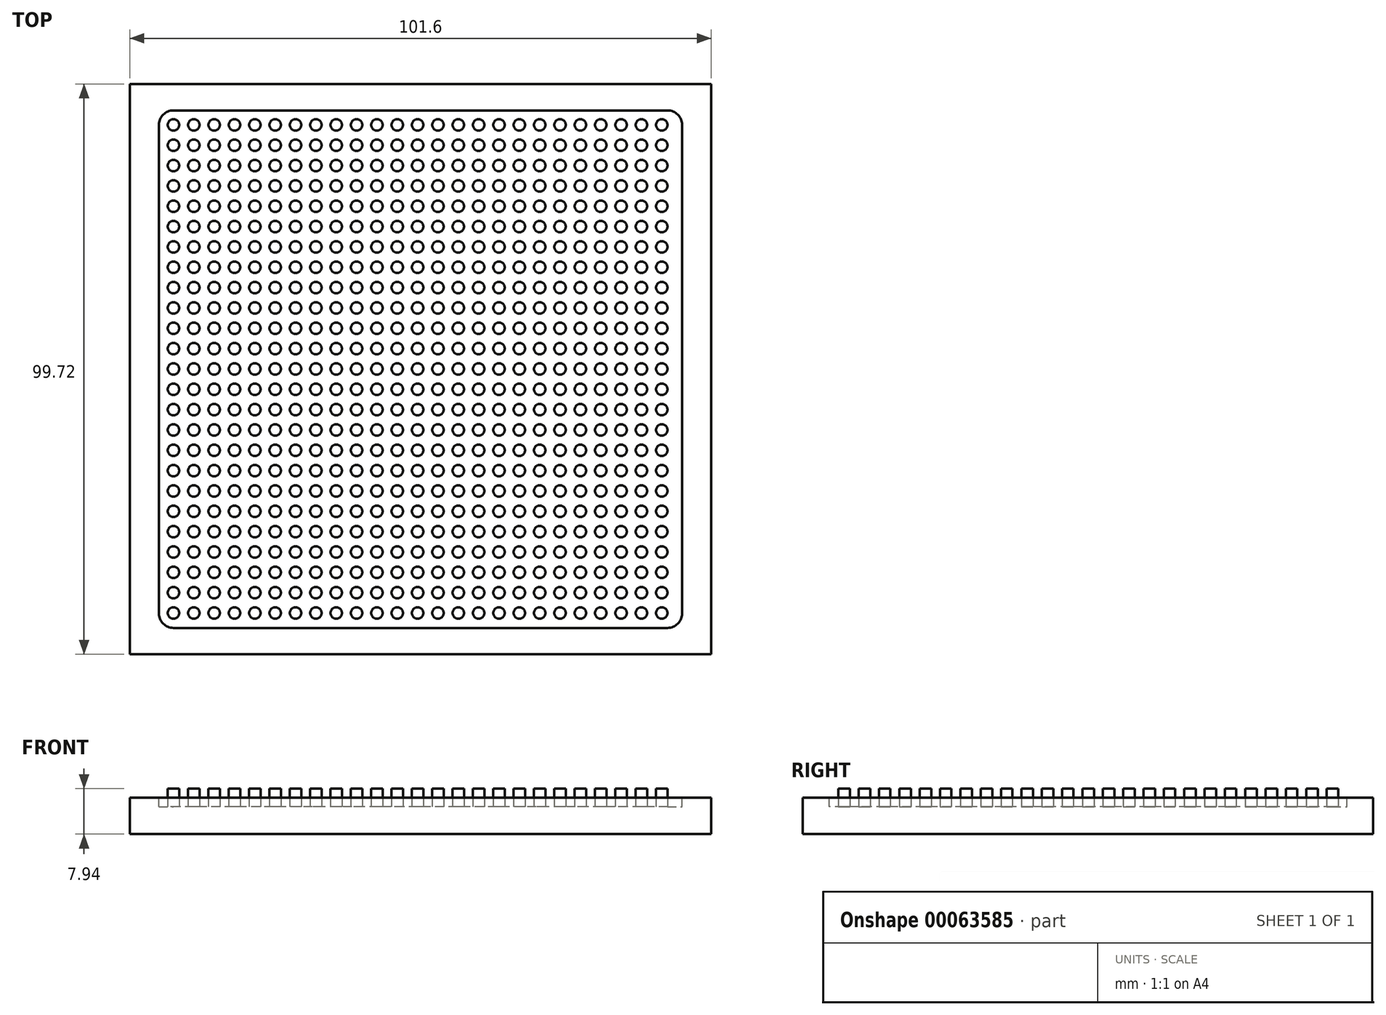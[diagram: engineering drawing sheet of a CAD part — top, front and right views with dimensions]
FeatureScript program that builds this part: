
annotation { "Feature Type Name" : "Feature", "Feature Type Description" : "" }
export const myFeature = defineFeature(function(context is Context, id is Id, definition is map)
    precondition{}
    {
        {
            var Q0;
            Q0=qCreatedBy(makeId("Top.planeOp"),FACE);
            var sketch = newSketch(context, id + "F0", { "sketchPlane" : qUnion([Q0])});
            skLineSegment(sketch, "E0.rect.bottom", {"start": v(50.8, 49.86) * mm, "end": v(-50.8, 49.86) * mm});
            skLineSegment(sketch, "E0.rect.top", {"start": v(50.8, -49.86) * mm, "end": v(-50.8, -49.86) * mm});
            skLineSegment(sketch, "E0.rect.left", {"start": v(50.8, 49.86) * mm, "end": v(50.8, -49.86) * mm});
            skLineSegment(sketch, "E0.rect.right", {"start": v(-50.8, 49.86) * mm, "end": v(-50.8, -49.86) * mm});
            skPoint(sketch, "E0.rect.middle", {"position": v(0, 0) * mm});
            skSolve(sketch);
        }
        {
            var Q0;
            Q0=makeQuery(id+"F0.imprint","IMPRINT",FACE,{"disambiguationData":[TD([[makeQuery(id+"F0.imprint","IMPRINT",EDGE,{"derivedFrom":sQuery(id+"F0.wireOp",EDGE,"E0.rect.bottom")}),1.0]])]});
            extrude(context, id + "F1", {"entities" : qUnion([Q0]), "depth" : 6.35 * mm});
        }
        {
            var Q0;
            Q0=makeQuery(id+"F1.opExtrude","CAP_FACE",FACE,{"disambiguationData":[OSD([sQuery(id+"F0.wireOp",EDGE,"E0.rect.bottom"),sQuery(id+"F0.wireOp",EDGE,"E0.rect.top"),sQuery(id+"F0.wireOp",EDGE,"E0.rect.left"),sQuery(id+"F0.wireOp",EDGE,"E0.rect.right")])],"isStart":false});
            var sketch = newSketch(context, id + "F2", { "sketchPlane" : qUnion([Q0])});
            skLineSegment(sketch, "E1.rect.bottom", {"start": v(43.18, 45.25) * mm, "end": v(-43.18, 45.25) * mm});
            skLineSegment(sketch, "E1.rect.top", {"start": v(43.18, -45.25) * mm, "end": v(-43.18, -45.25) * mm});
            skLineSegment(sketch, "E1.rect.left", {"start": v(45.72, 42.7) * mm, "end": v(45.72, -42.7) * mm});
            skLineSegment(sketch, "E1.rect.right", {"start": v(-45.72, 42.7) * mm, "end": v(-45.72, -42.7) * mm});
            skPoint(sketch, "E1.rect.middle", {"position": v(0, 0) * mm});
            skPoint(sketch, "E2.visualSharp", {"position": v(-45.72, 45.25) * mm});
            skArc(sketch, "E2.filletArc", {"start": v(-43.18, 45.25) * mm, "mid": v(-44.98, 44.5) * mm, "end": v(-45.72, 42.7) * mm});
            skPoint(sketch, "E3.visualSharp", {"position": v(-45.72, -45.25) * mm});
            skArc(sketch, "E3.filletArc", {"start": v(-45.72, -42.7) * mm, "mid": v(-44.98, -44.5) * mm, "end": v(-43.18, -45.25) * mm});
            skPoint(sketch, "E4.visualSharp", {"position": v(45.72, -45.25) * mm});
            skArc(sketch, "E4.filletArc", {"start": v(43.18, -45.25) * mm, "mid": v(44.98, -44.5) * mm, "end": v(45.72, -42.7) * mm});
            skPoint(sketch, "E5.visualSharp", {"position": v(45.72, 45.25) * mm});
            skArc(sketch, "E5.filletArc", {"start": v(45.72, 42.7) * mm, "mid": v(44.98, 44.5) * mm, "end": v(43.18, 45.25) * mm});
            skSolve(sketch);
        }
        {
            var Q0;
            Q0=makeQuery(id+"F2.imprint","IMPRINT",FACE,{"disambiguationData":[TD([[makeQuery(id+"F2.imprint","IMPRINT",EDGE,{"derivedFrom":sQuery(id+"F2.wireOp",EDGE,"E1.rect.bottom")}),1.0]])]});
            extrude(context, id + "F3", {"entities" : qUnion([Q0]), "operationType" : NewBodyOperationType.REMOVE, "oppositeDirection" : true, "depth" : 1.59 * mm});
        }
        {
            var Q0;
            Q0=makeQuery(id+"F3.boolean.opBoolean","COPY",FACE,{"derivedFrom":makeQuery(id+"F3.opExtrude","CAP_FACE",FACE,{"disambiguationData":[OSD([sQuery(id+"F2.wireOp",EDGE,"E1.rect.bottom"),sQuery(id+"F2.wireOp",EDGE,"E1.rect.top"),sQuery(id+"F2.wireOp",EDGE,"E1.rect.left"),sQuery(id+"F2.wireOp",EDGE,"E1.rect.right"),sQuery(id+"F2.wireOp",EDGE,"E2.filletArc"),sQuery(id+"F2.wireOp",EDGE,"E3.filletArc"),sQuery(id+"F2.wireOp",EDGE,"E4.filletArc"),sQuery(id+"F2.wireOp",EDGE,"E5.filletArc")])],"isStart":false})});
            var sketch = newSketch(context, id + "F4", { "sketchPlane" : qUnion([Q0])});
            skCircle(sketch, "E6", {"center": v(-43.18, 42.7) * mm, "radius": 1 * mm});
            skCircle(sketch, "E7.0.1.0", {"center": v(-43.18, 39.15) * mm, "radius": 1 * mm});
            skCircle(sketch, "E7.0.2.0", {"center": v(-43.18, 35.6) * mm, "radius": 1 * mm});
            skCircle(sketch, "E7.0.3.0", {"center": v(-43.18, 32.04) * mm, "radius": 1 * mm});
            skCircle(sketch, "E7.0.4.0", {"center": v(-43.18, 28.48) * mm, "radius": 1 * mm});
            skCircle(sketch, "E7.0.5.0", {"center": v(-43.18, 24.93) * mm, "radius": 1 * mm});
            skCircle(sketch, "E7.0.6.0", {"center": v(-43.18, 21.37) * mm, "radius": 1 * mm});
            skCircle(sketch, "E7.0.7.0", {"center": v(-43.18, 17.81) * mm, "radius": 1 * mm});
            skCircle(sketch, "E7.0.8.0", {"center": v(-43.18, 14.26) * mm, "radius": 1 * mm});
            skCircle(sketch, "E7.0.9.0", {"center": v(-43.18, 10.7) * mm, "radius": 1 * mm});
            skCircle(sketch, "E7.0.10.0", {"center": v(-43.18, 7.15) * mm, "radius": 1 * mm});
            skCircle(sketch, "E7.0.11.0", {"center": v(-43.18, 3.6) * mm, "radius": 1 * mm});
            skCircle(sketch, "E7.0.12.0", {"center": v(-43.18, 0.03) * mm, "radius": 1 * mm});
            skCircle(sketch, "E7.0.13.0", {"center": v(-43.18, -3.52) * mm, "radius": 1 * mm});
            skCircle(sketch, "E7.0.14.0", {"center": v(-43.18, -7.08) * mm, "radius": 1 * mm});
            skCircle(sketch, "E7.0.15.0", {"center": v(-43.18, -10.63) * mm, "radius": 1 * mm});
            skCircle(sketch, "E7.0.16.0", {"center": v(-43.18, -14.19) * mm, "radius": 1 * mm});
            skCircle(sketch, "E7.0.17.0", {"center": v(-43.18, -17.75) * mm, "radius": 1 * mm});
            skCircle(sketch, "E7.0.18.0", {"center": v(-43.18, -21.3) * mm, "radius": 1 * mm});
            skCircle(sketch, "E7.0.19.0", {"center": v(-43.18, -24.86) * mm, "radius": 1 * mm});
            skCircle(sketch, "E7.0.20.0", {"center": v(-43.18, -28.41) * mm, "radius": 1 * mm});
            skCircle(sketch, "E7.0.21.0", {"center": v(-43.18, -31.97) * mm, "radius": 1 * mm});
            skCircle(sketch, "E7.0.22.0", {"center": v(-43.18, -35.53) * mm, "radius": 1 * mm});
            skCircle(sketch, "E7.0.23.0", {"center": v(-43.18, -39.08) * mm, "radius": 1 * mm});
            skCircle(sketch, "E7.0.24.0", {"center": v(-43.18, -42.64) * mm, "radius": 1 * mm});
            skCircle(sketch, "E7.1.0.0", {"center": v(-39.62, 42.7) * mm, "radius": 1 * mm});
            skCircle(sketch, "E7.1.1.0", {"center": v(-39.62, 39.15) * mm, "radius": 1 * mm});
            skCircle(sketch, "E7.1.2.0", {"center": v(-39.62, 35.6) * mm, "radius": 1 * mm});
            skCircle(sketch, "E7.1.3.0", {"center": v(-39.62, 32.04) * mm, "radius": 1 * mm});
            skCircle(sketch, "E7.1.4.0", {"center": v(-39.62, 28.48) * mm, "radius": 1 * mm});
            skCircle(sketch, "E7.1.5.0", {"center": v(-39.62, 24.93) * mm, "radius": 1 * mm});
            skCircle(sketch, "E7.1.6.0", {"center": v(-39.62, 21.37) * mm, "radius": 1 * mm});
            skCircle(sketch, "E7.1.7.0", {"center": v(-39.62, 17.81) * mm, "radius": 1 * mm});
            skCircle(sketch, "E7.1.8.0", {"center": v(-39.62, 14.26) * mm, "radius": 1 * mm});
            skCircle(sketch, "E7.1.9.0", {"center": v(-39.62, 10.7) * mm, "radius": 1 * mm});
            skCircle(sketch, "E7.1.10.0", {"center": v(-39.62, 7.15) * mm, "radius": 1 * mm});
            skCircle(sketch, "E7.1.11.0", {"center": v(-39.62, 3.6) * mm, "radius": 1 * mm});
            skCircle(sketch, "E7.1.12.0", {"center": v(-39.62, 0.03) * mm, "radius": 1 * mm});
            skCircle(sketch, "E7.1.13.0", {"center": v(-39.62, -3.52) * mm, "radius": 1 * mm});
            skCircle(sketch, "E7.1.14.0", {"center": v(-39.62, -7.08) * mm, "radius": 1 * mm});
            skCircle(sketch, "E7.1.15.0", {"center": v(-39.62, -10.63) * mm, "radius": 1 * mm});
            skCircle(sketch, "E7.1.16.0", {"center": v(-39.62, -14.19) * mm, "radius": 1 * mm});
            skCircle(sketch, "E7.1.17.0", {"center": v(-39.62, -17.75) * mm, "radius": 1 * mm});
            skCircle(sketch, "E7.1.18.0", {"center": v(-39.62, -21.3) * mm, "radius": 1 * mm});
            skCircle(sketch, "E7.1.19.0", {"center": v(-39.62, -24.86) * mm, "radius": 1 * mm});
            skCircle(sketch, "E7.1.20.0", {"center": v(-39.62, -28.41) * mm, "radius": 1 * mm});
            skCircle(sketch, "E7.1.21.0", {"center": v(-39.62, -31.97) * mm, "radius": 1 * mm});
            skCircle(sketch, "E7.1.22.0", {"center": v(-39.62, -35.53) * mm, "radius": 1 * mm});
            skCircle(sketch, "E7.1.23.0", {"center": v(-39.62, -39.08) * mm, "radius": 1 * mm});
            skCircle(sketch, "E7.1.24.0", {"center": v(-39.62, -42.64) * mm, "radius": 1 * mm});
            skCircle(sketch, "E7.2.0.0", {"center": v(-36.07, 42.7) * mm, "radius": 1 * mm});
            skCircle(sketch, "E7.2.1.0", {"center": v(-36.07, 39.15) * mm, "radius": 1 * mm});
            skCircle(sketch, "E7.2.2.0", {"center": v(-36.07, 35.6) * mm, "radius": 1 * mm});
            skCircle(sketch, "E7.2.3.0", {"center": v(-36.07, 32.04) * mm, "radius": 1 * mm});
            skCircle(sketch, "E7.2.4.0", {"center": v(-36.07, 28.48) * mm, "radius": 1 * mm});
            skCircle(sketch, "E7.2.5.0", {"center": v(-36.07, 24.93) * mm, "radius": 1 * mm});
            skCircle(sketch, "E7.2.6.0", {"center": v(-36.07, 21.37) * mm, "radius": 1 * mm});
            skCircle(sketch, "E7.2.7.0", {"center": v(-36.07, 17.81) * mm, "radius": 1 * mm});
            skCircle(sketch, "E7.2.8.0", {"center": v(-36.07, 14.26) * mm, "radius": 1 * mm});
            skCircle(sketch, "E7.2.9.0", {"center": v(-36.07, 10.7) * mm, "radius": 1 * mm});
            skCircle(sketch, "E7.2.10.0", {"center": v(-36.07, 7.15) * mm, "radius": 1 * mm});
            skCircle(sketch, "E7.2.11.0", {"center": v(-36.07, 3.6) * mm, "radius": 1 * mm});
            skCircle(sketch, "E7.2.12.0", {"center": v(-36.07, 0.03) * mm, "radius": 1 * mm});
            skCircle(sketch, "E7.2.13.0", {"center": v(-36.07, -3.52) * mm, "radius": 1 * mm});
            skCircle(sketch, "E7.2.14.0", {"center": v(-36.07, -7.08) * mm, "radius": 1 * mm});
            skCircle(sketch, "E7.2.15.0", {"center": v(-36.07, -10.63) * mm, "radius": 1 * mm});
            skCircle(sketch, "E7.2.16.0", {"center": v(-36.07, -14.19) * mm, "radius": 1 * mm});
            skCircle(sketch, "E7.2.17.0", {"center": v(-36.07, -17.75) * mm, "radius": 1 * mm});
            skCircle(sketch, "E7.2.18.0", {"center": v(-36.07, -21.3) * mm, "radius": 1 * mm});
            skCircle(sketch, "E7.2.19.0", {"center": v(-36.07, -24.86) * mm, "radius": 1 * mm});
            skCircle(sketch, "E7.2.20.0", {"center": v(-36.07, -28.41) * mm, "radius": 1 * mm});
            skCircle(sketch, "E7.2.21.0", {"center": v(-36.07, -31.97) * mm, "radius": 1 * mm});
            skCircle(sketch, "E7.2.22.0", {"center": v(-36.07, -35.53) * mm, "radius": 1 * mm});
            skCircle(sketch, "E7.2.23.0", {"center": v(-36.07, -39.08) * mm, "radius": 1 * mm});
            skCircle(sketch, "E7.2.24.0", {"center": v(-36.07, -42.64) * mm, "radius": 1 * mm});
            skCircle(sketch, "E7.3.0.0", {"center": v(-32.51, 42.7) * mm, "radius": 1 * mm});
            skCircle(sketch, "E7.3.1.0", {"center": v(-32.51, 39.15) * mm, "radius": 1 * mm});
            skCircle(sketch, "E7.3.2.0", {"center": v(-32.51, 35.6) * mm, "radius": 1 * mm});
            skCircle(sketch, "E7.3.3.0", {"center": v(-32.51, 32.04) * mm, "radius": 1 * mm});
            skCircle(sketch, "E7.3.4.0", {"center": v(-32.51, 28.48) * mm, "radius": 1 * mm});
            skCircle(sketch, "E7.3.5.0", {"center": v(-32.51, 24.93) * mm, "radius": 1 * mm});
            skCircle(sketch, "E7.3.6.0", {"center": v(-32.51, 21.37) * mm, "radius": 1 * mm});
            skCircle(sketch, "E7.3.7.0", {"center": v(-32.51, 17.81) * mm, "radius": 1 * mm});
            skCircle(sketch, "E7.3.8.0", {"center": v(-32.51, 14.26) * mm, "radius": 1 * mm});
            skCircle(sketch, "E7.3.9.0", {"center": v(-32.51, 10.7) * mm, "radius": 1 * mm});
            skCircle(sketch, "E7.3.10.0", {"center": v(-32.51, 7.15) * mm, "radius": 1 * mm});
            skCircle(sketch, "E7.3.11.0", {"center": v(-32.51, 3.6) * mm, "radius": 1 * mm});
            skCircle(sketch, "E7.3.12.0", {"center": v(-32.51, 0.03) * mm, "radius": 1 * mm});
            skCircle(sketch, "E7.3.13.0", {"center": v(-32.51, -3.52) * mm, "radius": 1 * mm});
            skCircle(sketch, "E7.3.14.0", {"center": v(-32.51, -7.08) * mm, "radius": 1 * mm});
            skCircle(sketch, "E7.3.15.0", {"center": v(-32.51, -10.63) * mm, "radius": 1 * mm});
            skCircle(sketch, "E7.3.16.0", {"center": v(-32.51, -14.19) * mm, "radius": 1 * mm});
            skCircle(sketch, "E7.3.17.0", {"center": v(-32.51, -17.75) * mm, "radius": 1 * mm});
            skCircle(sketch, "E7.3.18.0", {"center": v(-32.51, -21.3) * mm, "radius": 1 * mm});
            skCircle(sketch, "E7.3.19.0", {"center": v(-32.51, -24.86) * mm, "radius": 1 * mm});
            skCircle(sketch, "E7.3.20.0", {"center": v(-32.51, -28.41) * mm, "radius": 1 * mm});
            skCircle(sketch, "E7.3.21.0", {"center": v(-32.51, -31.97) * mm, "radius": 1 * mm});
            skCircle(sketch, "E7.3.22.0", {"center": v(-32.51, -35.53) * mm, "radius": 1 * mm});
            skCircle(sketch, "E7.3.23.0", {"center": v(-32.51, -39.08) * mm, "radius": 1 * mm});
            skCircle(sketch, "E7.3.24.0", {"center": v(-32.51, -42.64) * mm, "radius": 1 * mm});
            skCircle(sketch, "E7.4.0.0", {"center": v(-28.96, 42.7) * mm, "radius": 1 * mm});
            skCircle(sketch, "E7.4.1.0", {"center": v(-28.96, 39.15) * mm, "radius": 1 * mm});
            skCircle(sketch, "E7.4.2.0", {"center": v(-28.96, 35.6) * mm, "radius": 1 * mm});
            skCircle(sketch, "E7.4.3.0", {"center": v(-28.96, 32.04) * mm, "radius": 1 * mm});
            skCircle(sketch, "E7.4.4.0", {"center": v(-28.96, 28.48) * mm, "radius": 1 * mm});
            skCircle(sketch, "E7.4.5.0", {"center": v(-28.96, 24.93) * mm, "radius": 1 * mm});
            skCircle(sketch, "E7.4.6.0", {"center": v(-28.96, 21.37) * mm, "radius": 1 * mm});
            skCircle(sketch, "E7.4.7.0", {"center": v(-28.96, 17.81) * mm, "radius": 1 * mm});
            skCircle(sketch, "E7.4.8.0", {"center": v(-28.96, 14.26) * mm, "radius": 1 * mm});
            skCircle(sketch, "E7.4.9.0", {"center": v(-28.96, 10.7) * mm, "radius": 1 * mm});
            skCircle(sketch, "E7.4.10.0", {"center": v(-28.96, 7.15) * mm, "radius": 1 * mm});
            skCircle(sketch, "E7.4.11.0", {"center": v(-28.96, 3.6) * mm, "radius": 1 * mm});
            skCircle(sketch, "E7.4.12.0", {"center": v(-28.96, 0.03) * mm, "radius": 1 * mm});
            skCircle(sketch, "E7.4.13.0", {"center": v(-28.96, -3.52) * mm, "radius": 1 * mm});
            skCircle(sketch, "E7.4.14.0", {"center": v(-28.96, -7.08) * mm, "radius": 1 * mm});
            skCircle(sketch, "E7.4.15.0", {"center": v(-28.96, -10.63) * mm, "radius": 1 * mm});
            skCircle(sketch, "E7.4.16.0", {"center": v(-28.96, -14.19) * mm, "radius": 1 * mm});
            skCircle(sketch, "E7.4.17.0", {"center": v(-28.96, -17.75) * mm, "radius": 1 * mm});
            skCircle(sketch, "E7.4.18.0", {"center": v(-28.96, -21.3) * mm, "radius": 1 * mm});
            skCircle(sketch, "E7.4.19.0", {"center": v(-28.96, -24.86) * mm, "radius": 1 * mm});
            skCircle(sketch, "E7.4.20.0", {"center": v(-28.96, -28.41) * mm, "radius": 1 * mm});
            skCircle(sketch, "E7.4.21.0", {"center": v(-28.96, -31.97) * mm, "radius": 1 * mm});
            skCircle(sketch, "E7.4.22.0", {"center": v(-28.96, -35.53) * mm, "radius": 1 * mm});
            skCircle(sketch, "E7.4.23.0", {"center": v(-28.96, -39.08) * mm, "radius": 1 * mm});
            skCircle(sketch, "E7.4.24.0", {"center": v(-28.96, -42.64) * mm, "radius": 1 * mm});
            skCircle(sketch, "E7.5.0.0", {"center": v(-25.4, 42.7) * mm, "radius": 1 * mm});
            skCircle(sketch, "E7.5.1.0", {"center": v(-25.4, 39.15) * mm, "radius": 1 * mm});
            skCircle(sketch, "E7.5.2.0", {"center": v(-25.4, 35.6) * mm, "radius": 1 * mm});
            skCircle(sketch, "E7.5.3.0", {"center": v(-25.4, 32.04) * mm, "radius": 1 * mm});
            skCircle(sketch, "E7.5.4.0", {"center": v(-25.4, 28.48) * mm, "radius": 1 * mm});
            skCircle(sketch, "E7.5.5.0", {"center": v(-25.4, 24.93) * mm, "radius": 1 * mm});
            skCircle(sketch, "E7.5.6.0", {"center": v(-25.4, 21.37) * mm, "radius": 1 * mm});
            skCircle(sketch, "E7.5.7.0", {"center": v(-25.4, 17.81) * mm, "radius": 1 * mm});
            skCircle(sketch, "E7.5.8.0", {"center": v(-25.4, 14.26) * mm, "radius": 1 * mm});
            skCircle(sketch, "E7.5.9.0", {"center": v(-25.4, 10.7) * mm, "radius": 1 * mm});
            skCircle(sketch, "E7.5.10.0", {"center": v(-25.4, 7.15) * mm, "radius": 1 * mm});
            skCircle(sketch, "E7.5.11.0", {"center": v(-25.4, 3.6) * mm, "radius": 1 * mm});
            skCircle(sketch, "E7.5.12.0", {"center": v(-25.4, 0.03) * mm, "radius": 1 * mm});
            skCircle(sketch, "E7.5.13.0", {"center": v(-25.4, -3.52) * mm, "radius": 1 * mm});
            skCircle(sketch, "E7.5.14.0", {"center": v(-25.4, -7.08) * mm, "radius": 1 * mm});
            skCircle(sketch, "E7.5.15.0", {"center": v(-25.4, -10.63) * mm, "radius": 1 * mm});
            skCircle(sketch, "E7.5.16.0", {"center": v(-25.4, -14.19) * mm, "radius": 1 * mm});
            skCircle(sketch, "E7.5.17.0", {"center": v(-25.4, -17.75) * mm, "radius": 1 * mm});
            skCircle(sketch, "E7.5.18.0", {"center": v(-25.4, -21.3) * mm, "radius": 1 * mm});
            skCircle(sketch, "E7.5.19.0", {"center": v(-25.4, -24.86) * mm, "radius": 1 * mm});
            skCircle(sketch, "E7.5.20.0", {"center": v(-25.4, -28.41) * mm, "radius": 1 * mm});
            skCircle(sketch, "E7.5.21.0", {"center": v(-25.4, -31.97) * mm, "radius": 1 * mm});
            skCircle(sketch, "E7.5.22.0", {"center": v(-25.4, -35.53) * mm, "radius": 1 * mm});
            skCircle(sketch, "E7.5.23.0", {"center": v(-25.4, -39.08) * mm, "radius": 1 * mm});
            skCircle(sketch, "E7.5.24.0", {"center": v(-25.4, -42.64) * mm, "radius": 1 * mm});
            skCircle(sketch, "E7.6.0.0", {"center": v(-21.84, 42.7) * mm, "radius": 1 * mm});
            skCircle(sketch, "E7.6.1.0", {"center": v(-21.84, 39.15) * mm, "radius": 1 * mm});
            skCircle(sketch, "E7.6.2.0", {"center": v(-21.84, 35.6) * mm, "radius": 1 * mm});
            skCircle(sketch, "E7.6.3.0", {"center": v(-21.84, 32.04) * mm, "radius": 1 * mm});
            skCircle(sketch, "E7.6.4.0", {"center": v(-21.84, 28.48) * mm, "radius": 1 * mm});
            skCircle(sketch, "E7.6.5.0", {"center": v(-21.84, 24.93) * mm, "radius": 1 * mm});
            skCircle(sketch, "E7.6.6.0", {"center": v(-21.84, 21.37) * mm, "radius": 1 * mm});
            skCircle(sketch, "E7.6.7.0", {"center": v(-21.84, 17.81) * mm, "radius": 1 * mm});
            skCircle(sketch, "E7.6.8.0", {"center": v(-21.84, 14.26) * mm, "radius": 1 * mm});
            skCircle(sketch, "E7.6.9.0", {"center": v(-21.84, 10.7) * mm, "radius": 1 * mm});
            skCircle(sketch, "E7.6.10.0", {"center": v(-21.84, 7.15) * mm, "radius": 1 * mm});
            skCircle(sketch, "E7.6.11.0", {"center": v(-21.84, 3.6) * mm, "radius": 1 * mm});
            skCircle(sketch, "E7.6.12.0", {"center": v(-21.84, 0.03) * mm, "radius": 1 * mm});
            skCircle(sketch, "E7.6.13.0", {"center": v(-21.84, -3.52) * mm, "radius": 1 * mm});
            skCircle(sketch, "E7.6.14.0", {"center": v(-21.84, -7.08) * mm, "radius": 1 * mm});
            skCircle(sketch, "E7.6.15.0", {"center": v(-21.84, -10.63) * mm, "radius": 1 * mm});
            skCircle(sketch, "E7.6.16.0", {"center": v(-21.84, -14.19) * mm, "radius": 1 * mm});
            skCircle(sketch, "E7.6.17.0", {"center": v(-21.84, -17.75) * mm, "radius": 1 * mm});
            skCircle(sketch, "E7.6.18.0", {"center": v(-21.84, -21.3) * mm, "radius": 1 * mm});
            skCircle(sketch, "E7.6.19.0", {"center": v(-21.84, -24.86) * mm, "radius": 1 * mm});
            skCircle(sketch, "E7.6.20.0", {"center": v(-21.84, -28.41) * mm, "radius": 1 * mm});
            skCircle(sketch, "E7.6.21.0", {"center": v(-21.84, -31.97) * mm, "radius": 1 * mm});
            skCircle(sketch, "E7.6.22.0", {"center": v(-21.84, -35.53) * mm, "radius": 1 * mm});
            skCircle(sketch, "E7.6.23.0", {"center": v(-21.84, -39.08) * mm, "radius": 1 * mm});
            skCircle(sketch, "E7.6.24.0", {"center": v(-21.84, -42.64) * mm, "radius": 1 * mm});
            skCircle(sketch, "E7.7.0.0", {"center": v(-18.29, 42.7) * mm, "radius": 1 * mm});
            skCircle(sketch, "E7.7.1.0", {"center": v(-18.29, 39.15) * mm, "radius": 1 * mm});
            skCircle(sketch, "E7.7.2.0", {"center": v(-18.29, 35.6) * mm, "radius": 1 * mm});
            skCircle(sketch, "E7.7.3.0", {"center": v(-18.29, 32.04) * mm, "radius": 1 * mm});
            skCircle(sketch, "E7.7.4.0", {"center": v(-18.29, 28.48) * mm, "radius": 1 * mm});
            skCircle(sketch, "E7.7.5.0", {"center": v(-18.29, 24.93) * mm, "radius": 1 * mm});
            skCircle(sketch, "E7.7.6.0", {"center": v(-18.29, 21.37) * mm, "radius": 1 * mm});
            skCircle(sketch, "E7.7.7.0", {"center": v(-18.29, 17.81) * mm, "radius": 1 * mm});
            skCircle(sketch, "E7.7.8.0", {"center": v(-18.29, 14.26) * mm, "radius": 1 * mm});
            skCircle(sketch, "E7.7.9.0", {"center": v(-18.29, 10.7) * mm, "radius": 1 * mm});
            skCircle(sketch, "E7.7.10.0", {"center": v(-18.29, 7.15) * mm, "radius": 1 * mm});
            skCircle(sketch, "E7.7.11.0", {"center": v(-18.29, 3.6) * mm, "radius": 1 * mm});
            skCircle(sketch, "E7.7.12.0", {"center": v(-18.29, 0.03) * mm, "radius": 1 * mm});
            skCircle(sketch, "E7.7.13.0", {"center": v(-18.29, -3.52) * mm, "radius": 1 * mm});
            skCircle(sketch, "E7.7.14.0", {"center": v(-18.29, -7.08) * mm, "radius": 1 * mm});
            skCircle(sketch, "E7.7.15.0", {"center": v(-18.29, -10.63) * mm, "radius": 1 * mm});
            skCircle(sketch, "E7.7.16.0", {"center": v(-18.29, -14.19) * mm, "radius": 1 * mm});
            skCircle(sketch, "E7.7.17.0", {"center": v(-18.29, -17.75) * mm, "radius": 1 * mm});
            skCircle(sketch, "E7.7.18.0", {"center": v(-18.29, -21.3) * mm, "radius": 1 * mm});
            skCircle(sketch, "E7.7.19.0", {"center": v(-18.29, -24.86) * mm, "radius": 1 * mm});
            skCircle(sketch, "E7.7.20.0", {"center": v(-18.29, -28.41) * mm, "radius": 1 * mm});
            skCircle(sketch, "E7.7.21.0", {"center": v(-18.29, -31.97) * mm, "radius": 1 * mm});
            skCircle(sketch, "E7.7.22.0", {"center": v(-18.29, -35.53) * mm, "radius": 1 * mm});
            skCircle(sketch, "E7.7.23.0", {"center": v(-18.29, -39.08) * mm, "radius": 1 * mm});
            skCircle(sketch, "E7.7.24.0", {"center": v(-18.29, -42.64) * mm, "radius": 1 * mm});
            skCircle(sketch, "E7.8.0.0", {"center": v(-14.73, 42.7) * mm, "radius": 1 * mm});
            skCircle(sketch, "E7.8.1.0", {"center": v(-14.73, 39.15) * mm, "radius": 1 * mm});
            skCircle(sketch, "E7.8.2.0", {"center": v(-14.73, 35.6) * mm, "radius": 1 * mm});
            skCircle(sketch, "E7.8.3.0", {"center": v(-14.73, 32.04) * mm, "radius": 1 * mm});
            skCircle(sketch, "E7.8.4.0", {"center": v(-14.73, 28.48) * mm, "radius": 1 * mm});
            skCircle(sketch, "E7.8.5.0", {"center": v(-14.73, 24.93) * mm, "radius": 1 * mm});
            skCircle(sketch, "E7.8.6.0", {"center": v(-14.73, 21.37) * mm, "radius": 1 * mm});
            skCircle(sketch, "E7.8.7.0", {"center": v(-14.73, 17.81) * mm, "radius": 1 * mm});
            skCircle(sketch, "E7.8.8.0", {"center": v(-14.73, 14.26) * mm, "radius": 1 * mm});
            skCircle(sketch, "E7.8.9.0", {"center": v(-14.73, 10.7) * mm, "radius": 1 * mm});
            skCircle(sketch, "E7.8.10.0", {"center": v(-14.73, 7.15) * mm, "radius": 1 * mm});
            skCircle(sketch, "E7.8.11.0", {"center": v(-14.73, 3.6) * mm, "radius": 1 * mm});
            skCircle(sketch, "E7.8.12.0", {"center": v(-14.73, 0.03) * mm, "radius": 1 * mm});
            skCircle(sketch, "E7.8.13.0", {"center": v(-14.73, -3.52) * mm, "radius": 1 * mm});
            skCircle(sketch, "E7.8.14.0", {"center": v(-14.73, -7.08) * mm, "radius": 1 * mm});
            skCircle(sketch, "E7.8.15.0", {"center": v(-14.73, -10.63) * mm, "radius": 1 * mm});
            skCircle(sketch, "E7.8.16.0", {"center": v(-14.73, -14.19) * mm, "radius": 1 * mm});
            skCircle(sketch, "E7.8.17.0", {"center": v(-14.73, -17.75) * mm, "radius": 1 * mm});
            skCircle(sketch, "E7.8.18.0", {"center": v(-14.73, -21.3) * mm, "radius": 1 * mm});
            skCircle(sketch, "E7.8.19.0", {"center": v(-14.73, -24.86) * mm, "radius": 1 * mm});
            skCircle(sketch, "E7.8.20.0", {"center": v(-14.73, -28.41) * mm, "radius": 1 * mm});
            skCircle(sketch, "E7.8.21.0", {"center": v(-14.73, -31.97) * mm, "radius": 1 * mm});
            skCircle(sketch, "E7.8.22.0", {"center": v(-14.73, -35.53) * mm, "radius": 1 * mm});
            skCircle(sketch, "E7.8.23.0", {"center": v(-14.73, -39.08) * mm, "radius": 1 * mm});
            skCircle(sketch, "E7.8.24.0", {"center": v(-14.73, -42.64) * mm, "radius": 1 * mm});
            skCircle(sketch, "E7.9.0.0", {"center": v(-11.18, 42.7) * mm, "radius": 1 * mm});
            skCircle(sketch, "E7.9.1.0", {"center": v(-11.18, 39.15) * mm, "radius": 1 * mm});
            skCircle(sketch, "E7.9.2.0", {"center": v(-11.18, 35.6) * mm, "radius": 1 * mm});
            skCircle(sketch, "E7.9.3.0", {"center": v(-11.18, 32.04) * mm, "radius": 1 * mm});
            skCircle(sketch, "E7.9.4.0", {"center": v(-11.18, 28.48) * mm, "radius": 1 * mm});
            skCircle(sketch, "E7.9.5.0", {"center": v(-11.18, 24.93) * mm, "radius": 1 * mm});
            skCircle(sketch, "E7.9.6.0", {"center": v(-11.18, 21.37) * mm, "radius": 1 * mm});
            skCircle(sketch, "E7.9.7.0", {"center": v(-11.18, 17.81) * mm, "radius": 1 * mm});
            skCircle(sketch, "E7.9.8.0", {"center": v(-11.18, 14.26) * mm, "radius": 1 * mm});
            skCircle(sketch, "E7.9.9.0", {"center": v(-11.18, 10.7) * mm, "radius": 1 * mm});
            skCircle(sketch, "E7.9.10.0", {"center": v(-11.18, 7.15) * mm, "radius": 1 * mm});
            skCircle(sketch, "E7.9.11.0", {"center": v(-11.18, 3.6) * mm, "radius": 1 * mm});
            skCircle(sketch, "E7.9.12.0", {"center": v(-11.18, 0.03) * mm, "radius": 1 * mm});
            skCircle(sketch, "E7.9.13.0", {"center": v(-11.18, -3.52) * mm, "radius": 1 * mm});
            skCircle(sketch, "E7.9.14.0", {"center": v(-11.18, -7.08) * mm, "radius": 1 * mm});
            skCircle(sketch, "E7.9.15.0", {"center": v(-11.18, -10.63) * mm, "radius": 1 * mm});
            skCircle(sketch, "E7.9.16.0", {"center": v(-11.18, -14.19) * mm, "radius": 1 * mm});
            skCircle(sketch, "E7.9.17.0", {"center": v(-11.18, -17.75) * mm, "radius": 1 * mm});
            skCircle(sketch, "E7.9.18.0", {"center": v(-11.18, -21.3) * mm, "radius": 1 * mm});
            skCircle(sketch, "E7.9.19.0", {"center": v(-11.18, -24.86) * mm, "radius": 1 * mm});
            skCircle(sketch, "E7.9.20.0", {"center": v(-11.18, -28.41) * mm, "radius": 1 * mm});
            skCircle(sketch, "E7.9.21.0", {"center": v(-11.18, -31.97) * mm, "radius": 1 * mm});
            skCircle(sketch, "E7.9.22.0", {"center": v(-11.18, -35.53) * mm, "radius": 1 * mm});
            skCircle(sketch, "E7.9.23.0", {"center": v(-11.18, -39.08) * mm, "radius": 1 * mm});
            skCircle(sketch, "E7.9.24.0", {"center": v(-11.18, -42.64) * mm, "radius": 1 * mm});
            skCircle(sketch, "E7.10.0.0", {"center": v(-7.62, 42.7) * mm, "radius": 1 * mm});
            skCircle(sketch, "E7.10.1.0", {"center": v(-7.62, 39.15) * mm, "radius": 1 * mm});
            skCircle(sketch, "E7.10.2.0", {"center": v(-7.62, 35.6) * mm, "radius": 1 * mm});
            skCircle(sketch, "E7.10.3.0", {"center": v(-7.62, 32.04) * mm, "radius": 1 * mm});
            skCircle(sketch, "E7.10.4.0", {"center": v(-7.62, 28.48) * mm, "radius": 1 * mm});
            skCircle(sketch, "E7.10.5.0", {"center": v(-7.62, 24.93) * mm, "radius": 1 * mm});
            skCircle(sketch, "E7.10.6.0", {"center": v(-7.62, 21.37) * mm, "radius": 1 * mm});
            skCircle(sketch, "E7.10.7.0", {"center": v(-7.62, 17.81) * mm, "radius": 1 * mm});
            skCircle(sketch, "E7.10.8.0", {"center": v(-7.62, 14.26) * mm, "radius": 1 * mm});
            skCircle(sketch, "E7.10.9.0", {"center": v(-7.62, 10.7) * mm, "radius": 1 * mm});
            skCircle(sketch, "E7.10.10.0", {"center": v(-7.62, 7.15) * mm, "radius": 1 * mm});
            skCircle(sketch, "E7.10.11.0", {"center": v(-7.62, 3.6) * mm, "radius": 1 * mm});
            skCircle(sketch, "E7.10.12.0", {"center": v(-7.62, 0.03) * mm, "radius": 1 * mm});
            skCircle(sketch, "E7.10.13.0", {"center": v(-7.62, -3.52) * mm, "radius": 1 * mm});
            skCircle(sketch, "E7.10.14.0", {"center": v(-7.62, -7.08) * mm, "radius": 1 * mm});
            skCircle(sketch, "E7.10.15.0", {"center": v(-7.62, -10.63) * mm, "radius": 1 * mm});
            skCircle(sketch, "E7.10.16.0", {"center": v(-7.62, -14.19) * mm, "radius": 1 * mm});
            skCircle(sketch, "E7.10.17.0", {"center": v(-7.62, -17.75) * mm, "radius": 1 * mm});
            skCircle(sketch, "E7.10.18.0", {"center": v(-7.62, -21.3) * mm, "radius": 1 * mm});
            skCircle(sketch, "E7.10.19.0", {"center": v(-7.62, -24.86) * mm, "radius": 1 * mm});
            skCircle(sketch, "E7.10.20.0", {"center": v(-7.62, -28.41) * mm, "radius": 1 * mm});
            skCircle(sketch, "E7.10.21.0", {"center": v(-7.62, -31.97) * mm, "radius": 1 * mm});
            skCircle(sketch, "E7.10.22.0", {"center": v(-7.62, -35.53) * mm, "radius": 1 * mm});
            skCircle(sketch, "E7.10.23.0", {"center": v(-7.62, -39.08) * mm, "radius": 1 * mm});
            skCircle(sketch, "E7.10.24.0", {"center": v(-7.62, -42.64) * mm, "radius": 1 * mm});
            skCircle(sketch, "E7.11.0.0", {"center": v(-4.06, 42.7) * mm, "radius": 1 * mm});
            skCircle(sketch, "E7.11.1.0", {"center": v(-4.06, 39.15) * mm, "radius": 1 * mm});
            skCircle(sketch, "E7.11.2.0", {"center": v(-4.06, 35.6) * mm, "radius": 1 * mm});
            skCircle(sketch, "E7.11.3.0", {"center": v(-4.06, 32.04) * mm, "radius": 1 * mm});
            skCircle(sketch, "E7.11.4.0", {"center": v(-4.06, 28.48) * mm, "radius": 1 * mm});
            skCircle(sketch, "E7.11.5.0", {"center": v(-4.06, 24.93) * mm, "radius": 1 * mm});
            skCircle(sketch, "E7.11.6.0", {"center": v(-4.06, 21.37) * mm, "radius": 1 * mm});
            skCircle(sketch, "E7.11.7.0", {"center": v(-4.06, 17.81) * mm, "radius": 1 * mm});
            skCircle(sketch, "E7.11.8.0", {"center": v(-4.06, 14.26) * mm, "radius": 1 * mm});
            skCircle(sketch, "E7.11.9.0", {"center": v(-4.06, 10.7) * mm, "radius": 1 * mm});
            skCircle(sketch, "E7.11.10.0", {"center": v(-4.06, 7.15) * mm, "radius": 1 * mm});
            skCircle(sketch, "E7.11.11.0", {"center": v(-4.06, 3.6) * mm, "radius": 1 * mm});
            skCircle(sketch, "E7.11.12.0", {"center": v(-4.06, 0.03) * mm, "radius": 1 * mm});
            skCircle(sketch, "E7.11.13.0", {"center": v(-4.06, -3.52) * mm, "radius": 1 * mm});
            skCircle(sketch, "E7.11.14.0", {"center": v(-4.06, -7.08) * mm, "radius": 1 * mm});
            skCircle(sketch, "E7.11.15.0", {"center": v(-4.06, -10.63) * mm, "radius": 1 * mm});
            skCircle(sketch, "E7.11.16.0", {"center": v(-4.06, -14.19) * mm, "radius": 1 * mm});
            skCircle(sketch, "E7.11.17.0", {"center": v(-4.06, -17.75) * mm, "radius": 1 * mm});
            skCircle(sketch, "E7.11.18.0", {"center": v(-4.06, -21.3) * mm, "radius": 1 * mm});
            skCircle(sketch, "E7.11.19.0", {"center": v(-4.06, -24.86) * mm, "radius": 1 * mm});
            skCircle(sketch, "E7.11.20.0", {"center": v(-4.06, -28.41) * mm, "radius": 1 * mm});
            skCircle(sketch, "E7.11.21.0", {"center": v(-4.06, -31.97) * mm, "radius": 1 * mm});
            skCircle(sketch, "E7.11.22.0", {"center": v(-4.06, -35.53) * mm, "radius": 1 * mm});
            skCircle(sketch, "E7.11.23.0", {"center": v(-4.06, -39.08) * mm, "radius": 1 * mm});
            skCircle(sketch, "E7.11.24.0", {"center": v(-4.06, -42.64) * mm, "radius": 1 * mm});
            skCircle(sketch, "E7.12.0.0", {"center": v(-0.5, 42.7) * mm, "radius": 1 * mm});
            skCircle(sketch, "E7.12.1.0", {"center": v(-0.5, 39.15) * mm, "radius": 1 * mm});
            skCircle(sketch, "E7.12.2.0", {"center": v(-0.5, 35.6) * mm, "radius": 1 * mm});
            skCircle(sketch, "E7.12.3.0", {"center": v(-0.5, 32.04) * mm, "radius": 1 * mm});
            skCircle(sketch, "E7.12.4.0", {"center": v(-0.5, 28.48) * mm, "radius": 1 * mm});
            skCircle(sketch, "E7.12.5.0", {"center": v(-0.5, 24.93) * mm, "radius": 1 * mm});
            skCircle(sketch, "E7.12.6.0", {"center": v(-0.5, 21.37) * mm, "radius": 1 * mm});
            skCircle(sketch, "E7.12.7.0", {"center": v(-0.5, 17.81) * mm, "radius": 1 * mm});
            skCircle(sketch, "E7.12.8.0", {"center": v(-0.5, 14.26) * mm, "radius": 1 * mm});
            skCircle(sketch, "E7.12.9.0", {"center": v(-0.5, 10.7) * mm, "radius": 1 * mm});
            skCircle(sketch, "E7.12.10.0", {"center": v(-0.5, 7.15) * mm, "radius": 1 * mm});
            skCircle(sketch, "E7.12.11.0", {"center": v(-0.5, 3.6) * mm, "radius": 1 * mm});
            skCircle(sketch, "E7.12.12.0", {"center": v(-0.5, 0.03) * mm, "radius": 1 * mm});
            skCircle(sketch, "E7.12.13.0", {"center": v(-0.5, -3.52) * mm, "radius": 1 * mm});
            skCircle(sketch, "E7.12.14.0", {"center": v(-0.5, -7.08) * mm, "radius": 1 * mm});
            skCircle(sketch, "E7.12.15.0", {"center": v(-0.5, -10.63) * mm, "radius": 1 * mm});
            skCircle(sketch, "E7.12.16.0", {"center": v(-0.5, -14.19) * mm, "radius": 1 * mm});
            skCircle(sketch, "E7.12.17.0", {"center": v(-0.5, -17.75) * mm, "radius": 1 * mm});
            skCircle(sketch, "E7.12.18.0", {"center": v(-0.5, -21.3) * mm, "radius": 1 * mm});
            skCircle(sketch, "E7.12.19.0", {"center": v(-0.5, -24.86) * mm, "radius": 1 * mm});
            skCircle(sketch, "E7.12.20.0", {"center": v(-0.5, -28.41) * mm, "radius": 1 * mm});
            skCircle(sketch, "E7.12.21.0", {"center": v(-0.5, -31.97) * mm, "radius": 1 * mm});
            skCircle(sketch, "E7.12.22.0", {"center": v(-0.5, -35.53) * mm, "radius": 1 * mm});
            skCircle(sketch, "E7.12.23.0", {"center": v(-0.5, -39.08) * mm, "radius": 1 * mm});
            skCircle(sketch, "E7.12.24.0", {"center": v(-0.5, -42.64) * mm, "radius": 1 * mm});
            skCircle(sketch, "E7.13.0.0", {"center": v(3.05, 42.7) * mm, "radius": 1 * mm});
            skCircle(sketch, "E7.13.1.0", {"center": v(3.05, 39.15) * mm, "radius": 1 * mm});
            skCircle(sketch, "E7.13.2.0", {"center": v(3.05, 35.6) * mm, "radius": 1 * mm});
            skCircle(sketch, "E7.13.3.0", {"center": v(3.05, 32.04) * mm, "radius": 1 * mm});
            skCircle(sketch, "E7.13.4.0", {"center": v(3.05, 28.48) * mm, "radius": 1 * mm});
            skCircle(sketch, "E7.13.5.0", {"center": v(3.05, 24.93) * mm, "radius": 1 * mm});
            skCircle(sketch, "E7.13.6.0", {"center": v(3.05, 21.37) * mm, "radius": 1 * mm});
            skCircle(sketch, "E7.13.7.0", {"center": v(3.05, 17.81) * mm, "radius": 1 * mm});
            skCircle(sketch, "E7.13.8.0", {"center": v(3.05, 14.26) * mm, "radius": 1 * mm});
            skCircle(sketch, "E7.13.9.0", {"center": v(3.05, 10.7) * mm, "radius": 1 * mm});
            skCircle(sketch, "E7.13.10.0", {"center": v(3.05, 7.15) * mm, "radius": 1 * mm});
            skCircle(sketch, "E7.13.11.0", {"center": v(3.05, 3.6) * mm, "radius": 1 * mm});
            skCircle(sketch, "E7.13.12.0", {"center": v(3.05, 0.03) * mm, "radius": 1 * mm});
            skCircle(sketch, "E7.13.13.0", {"center": v(3.05, -3.52) * mm, "radius": 1 * mm});
            skCircle(sketch, "E7.13.14.0", {"center": v(3.05, -7.08) * mm, "radius": 1 * mm});
            skCircle(sketch, "E7.13.15.0", {"center": v(3.05, -10.63) * mm, "radius": 1 * mm});
            skCircle(sketch, "E7.13.16.0", {"center": v(3.05, -14.19) * mm, "radius": 1 * mm});
            skCircle(sketch, "E7.13.17.0", {"center": v(3.05, -17.75) * mm, "radius": 1 * mm});
            skCircle(sketch, "E7.13.18.0", {"center": v(3.05, -21.3) * mm, "radius": 1 * mm});
            skCircle(sketch, "E7.13.19.0", {"center": v(3.05, -24.86) * mm, "radius": 1 * mm});
            skCircle(sketch, "E7.13.20.0", {"center": v(3.05, -28.41) * mm, "radius": 1 * mm});
            skCircle(sketch, "E7.13.21.0", {"center": v(3.05, -31.97) * mm, "radius": 1 * mm});
            skCircle(sketch, "E7.13.22.0", {"center": v(3.05, -35.53) * mm, "radius": 1 * mm});
            skCircle(sketch, "E7.13.23.0", {"center": v(3.05, -39.08) * mm, "radius": 1 * mm});
            skCircle(sketch, "E7.13.24.0", {"center": v(3.05, -42.64) * mm, "radius": 1 * mm});
            skCircle(sketch, "E7.14.0.0", {"center": v(6.6, 42.7) * mm, "radius": 1 * mm});
            skCircle(sketch, "E7.14.1.0", {"center": v(6.6, 39.15) * mm, "radius": 1 * mm});
            skCircle(sketch, "E7.14.2.0", {"center": v(6.6, 35.6) * mm, "radius": 1 * mm});
            skCircle(sketch, "E7.14.3.0", {"center": v(6.6, 32.04) * mm, "radius": 1 * mm});
            skCircle(sketch, "E7.14.4.0", {"center": v(6.6, 28.48) * mm, "radius": 1 * mm});
            skCircle(sketch, "E7.14.5.0", {"center": v(6.6, 24.93) * mm, "radius": 1 * mm});
            skCircle(sketch, "E7.14.6.0", {"center": v(6.6, 21.37) * mm, "radius": 1 * mm});
            skCircle(sketch, "E7.14.7.0", {"center": v(6.6, 17.81) * mm, "radius": 1 * mm});
            skCircle(sketch, "E7.14.8.0", {"center": v(6.6, 14.26) * mm, "radius": 1 * mm});
            skCircle(sketch, "E7.14.9.0", {"center": v(6.6, 10.7) * mm, "radius": 1 * mm});
            skCircle(sketch, "E7.14.10.0", {"center": v(6.6, 7.15) * mm, "radius": 1 * mm});
            skCircle(sketch, "E7.14.11.0", {"center": v(6.6, 3.6) * mm, "radius": 1 * mm});
            skCircle(sketch, "E7.14.12.0", {"center": v(6.6, 0.03) * mm, "radius": 1 * mm});
            skCircle(sketch, "E7.14.13.0", {"center": v(6.6, -3.52) * mm, "radius": 1 * mm});
            skCircle(sketch, "E7.14.14.0", {"center": v(6.6, -7.08) * mm, "radius": 1 * mm});
            skCircle(sketch, "E7.14.15.0", {"center": v(6.6, -10.63) * mm, "radius": 1 * mm});
            skCircle(sketch, "E7.14.16.0", {"center": v(6.6, -14.19) * mm, "radius": 1 * mm});
            skCircle(sketch, "E7.14.17.0", {"center": v(6.6, -17.75) * mm, "radius": 1 * mm});
            skCircle(sketch, "E7.14.18.0", {"center": v(6.6, -21.3) * mm, "radius": 1 * mm});
            skCircle(sketch, "E7.14.19.0", {"center": v(6.6, -24.86) * mm, "radius": 1 * mm});
            skCircle(sketch, "E7.14.20.0", {"center": v(6.6, -28.41) * mm, "radius": 1 * mm});
            skCircle(sketch, "E7.14.21.0", {"center": v(6.6, -31.97) * mm, "radius": 1 * mm});
            skCircle(sketch, "E7.14.22.0", {"center": v(6.6, -35.53) * mm, "radius": 1 * mm});
            skCircle(sketch, "E7.14.23.0", {"center": v(6.6, -39.08) * mm, "radius": 1 * mm});
            skCircle(sketch, "E7.14.24.0", {"center": v(6.6, -42.64) * mm, "radius": 1 * mm});
            skCircle(sketch, "E7.15.0.0", {"center": v(10.16, 42.7) * mm, "radius": 1 * mm});
            skCircle(sketch, "E7.15.1.0", {"center": v(10.16, 39.15) * mm, "radius": 1 * mm});
            skCircle(sketch, "E7.15.2.0", {"center": v(10.16, 35.6) * mm, "radius": 1 * mm});
            skCircle(sketch, "E7.15.3.0", {"center": v(10.16, 32.04) * mm, "radius": 1 * mm});
            skCircle(sketch, "E7.15.4.0", {"center": v(10.16, 28.48) * mm, "radius": 1 * mm});
            skCircle(sketch, "E7.15.5.0", {"center": v(10.16, 24.93) * mm, "radius": 1 * mm});
            skCircle(sketch, "E7.15.6.0", {"center": v(10.16, 21.37) * mm, "radius": 1 * mm});
            skCircle(sketch, "E7.15.7.0", {"center": v(10.16, 17.81) * mm, "radius": 1 * mm});
            skCircle(sketch, "E7.15.8.0", {"center": v(10.16, 14.26) * mm, "radius": 1 * mm});
            skCircle(sketch, "E7.15.9.0", {"center": v(10.16, 10.7) * mm, "radius": 1 * mm});
            skCircle(sketch, "E7.15.10.0", {"center": v(10.16, 7.15) * mm, "radius": 1 * mm});
            skCircle(sketch, "E7.15.11.0", {"center": v(10.16, 3.6) * mm, "radius": 1 * mm});
            skCircle(sketch, "E7.15.12.0", {"center": v(10.16, 0.03) * mm, "radius": 1 * mm});
            skCircle(sketch, "E7.15.13.0", {"center": v(10.16, -3.52) * mm, "radius": 1 * mm});
            skCircle(sketch, "E7.15.14.0", {"center": v(10.16, -7.08) * mm, "radius": 1 * mm});
            skCircle(sketch, "E7.15.15.0", {"center": v(10.16, -10.63) * mm, "radius": 1 * mm});
            skCircle(sketch, "E7.15.16.0", {"center": v(10.16, -14.19) * mm, "radius": 1 * mm});
            skCircle(sketch, "E7.15.17.0", {"center": v(10.16, -17.75) * mm, "radius": 1 * mm});
            skCircle(sketch, "E7.15.18.0", {"center": v(10.16, -21.3) * mm, "radius": 1 * mm});
            skCircle(sketch, "E7.15.19.0", {"center": v(10.16, -24.86) * mm, "radius": 1 * mm});
            skCircle(sketch, "E7.15.20.0", {"center": v(10.16, -28.41) * mm, "radius": 1 * mm});
            skCircle(sketch, "E7.15.21.0", {"center": v(10.16, -31.97) * mm, "radius": 1 * mm});
            skCircle(sketch, "E7.15.22.0", {"center": v(10.16, -35.53) * mm, "radius": 1 * mm});
            skCircle(sketch, "E7.15.23.0", {"center": v(10.16, -39.08) * mm, "radius": 1 * mm});
            skCircle(sketch, "E7.15.24.0", {"center": v(10.16, -42.64) * mm, "radius": 1 * mm});
            skCircle(sketch, "E7.16.0.0", {"center": v(13.72, 42.7) * mm, "radius": 1 * mm});
            skCircle(sketch, "E7.16.1.0", {"center": v(13.72, 39.15) * mm, "radius": 1 * mm});
            skCircle(sketch, "E7.16.2.0", {"center": v(13.72, 35.6) * mm, "radius": 1 * mm});
            skCircle(sketch, "E7.16.3.0", {"center": v(13.72, 32.04) * mm, "radius": 1 * mm});
            skCircle(sketch, "E7.16.4.0", {"center": v(13.72, 28.48) * mm, "radius": 1 * mm});
            skCircle(sketch, "E7.16.5.0", {"center": v(13.72, 24.93) * mm, "radius": 1 * mm});
            skCircle(sketch, "E7.16.6.0", {"center": v(13.72, 21.37) * mm, "radius": 1 * mm});
            skCircle(sketch, "E7.16.7.0", {"center": v(13.72, 17.81) * mm, "radius": 1 * mm});
            skCircle(sketch, "E7.16.8.0", {"center": v(13.72, 14.26) * mm, "radius": 1 * mm});
            skCircle(sketch, "E7.16.9.0", {"center": v(13.72, 10.7) * mm, "radius": 1 * mm});
            skCircle(sketch, "E7.16.10.0", {"center": v(13.72, 7.15) * mm, "radius": 1 * mm});
            skCircle(sketch, "E7.16.11.0", {"center": v(13.72, 3.6) * mm, "radius": 1 * mm});
            skCircle(sketch, "E7.16.12.0", {"center": v(13.72, 0.03) * mm, "radius": 1 * mm});
            skCircle(sketch, "E7.16.13.0", {"center": v(13.72, -3.52) * mm, "radius": 1 * mm});
            skCircle(sketch, "E7.16.14.0", {"center": v(13.72, -7.08) * mm, "radius": 1 * mm});
            skCircle(sketch, "E7.16.15.0", {"center": v(13.72, -10.63) * mm, "radius": 1 * mm});
            skCircle(sketch, "E7.16.16.0", {"center": v(13.72, -14.19) * mm, "radius": 1 * mm});
            skCircle(sketch, "E7.16.17.0", {"center": v(13.72, -17.75) * mm, "radius": 1 * mm});
            skCircle(sketch, "E7.16.18.0", {"center": v(13.72, -21.3) * mm, "radius": 1 * mm});
            skCircle(sketch, "E7.16.19.0", {"center": v(13.72, -24.86) * mm, "radius": 1 * mm});
            skCircle(sketch, "E7.16.20.0", {"center": v(13.72, -28.41) * mm, "radius": 1 * mm});
            skCircle(sketch, "E7.16.21.0", {"center": v(13.72, -31.97) * mm, "radius": 1 * mm});
            skCircle(sketch, "E7.16.22.0", {"center": v(13.72, -35.53) * mm, "radius": 1 * mm});
            skCircle(sketch, "E7.16.23.0", {"center": v(13.72, -39.08) * mm, "radius": 1 * mm});
            skCircle(sketch, "E7.16.24.0", {"center": v(13.72, -42.64) * mm, "radius": 1 * mm});
            skCircle(sketch, "E7.17.0.0", {"center": v(17.27, 42.7) * mm, "radius": 1 * mm});
            skCircle(sketch, "E7.17.1.0", {"center": v(17.27, 39.15) * mm, "radius": 1 * mm});
            skCircle(sketch, "E7.17.2.0", {"center": v(17.27, 35.6) * mm, "radius": 1 * mm});
            skCircle(sketch, "E7.17.3.0", {"center": v(17.27, 32.04) * mm, "radius": 1 * mm});
            skCircle(sketch, "E7.17.4.0", {"center": v(17.27, 28.48) * mm, "radius": 1 * mm});
            skCircle(sketch, "E7.17.5.0", {"center": v(17.27, 24.93) * mm, "radius": 1 * mm});
            skCircle(sketch, "E7.17.6.0", {"center": v(17.27, 21.37) * mm, "radius": 1 * mm});
            skCircle(sketch, "E7.17.7.0", {"center": v(17.27, 17.81) * mm, "radius": 1 * mm});
            skCircle(sketch, "E7.17.8.0", {"center": v(17.27, 14.26) * mm, "radius": 1 * mm});
            skCircle(sketch, "E7.17.9.0", {"center": v(17.27, 10.7) * mm, "radius": 1 * mm});
            skCircle(sketch, "E7.17.10.0", {"center": v(17.27, 7.15) * mm, "radius": 1 * mm});
            skCircle(sketch, "E7.17.11.0", {"center": v(17.27, 3.6) * mm, "radius": 1 * mm});
            skCircle(sketch, "E7.17.12.0", {"center": v(17.27, 0.03) * mm, "radius": 1 * mm});
            skCircle(sketch, "E7.17.13.0", {"center": v(17.27, -3.52) * mm, "radius": 1 * mm});
            skCircle(sketch, "E7.17.14.0", {"center": v(17.27, -7.08) * mm, "radius": 1 * mm});
            skCircle(sketch, "E7.17.15.0", {"center": v(17.27, -10.63) * mm, "radius": 1 * mm});
            skCircle(sketch, "E7.17.16.0", {"center": v(17.27, -14.19) * mm, "radius": 1 * mm});
            skCircle(sketch, "E7.17.17.0", {"center": v(17.27, -17.75) * mm, "radius": 1 * mm});
            skCircle(sketch, "E7.17.18.0", {"center": v(17.27, -21.3) * mm, "radius": 1 * mm});
            skCircle(sketch, "E7.17.19.0", {"center": v(17.27, -24.86) * mm, "radius": 1 * mm});
            skCircle(sketch, "E7.17.20.0", {"center": v(17.27, -28.41) * mm, "radius": 1 * mm});
            skCircle(sketch, "E7.17.21.0", {"center": v(17.27, -31.97) * mm, "radius": 1 * mm});
            skCircle(sketch, "E7.17.22.0", {"center": v(17.27, -35.53) * mm, "radius": 1 * mm});
            skCircle(sketch, "E7.17.23.0", {"center": v(17.27, -39.08) * mm, "radius": 1 * mm});
            skCircle(sketch, "E7.17.24.0", {"center": v(17.27, -42.64) * mm, "radius": 1 * mm});
            skCircle(sketch, "E7.18.0.0", {"center": v(20.83, 42.7) * mm, "radius": 1 * mm});
            skCircle(sketch, "E7.18.1.0", {"center": v(20.83, 39.15) * mm, "radius": 1 * mm});
            skCircle(sketch, "E7.18.2.0", {"center": v(20.83, 35.6) * mm, "radius": 1 * mm});
            skCircle(sketch, "E7.18.3.0", {"center": v(20.83, 32.04) * mm, "radius": 1 * mm});
            skCircle(sketch, "E7.18.4.0", {"center": v(20.83, 28.48) * mm, "radius": 1 * mm});
            skCircle(sketch, "E7.18.5.0", {"center": v(20.83, 24.93) * mm, "radius": 1 * mm});
            skCircle(sketch, "E7.18.6.0", {"center": v(20.83, 21.37) * mm, "radius": 1 * mm});
            skCircle(sketch, "E7.18.7.0", {"center": v(20.83, 17.81) * mm, "radius": 1 * mm});
            skCircle(sketch, "E7.18.8.0", {"center": v(20.83, 14.26) * mm, "radius": 1 * mm});
            skCircle(sketch, "E7.18.9.0", {"center": v(20.83, 10.7) * mm, "radius": 1 * mm});
            skCircle(sketch, "E7.18.10.0", {"center": v(20.83, 7.15) * mm, "radius": 1 * mm});
            skCircle(sketch, "E7.18.11.0", {"center": v(20.83, 3.6) * mm, "radius": 1 * mm});
            skCircle(sketch, "E7.18.12.0", {"center": v(20.83, 0.03) * mm, "radius": 1 * mm});
            skCircle(sketch, "E7.18.13.0", {"center": v(20.83, -3.52) * mm, "radius": 1 * mm});
            skCircle(sketch, "E7.18.14.0", {"center": v(20.83, -7.08) * mm, "radius": 1 * mm});
            skCircle(sketch, "E7.18.15.0", {"center": v(20.83, -10.63) * mm, "radius": 1 * mm});
            skCircle(sketch, "E7.18.16.0", {"center": v(20.83, -14.19) * mm, "radius": 1 * mm});
            skCircle(sketch, "E7.18.17.0", {"center": v(20.83, -17.75) * mm, "radius": 1 * mm});
            skCircle(sketch, "E7.18.18.0", {"center": v(20.83, -21.3) * mm, "radius": 1 * mm});
            skCircle(sketch, "E7.18.19.0", {"center": v(20.83, -24.86) * mm, "radius": 1 * mm});
            skCircle(sketch, "E7.18.20.0", {"center": v(20.83, -28.41) * mm, "radius": 1 * mm});
            skCircle(sketch, "E7.18.21.0", {"center": v(20.83, -31.97) * mm, "radius": 1 * mm});
            skCircle(sketch, "E7.18.22.0", {"center": v(20.83, -35.53) * mm, "radius": 1 * mm});
            skCircle(sketch, "E7.18.23.0", {"center": v(20.83, -39.08) * mm, "radius": 1 * mm});
            skCircle(sketch, "E7.18.24.0", {"center": v(20.83, -42.64) * mm, "radius": 1 * mm});
            skCircle(sketch, "E7.19.0.0", {"center": v(24.38, 42.7) * mm, "radius": 1 * mm});
            skCircle(sketch, "E7.19.1.0", {"center": v(24.38, 39.15) * mm, "radius": 1 * mm});
            skCircle(sketch, "E7.19.2.0", {"center": v(24.38, 35.6) * mm, "radius": 1 * mm});
            skCircle(sketch, "E7.19.3.0", {"center": v(24.38, 32.04) * mm, "radius": 1 * mm});
            skCircle(sketch, "E7.19.4.0", {"center": v(24.38, 28.48) * mm, "radius": 1 * mm});
            skCircle(sketch, "E7.19.5.0", {"center": v(24.38, 24.93) * mm, "radius": 1 * mm});
            skCircle(sketch, "E7.19.6.0", {"center": v(24.38, 21.37) * mm, "radius": 1 * mm});
            skCircle(sketch, "E7.19.7.0", {"center": v(24.38, 17.81) * mm, "radius": 1 * mm});
            skCircle(sketch, "E7.19.8.0", {"center": v(24.38, 14.26) * mm, "radius": 1 * mm});
            skCircle(sketch, "E7.19.9.0", {"center": v(24.38, 10.7) * mm, "radius": 1 * mm});
            skCircle(sketch, "E7.19.10.0", {"center": v(24.38, 7.15) * mm, "radius": 1 * mm});
            skCircle(sketch, "E7.19.11.0", {"center": v(24.38, 3.6) * mm, "radius": 1 * mm});
            skCircle(sketch, "E7.19.12.0", {"center": v(24.38, 0.03) * mm, "radius": 1 * mm});
            skCircle(sketch, "E7.19.13.0", {"center": v(24.38, -3.52) * mm, "radius": 1 * mm});
            skCircle(sketch, "E7.19.14.0", {"center": v(24.38, -7.08) * mm, "radius": 1 * mm});
            skCircle(sketch, "E7.19.15.0", {"center": v(24.38, -10.63) * mm, "radius": 1 * mm});
            skCircle(sketch, "E7.19.16.0", {"center": v(24.38, -14.19) * mm, "radius": 1 * mm});
            skCircle(sketch, "E7.19.17.0", {"center": v(24.38, -17.75) * mm, "radius": 1 * mm});
            skCircle(sketch, "E7.19.18.0", {"center": v(24.38, -21.3) * mm, "radius": 1 * mm});
            skCircle(sketch, "E7.19.19.0", {"center": v(24.38, -24.86) * mm, "radius": 1 * mm});
            skCircle(sketch, "E7.19.20.0", {"center": v(24.38, -28.41) * mm, "radius": 1 * mm});
            skCircle(sketch, "E7.19.21.0", {"center": v(24.38, -31.97) * mm, "radius": 1 * mm});
            skCircle(sketch, "E7.19.22.0", {"center": v(24.38, -35.53) * mm, "radius": 1 * mm});
            skCircle(sketch, "E7.19.23.0", {"center": v(24.38, -39.08) * mm, "radius": 1 * mm});
            skCircle(sketch, "E7.19.24.0", {"center": v(24.38, -42.64) * mm, "radius": 1 * mm});
            skCircle(sketch, "E7.20.0.0", {"center": v(27.94, 42.7) * mm, "radius": 1 * mm});
            skCircle(sketch, "E7.20.1.0", {"center": v(27.94, 39.15) * mm, "radius": 1 * mm});
            skCircle(sketch, "E7.20.2.0", {"center": v(27.94, 35.6) * mm, "radius": 1 * mm});
            skCircle(sketch, "E7.20.3.0", {"center": v(27.94, 32.04) * mm, "radius": 1 * mm});
            skCircle(sketch, "E7.20.4.0", {"center": v(27.94, 28.48) * mm, "radius": 1 * mm});
            skCircle(sketch, "E7.20.5.0", {"center": v(27.94, 24.93) * mm, "radius": 1 * mm});
            skCircle(sketch, "E7.20.6.0", {"center": v(27.94, 21.37) * mm, "radius": 1 * mm});
            skCircle(sketch, "E7.20.7.0", {"center": v(27.94, 17.81) * mm, "radius": 1 * mm});
            skCircle(sketch, "E7.20.8.0", {"center": v(27.94, 14.26) * mm, "radius": 1 * mm});
            skCircle(sketch, "E7.20.9.0", {"center": v(27.94, 10.7) * mm, "radius": 1 * mm});
            skCircle(sketch, "E7.20.10.0", {"center": v(27.94, 7.15) * mm, "radius": 1 * mm});
            skCircle(sketch, "E7.20.11.0", {"center": v(27.94, 3.6) * mm, "radius": 1 * mm});
            skCircle(sketch, "E7.20.12.0", {"center": v(27.94, 0.03) * mm, "radius": 1 * mm});
            skCircle(sketch, "E7.20.13.0", {"center": v(27.94, -3.52) * mm, "radius": 1 * mm});
            skCircle(sketch, "E7.20.14.0", {"center": v(27.94, -7.08) * mm, "radius": 1 * mm});
            skCircle(sketch, "E7.20.15.0", {"center": v(27.94, -10.63) * mm, "radius": 1 * mm});
            skCircle(sketch, "E7.20.16.0", {"center": v(27.94, -14.19) * mm, "radius": 1 * mm});
            skCircle(sketch, "E7.20.17.0", {"center": v(27.94, -17.75) * mm, "radius": 1 * mm});
            skCircle(sketch, "E7.20.18.0", {"center": v(27.94, -21.3) * mm, "radius": 1 * mm});
            skCircle(sketch, "E7.20.19.0", {"center": v(27.94, -24.86) * mm, "radius": 1 * mm});
            skCircle(sketch, "E7.20.20.0", {"center": v(27.94, -28.41) * mm, "radius": 1 * mm});
            skCircle(sketch, "E7.20.21.0", {"center": v(27.94, -31.97) * mm, "radius": 1 * mm});
            skCircle(sketch, "E7.20.22.0", {"center": v(27.94, -35.53) * mm, "radius": 1 * mm});
            skCircle(sketch, "E7.20.23.0", {"center": v(27.94, -39.08) * mm, "radius": 1 * mm});
            skCircle(sketch, "E7.20.24.0", {"center": v(27.94, -42.64) * mm, "radius": 1 * mm});
            skCircle(sketch, "E7.21.0.0", {"center": v(31.5, 42.7) * mm, "radius": 1 * mm});
            skCircle(sketch, "E7.21.1.0", {"center": v(31.5, 39.15) * mm, "radius": 1 * mm});
            skCircle(sketch, "E7.21.2.0", {"center": v(31.5, 35.6) * mm, "radius": 1 * mm});
            skCircle(sketch, "E7.21.3.0", {"center": v(31.5, 32.04) * mm, "radius": 1 * mm});
            skCircle(sketch, "E7.21.4.0", {"center": v(31.5, 28.48) * mm, "radius": 1 * mm});
            skCircle(sketch, "E7.21.5.0", {"center": v(31.5, 24.93) * mm, "radius": 1 * mm});
            skCircle(sketch, "E7.21.6.0", {"center": v(31.5, 21.37) * mm, "radius": 1 * mm});
            skCircle(sketch, "E7.21.7.0", {"center": v(31.5, 17.81) * mm, "radius": 1 * mm});
            skCircle(sketch, "E7.21.8.0", {"center": v(31.5, 14.26) * mm, "radius": 1 * mm});
            skCircle(sketch, "E7.21.9.0", {"center": v(31.5, 10.7) * mm, "radius": 1 * mm});
            skCircle(sketch, "E7.21.10.0", {"center": v(31.5, 7.15) * mm, "radius": 1 * mm});
            skCircle(sketch, "E7.21.11.0", {"center": v(31.5, 3.6) * mm, "radius": 1 * mm});
            skCircle(sketch, "E7.21.12.0", {"center": v(31.5, 0.03) * mm, "radius": 1 * mm});
            skCircle(sketch, "E7.21.13.0", {"center": v(31.5, -3.52) * mm, "radius": 1 * mm});
            skCircle(sketch, "E7.21.14.0", {"center": v(31.5, -7.08) * mm, "radius": 1 * mm});
            skCircle(sketch, "E7.21.15.0", {"center": v(31.5, -10.63) * mm, "radius": 1 * mm});
            skCircle(sketch, "E7.21.16.0", {"center": v(31.5, -14.19) * mm, "radius": 1 * mm});
            skCircle(sketch, "E7.21.17.0", {"center": v(31.5, -17.75) * mm, "radius": 1 * mm});
            skCircle(sketch, "E7.21.18.0", {"center": v(31.5, -21.3) * mm, "radius": 1 * mm});
            skCircle(sketch, "E7.21.19.0", {"center": v(31.5, -24.86) * mm, "radius": 1 * mm});
            skCircle(sketch, "E7.21.20.0", {"center": v(31.5, -28.41) * mm, "radius": 1 * mm});
            skCircle(sketch, "E7.21.21.0", {"center": v(31.5, -31.97) * mm, "radius": 1 * mm});
            skCircle(sketch, "E7.21.22.0", {"center": v(31.5, -35.53) * mm, "radius": 1 * mm});
            skCircle(sketch, "E7.21.23.0", {"center": v(31.5, -39.08) * mm, "radius": 1 * mm});
            skCircle(sketch, "E7.21.24.0", {"center": v(31.5, -42.64) * mm, "radius": 1 * mm});
            skCircle(sketch, "E7.22.0.0", {"center": v(35.05, 42.7) * mm, "radius": 1 * mm});
            skCircle(sketch, "E7.22.1.0", {"center": v(35.05, 39.15) * mm, "radius": 1 * mm});
            skCircle(sketch, "E7.22.2.0", {"center": v(35.05, 35.6) * mm, "radius": 1 * mm});
            skCircle(sketch, "E7.22.3.0", {"center": v(35.05, 32.04) * mm, "radius": 1 * mm});
            skCircle(sketch, "E7.22.4.0", {"center": v(35.05, 28.48) * mm, "radius": 1 * mm});
            skCircle(sketch, "E7.22.5.0", {"center": v(35.05, 24.93) * mm, "radius": 1 * mm});
            skCircle(sketch, "E7.22.6.0", {"center": v(35.05, 21.37) * mm, "radius": 1 * mm});
            skCircle(sketch, "E7.22.7.0", {"center": v(35.05, 17.81) * mm, "radius": 1 * mm});
            skCircle(sketch, "E7.22.8.0", {"center": v(35.05, 14.26) * mm, "radius": 1 * mm});
            skCircle(sketch, "E7.22.9.0", {"center": v(35.05, 10.7) * mm, "radius": 1 * mm});
            skCircle(sketch, "E7.22.10.0", {"center": v(35.05, 7.15) * mm, "radius": 1 * mm});
            skCircle(sketch, "E7.22.11.0", {"center": v(35.05, 3.6) * mm, "radius": 1 * mm});
            skCircle(sketch, "E7.22.12.0", {"center": v(35.05, 0.03) * mm, "radius": 1 * mm});
            skCircle(sketch, "E7.22.13.0", {"center": v(35.05, -3.52) * mm, "radius": 1 * mm});
            skCircle(sketch, "E7.22.14.0", {"center": v(35.05, -7.08) * mm, "radius": 1 * mm});
            skCircle(sketch, "E7.22.15.0", {"center": v(35.05, -10.63) * mm, "radius": 1 * mm});
            skCircle(sketch, "E7.22.16.0", {"center": v(35.05, -14.19) * mm, "radius": 1 * mm});
            skCircle(sketch, "E7.22.17.0", {"center": v(35.05, -17.75) * mm, "radius": 1 * mm});
            skCircle(sketch, "E7.22.18.0", {"center": v(35.05, -21.3) * mm, "radius": 1 * mm});
            skCircle(sketch, "E7.22.19.0", {"center": v(35.05, -24.86) * mm, "radius": 1 * mm});
            skCircle(sketch, "E7.22.20.0", {"center": v(35.05, -28.41) * mm, "radius": 1 * mm});
            skCircle(sketch, "E7.22.21.0", {"center": v(35.05, -31.97) * mm, "radius": 1 * mm});
            skCircle(sketch, "E7.22.22.0", {"center": v(35.05, -35.53) * mm, "radius": 1 * mm});
            skCircle(sketch, "E7.22.23.0", {"center": v(35.05, -39.08) * mm, "radius": 1 * mm});
            skCircle(sketch, "E7.22.24.0", {"center": v(35.05, -42.64) * mm, "radius": 1 * mm});
            skCircle(sketch, "E7.23.0.0", {"center": v(38.6, 42.7) * mm, "radius": 1 * mm});
            skCircle(sketch, "E7.23.1.0", {"center": v(38.6, 39.15) * mm, "radius": 1 * mm});
            skCircle(sketch, "E7.23.2.0", {"center": v(38.6, 35.6) * mm, "radius": 1 * mm});
            skCircle(sketch, "E7.23.3.0", {"center": v(38.6, 32.04) * mm, "radius": 1 * mm});
            skCircle(sketch, "E7.23.4.0", {"center": v(38.6, 28.48) * mm, "radius": 1 * mm});
            skCircle(sketch, "E7.23.5.0", {"center": v(38.6, 24.93) * mm, "radius": 1 * mm});
            skCircle(sketch, "E7.23.6.0", {"center": v(38.6, 21.37) * mm, "radius": 1 * mm});
            skCircle(sketch, "E7.23.7.0", {"center": v(38.6, 17.81) * mm, "radius": 1 * mm});
            skCircle(sketch, "E7.23.8.0", {"center": v(38.6, 14.26) * mm, "radius": 1 * mm});
            skCircle(sketch, "E7.23.9.0", {"center": v(38.6, 10.7) * mm, "radius": 1 * mm});
            skCircle(sketch, "E7.23.10.0", {"center": v(38.6, 7.15) * mm, "radius": 1 * mm});
            skCircle(sketch, "E7.23.11.0", {"center": v(38.6, 3.6) * mm, "radius": 1 * mm});
            skCircle(sketch, "E7.23.12.0", {"center": v(38.6, 0.03) * mm, "radius": 1 * mm});
            skCircle(sketch, "E7.23.13.0", {"center": v(38.6, -3.52) * mm, "radius": 1 * mm});
            skCircle(sketch, "E7.23.14.0", {"center": v(38.6, -7.08) * mm, "radius": 1 * mm});
            skCircle(sketch, "E7.23.15.0", {"center": v(38.6, -10.63) * mm, "radius": 1 * mm});
            skCircle(sketch, "E7.23.16.0", {"center": v(38.6, -14.19) * mm, "radius": 1 * mm});
            skCircle(sketch, "E7.23.17.0", {"center": v(38.6, -17.75) * mm, "radius": 1 * mm});
            skCircle(sketch, "E7.23.18.0", {"center": v(38.6, -21.3) * mm, "radius": 1 * mm});
            skCircle(sketch, "E7.23.19.0", {"center": v(38.6, -24.86) * mm, "radius": 1 * mm});
            skCircle(sketch, "E7.23.20.0", {"center": v(38.6, -28.41) * mm, "radius": 1 * mm});
            skCircle(sketch, "E7.23.21.0", {"center": v(38.6, -31.97) * mm, "radius": 1 * mm});
            skCircle(sketch, "E7.23.22.0", {"center": v(38.6, -35.53) * mm, "radius": 1 * mm});
            skCircle(sketch, "E7.23.23.0", {"center": v(38.6, -39.08) * mm, "radius": 1 * mm});
            skCircle(sketch, "E7.23.24.0", {"center": v(38.6, -42.64) * mm, "radius": 1 * mm});
            skCircle(sketch, "E7.24.0.0", {"center": v(42.16, 42.7) * mm, "radius": 1 * mm});
            skCircle(sketch, "E7.24.1.0", {"center": v(42.16, 39.15) * mm, "radius": 1 * mm});
            skCircle(sketch, "E7.24.2.0", {"center": v(42.16, 35.6) * mm, "radius": 1 * mm});
            skCircle(sketch, "E7.24.3.0", {"center": v(42.16, 32.04) * mm, "radius": 1 * mm});
            skCircle(sketch, "E7.24.4.0", {"center": v(42.16, 28.48) * mm, "radius": 1 * mm});
            skCircle(sketch, "E7.24.5.0", {"center": v(42.16, 24.93) * mm, "radius": 1 * mm});
            skCircle(sketch, "E7.24.6.0", {"center": v(42.16, 21.37) * mm, "radius": 1 * mm});
            skCircle(sketch, "E7.24.7.0", {"center": v(42.16, 17.81) * mm, "radius": 1 * mm});
            skCircle(sketch, "E7.24.8.0", {"center": v(42.16, 14.26) * mm, "radius": 1 * mm});
            skCircle(sketch, "E7.24.9.0", {"center": v(42.16, 10.7) * mm, "radius": 1 * mm});
            skCircle(sketch, "E7.24.10.0", {"center": v(42.16, 7.15) * mm, "radius": 1 * mm});
            skCircle(sketch, "E7.24.11.0", {"center": v(42.16, 3.6) * mm, "radius": 1 * mm});
            skCircle(sketch, "E7.24.12.0", {"center": v(42.16, 0.03) * mm, "radius": 1 * mm});
            skCircle(sketch, "E7.24.13.0", {"center": v(42.16, -3.52) * mm, "radius": 1 * mm});
            skCircle(sketch, "E7.24.14.0", {"center": v(42.16, -7.08) * mm, "radius": 1 * mm});
            skCircle(sketch, "E7.24.15.0", {"center": v(42.16, -10.63) * mm, "radius": 1 * mm});
            skCircle(sketch, "E7.24.16.0", {"center": v(42.16, -14.19) * mm, "radius": 1 * mm});
            skCircle(sketch, "E7.24.17.0", {"center": v(42.16, -17.75) * mm, "radius": 1 * mm});
            skCircle(sketch, "E7.24.18.0", {"center": v(42.16, -21.3) * mm, "radius": 1 * mm});
            skCircle(sketch, "E7.24.19.0", {"center": v(42.16, -24.86) * mm, "radius": 1 * mm});
            skCircle(sketch, "E7.24.20.0", {"center": v(42.16, -28.41) * mm, "radius": 1 * mm});
            skCircle(sketch, "E7.24.21.0", {"center": v(42.16, -31.97) * mm, "radius": 1 * mm});
            skCircle(sketch, "E7.24.22.0", {"center": v(42.16, -35.53) * mm, "radius": 1 * mm});
            skCircle(sketch, "E7.24.23.0", {"center": v(42.16, -39.08) * mm, "radius": 1 * mm});
            skCircle(sketch, "E7.24.24.0", {"center": v(42.16, -42.64) * mm, "radius": 1 * mm});
            skLineSegment(sketch, "E7.direction1", {"start": v(-43.18, 42.7) * mm, "end": v(-39.62, 42.7) * mm, "construction": true});
            skLineSegment(sketch, "E7.direction2", {"start": v(-43.18, 42.7) * mm, "end": v(-43.18, 39.15) * mm, "construction": true});
            skSolve(sketch);
        }
        {
            var Q0;
            Q0=makeQuery(id+"F4.imprint","IMPRINT",FACE,{"disambiguationData":[TD([[makeQuery(id+"F4.imprint","IMPRINT",EDGE,{"derivedFrom":sQuery(id+"F4.wireOp",EDGE,"E6")}),1.0]])]});
            var Q1;
            Q1=makeQuery(id+"F4.imprint","IMPRINT",FACE,{"disambiguationData":[TD([[makeQuery(id+"F4.imprint","IMPRINT",EDGE,{"derivedFrom":sQuery(id+"F4.wireOp",EDGE,"E7.13.10.0")}),1.0]])]});
            var Q2;
            Q2=makeQuery(id+"F4.imprint","IMPRINT",FACE,{"disambiguationData":[TD([[makeQuery(id+"F4.imprint","IMPRINT",EDGE,{"derivedFrom":sQuery(id+"F4.wireOp",EDGE,"E7.15.24.0")}),1.0]])]});
            var Q3;
            Q3=makeQuery(id+"F4.imprint","IMPRINT",FACE,{"disambiguationData":[TD([[makeQuery(id+"F4.imprint","IMPRINT",EDGE,{"derivedFrom":sQuery(id+"F4.wireOp",EDGE,"E7.17.22.0")}),1.0]])]});
            var Q4;
            Q4=makeQuery(id+"F4.imprint","IMPRINT",FACE,{"disambiguationData":[TD([[makeQuery(id+"F4.imprint","IMPRINT",EDGE,{"derivedFrom":sQuery(id+"F4.wireOp",EDGE,"E7.19.20.0")}),1.0]])]});
            var Q5;
            Q5=makeQuery(id+"F4.imprint","IMPRINT",FACE,{"disambiguationData":[TD([[makeQuery(id+"F4.imprint","IMPRINT",EDGE,{"derivedFrom":sQuery(id+"F4.wireOp",EDGE,"E7.13.24.0")}),1.0]])]});
            var Q6;
            Q6=makeQuery(id+"F4.imprint","IMPRINT",FACE,{"disambiguationData":[TD([[makeQuery(id+"F4.imprint","IMPRINT",EDGE,{"derivedFrom":sQuery(id+"F4.wireOp",EDGE,"E7.15.22.0")}),1.0]])]});
            var Q7;
            Q7=makeQuery(id+"F4.imprint","IMPRINT",FACE,{"disambiguationData":[TD([[makeQuery(id+"F4.imprint","IMPRINT",EDGE,{"derivedFrom":sQuery(id+"F4.wireOp",EDGE,"E7.17.20.0")}),1.0]])]});
            var Q8;
            Q8=makeQuery(id+"F4.imprint","IMPRINT",FACE,{"disambiguationData":[TD([[makeQuery(id+"F4.imprint","IMPRINT",EDGE,{"derivedFrom":sQuery(id+"F4.wireOp",EDGE,"E7.19.18.0")}),1.0]])]});
            var Q9;
            Q9=makeQuery(id+"F4.imprint","IMPRINT",FACE,{"disambiguationData":[TD([[makeQuery(id+"F4.imprint","IMPRINT",EDGE,{"derivedFrom":sQuery(id+"F4.wireOp",EDGE,"E7.24.5.0")}),1.0]])]});
            var Q10;
            Q10=makeQuery(id+"F4.imprint","IMPRINT",FACE,{"disambiguationData":[TD([[makeQuery(id+"F4.imprint","IMPRINT",EDGE,{"derivedFrom":sQuery(id+"F4.wireOp",EDGE,"E7.2.12.0")}),1.0]])]});
            var Q11;
            Q11=makeQuery(id+"F4.imprint","IMPRINT",FACE,{"disambiguationData":[TD([[makeQuery(id+"F4.imprint","IMPRINT",EDGE,{"derivedFrom":sQuery(id+"F4.wireOp",EDGE,"E7.4.10.0")}),1.0]])]});
            var Q12;
            Q12=makeQuery(id+"F4.imprint","IMPRINT",FACE,{"disambiguationData":[TD([[makeQuery(id+"F4.imprint","IMPRINT",EDGE,{"derivedFrom":sQuery(id+"F4.wireOp",EDGE,"E7.8.22.0")}),1.0]])]});
            var Q13;
            Q13=makeQuery(id+"F4.imprint","IMPRINT",FACE,{"disambiguationData":[TD([[makeQuery(id+"F4.imprint","IMPRINT",EDGE,{"derivedFrom":sQuery(id+"F4.wireOp",EDGE,"E7.6.24.0")}),1.0]])]});
            var Q14;
            Q14=makeQuery(id+"F4.imprint","IMPRINT",FACE,{"disambiguationData":[TD([[makeQuery(id+"F4.imprint","IMPRINT",EDGE,{"derivedFrom":sQuery(id+"F4.wireOp",EDGE,"E7.17.5.0")}),1.0]])]});
            var Q15;
            Q15=makeQuery(id+"F4.imprint","IMPRINT",FACE,{"disambiguationData":[TD([[makeQuery(id+"F4.imprint","IMPRINT",EDGE,{"derivedFrom":sQuery(id+"F4.wireOp",EDGE,"E7.19.3.0")}),1.0]])]});
            var Q16;
            Q16=makeQuery(id+"F4.imprint","IMPRINT",FACE,{"disambiguationData":[TD([[makeQuery(id+"F4.imprint","IMPRINT",EDGE,{"derivedFrom":sQuery(id+"F4.wireOp",EDGE,"E7.22.24.0")}),1.0]])]});
            var Q17;
            Q17=makeQuery(id+"F4.imprint","IMPRINT",FACE,{"disambiguationData":[TD([[makeQuery(id+"F4.imprint","IMPRINT",EDGE,{"derivedFrom":sQuery(id+"F4.wireOp",EDGE,"E7.24.22.0")}),1.0]])]});
            var Q18;
            Q18=makeQuery(id+"F4.imprint","IMPRINT",FACE,{"disambiguationData":[TD([[makeQuery(id+"F4.imprint","IMPRINT",EDGE,{"derivedFrom":sQuery(id+"F4.wireOp",EDGE,"E7.24.24.0")}),1.0]])]});
            var Q19;
            Q19=makeQuery(id+"F4.imprint","IMPRINT",FACE,{"disambiguationData":[TD([[makeQuery(id+"F4.imprint","IMPRINT",EDGE,{"derivedFrom":sQuery(id+"F4.wireOp",EDGE,"E7.0.16.0")}),1.0]])]});
            var Q20;
            Q20=makeQuery(id+"F4.imprint","IMPRINT",FACE,{"disambiguationData":[TD([[makeQuery(id+"F4.imprint","IMPRINT",EDGE,{"derivedFrom":sQuery(id+"F4.wireOp",EDGE,"E7.2.14.0")}),1.0]])]});
            var Q21;
            Q21=makeQuery(id+"F4.imprint","IMPRINT",FACE,{"disambiguationData":[TD([[makeQuery(id+"F4.imprint","IMPRINT",EDGE,{"derivedFrom":sQuery(id+"F4.wireOp",EDGE,"E7.4.12.0")}),1.0]])]});
            var Q22;
            Q22=makeQuery(id+"F4.imprint","IMPRINT",FACE,{"disambiguationData":[TD([[makeQuery(id+"F4.imprint","IMPRINT",EDGE,{"derivedFrom":sQuery(id+"F4.wireOp",EDGE,"E7.8.24.0")}),1.0]])]});
            var Q23;
            Q23=makeQuery(id+"F4.imprint","IMPRINT",FACE,{"disambiguationData":[TD([[makeQuery(id+"F4.imprint","IMPRINT",EDGE,{"derivedFrom":sQuery(id+"F4.wireOp",EDGE,"E7.19.22.0")}),1.0]])]});
            var Q24;
            Q24=makeQuery(id+"F4.imprint","IMPRINT",FACE,{"disambiguationData":[TD([[makeQuery(id+"F4.imprint","IMPRINT",EDGE,{"derivedFrom":sQuery(id+"F4.wireOp",EDGE,"E7.11.14.0")}),1.0]])]});
            var Q25;
            Q25=makeQuery(id+"F4.imprint","IMPRINT",FACE,{"disambiguationData":[TD([[makeQuery(id+"F4.imprint","IMPRINT",EDGE,{"derivedFrom":sQuery(id+"F4.wireOp",EDGE,"E7.15.10.0")}),1.0]])]});
            var Q26;
            Q26=makeQuery(id+"F4.imprint","IMPRINT",FACE,{"disambiguationData":[TD([[makeQuery(id+"F4.imprint","IMPRINT",EDGE,{"derivedFrom":sQuery(id+"F4.wireOp",EDGE,"E7.17.24.0")}),1.0]])]});
            var Q27;
            Q27=makeQuery(id+"F4.imprint","IMPRINT",FACE,{"disambiguationData":[TD([[makeQuery(id+"F4.imprint","IMPRINT",EDGE,{"derivedFrom":sQuery(id+"F4.wireOp",EDGE,"E7.0.18.0")}),1.0]])]});
            var Q28;
            Q28=makeQuery(id+"F4.imprint","IMPRINT",FACE,{"disambiguationData":[TD([[makeQuery(id+"F4.imprint","IMPRINT",EDGE,{"derivedFrom":sQuery(id+"F4.wireOp",EDGE,"E7.2.16.0")}),1.0]])]});
            var Q29;
            Q29=makeQuery(id+"F4.imprint","IMPRINT",FACE,{"disambiguationData":[TD([[makeQuery(id+"F4.imprint","IMPRINT",EDGE,{"derivedFrom":sQuery(id+"F4.wireOp",EDGE,"E7.6.12.0")}),1.0]])]});
            var Q30;
            Q30=makeQuery(id+"F4.imprint","IMPRINT",FACE,{"disambiguationData":[TD([[makeQuery(id+"F4.imprint","IMPRINT",EDGE,{"derivedFrom":sQuery(id+"F4.wireOp",EDGE,"E7.4.14.0")}),1.0]])]});
            var Q31;
            Q31=makeQuery(id+"F4.imprint","IMPRINT",FACE,{"disambiguationData":[TD([[makeQuery(id+"F4.imprint","IMPRINT",EDGE,{"derivedFrom":sQuery(id+"F4.wireOp",EDGE,"E7.2.1.0")}),1.0]])]});
            var Q32;
            Q32=makeQuery(id+"F4.imprint","IMPRINT",FACE,{"disambiguationData":[TD([[makeQuery(id+"F4.imprint","IMPRINT",EDGE,{"derivedFrom":sQuery(id+"F4.wireOp",EDGE,"E7.11.16.0")}),1.0]])]});
            var Q33;
            Q33=makeQuery(id+"F4.imprint","IMPRINT",FACE,{"disambiguationData":[TD([[makeQuery(id+"F4.imprint","IMPRINT",EDGE,{"derivedFrom":sQuery(id+"F4.wireOp",EDGE,"E7.13.14.0")}),1.0]])]});
            var Q34;
            Q34=makeQuery(id+"F4.imprint","IMPRINT",FACE,{"disambiguationData":[TD([[makeQuery(id+"F4.imprint","IMPRINT",EDGE,{"derivedFrom":sQuery(id+"F4.wireOp",EDGE,"E7.15.12.0")}),1.0]])]});
            var Q35;
            Q35=makeQuery(id+"F4.imprint","IMPRINT",FACE,{"disambiguationData":[TD([[makeQuery(id+"F4.imprint","IMPRINT",EDGE,{"derivedFrom":sQuery(id+"F4.wireOp",EDGE,"E7.17.10.0")}),1.0]])]});
            var Q36;
            Q36=makeQuery(id+"F4.imprint","IMPRINT",FACE,{"disambiguationData":[TD([[makeQuery(id+"F4.imprint","IMPRINT",EDGE,{"derivedFrom":sQuery(id+"F4.wireOp",EDGE,"E7.19.24.0")}),1.0]])]});
            var Q37;
            Q37=makeQuery(id+"F4.imprint","IMPRINT",FACE,{"disambiguationData":[TD([[makeQuery(id+"F4.imprint","IMPRINT",EDGE,{"derivedFrom":sQuery(id+"F4.wireOp",EDGE,"E7.0.20.0")}),1.0]])]});
            var Q38;
            Q38=makeQuery(id+"F4.imprint","IMPRINT",FACE,{"disambiguationData":[TD([[makeQuery(id+"F4.imprint","IMPRINT",EDGE,{"derivedFrom":sQuery(id+"F4.wireOp",EDGE,"E7.2.18.0")}),1.0]])]});
            var Q39;
            Q39=makeQuery(id+"F4.imprint","IMPRINT",FACE,{"disambiguationData":[TD([[makeQuery(id+"F4.imprint","IMPRINT",EDGE,{"derivedFrom":sQuery(id+"F4.wireOp",EDGE,"E7.6.14.0")}),1.0]])]});
            var Q40;
            Q40=makeQuery(id+"F4.imprint","IMPRINT",FACE,{"disambiguationData":[TD([[makeQuery(id+"F4.imprint","IMPRINT",EDGE,{"derivedFrom":sQuery(id+"F4.wireOp",EDGE,"E7.4.16.0")}),1.0]])]});
            var Q41;
            Q41=makeQuery(id+"F4.imprint","IMPRINT",FACE,{"disambiguationData":[TD([[makeQuery(id+"F4.imprint","IMPRINT",EDGE,{"derivedFrom":sQuery(id+"F4.wireOp",EDGE,"E7.11.1.0")}),1.0]])]});
            var Q42;
            Q42=makeQuery(id+"F4.imprint","IMPRINT",FACE,{"disambiguationData":[TD([[makeQuery(id+"F4.imprint","IMPRINT",EDGE,{"derivedFrom":sQuery(id+"F4.wireOp",EDGE,"E7.24.12.0")}),1.0]])]});
            var Q43;
            Q43=makeQuery(id+"F4.imprint","IMPRINT",FACE,{"disambiguationData":[TD([[makeQuery(id+"F4.imprint","IMPRINT",EDGE,{"derivedFrom":sQuery(id+"F4.wireOp",EDGE,"E7.4.1.0")}),1.0]])]});
            var Q44;
            Q44=makeQuery(id+"F4.imprint","IMPRINT",FACE,{"disambiguationData":[TD([[makeQuery(id+"F4.imprint","IMPRINT",EDGE,{"derivedFrom":sQuery(id+"F4.wireOp",EDGE,"E7.2.3.0")}),1.0]])]});
            var Q45;
            Q45=makeQuery(id+"F4.imprint","IMPRINT",FACE,{"disambiguationData":[TD([[makeQuery(id+"F4.imprint","IMPRINT",EDGE,{"derivedFrom":sQuery(id+"F4.wireOp",EDGE,"E7.11.18.0")}),1.0]])]});
            var Q46;
            Q46=makeQuery(id+"F4.imprint","IMPRINT",FACE,{"disambiguationData":[TD([[makeQuery(id+"F4.imprint","IMPRINT",EDGE,{"derivedFrom":sQuery(id+"F4.wireOp",EDGE,"E7.13.16.0")}),1.0]])]});
            var Q47;
            Q47=makeQuery(id+"F4.imprint","IMPRINT",FACE,{"disambiguationData":[TD([[makeQuery(id+"F4.imprint","IMPRINT",EDGE,{"derivedFrom":sQuery(id+"F4.wireOp",EDGE,"E7.15.14.0")}),1.0]])]});
            var Q48;
            Q48=makeQuery(id+"F4.imprint","IMPRINT",FACE,{"disambiguationData":[TD([[makeQuery(id+"F4.imprint","IMPRINT",EDGE,{"derivedFrom":sQuery(id+"F4.wireOp",EDGE,"E7.17.12.0")}),1.0]])]});
            var Q49;
            Q49=makeQuery(id+"F4.imprint","IMPRINT",FACE,{"disambiguationData":[TD([[makeQuery(id+"F4.imprint","IMPRINT",EDGE,{"derivedFrom":sQuery(id+"F4.wireOp",EDGE,"E7.2.20.0")}),1.0]])]});
            var Q50;
            Q50=makeQuery(id+"F4.imprint","IMPRINT",FACE,{"disambiguationData":[TD([[makeQuery(id+"F4.imprint","IMPRINT",EDGE,{"derivedFrom":sQuery(id+"F4.wireOp",EDGE,"E7.0.22.0")}),1.0]])]});
            var Q51;
            Q51=makeQuery(id+"F4.imprint","IMPRINT",FACE,{"disambiguationData":[TD([[makeQuery(id+"F4.imprint","IMPRINT",EDGE,{"derivedFrom":sQuery(id+"F4.wireOp",EDGE,"E7.4.18.0")}),1.0]])]});
            var Q52;
            Q52=makeQuery(id+"F4.imprint","IMPRINT",FACE,{"disambiguationData":[TD([[makeQuery(id+"F4.imprint","IMPRINT",EDGE,{"derivedFrom":sQuery(id+"F4.wireOp",EDGE,"E7.6.16.0")}),1.0]])]});
            var Q53;
            Q53=makeQuery(id+"F4.imprint","IMPRINT",FACE,{"disambiguationData":[TD([[makeQuery(id+"F4.imprint","IMPRINT",EDGE,{"derivedFrom":sQuery(id+"F4.wireOp",EDGE,"E7.8.14.0")}),1.0]])]});
            var Q54;
            Q54=makeQuery(id+"F4.imprint","IMPRINT",FACE,{"disambiguationData":[TD([[makeQuery(id+"F4.imprint","IMPRINT",EDGE,{"derivedFrom":sQuery(id+"F4.wireOp",EDGE,"E7.13.1.0")}),1.0]])]});
            var Q55;
            Q55=makeQuery(id+"F4.imprint","IMPRINT",FACE,{"disambiguationData":[TD([[makeQuery(id+"F4.imprint","IMPRINT",EDGE,{"derivedFrom":sQuery(id+"F4.wireOp",EDGE,"E7.11.3.0")}),1.0]])]});
            var Q56;
            Q56=makeQuery(id+"F4.imprint","IMPRINT",FACE,{"disambiguationData":[TD([[makeQuery(id+"F4.imprint","IMPRINT",EDGE,{"derivedFrom":sQuery(id+"F4.wireOp",EDGE,"E7.24.14.0")}),1.0]])]});
            var Q57;
            Q57=makeQuery(id+"F4.imprint","IMPRINT",FACE,{"disambiguationData":[TD([[makeQuery(id+"F4.imprint","IMPRINT",EDGE,{"derivedFrom":sQuery(id+"F4.wireOp",EDGE,"E7.22.16.0")}),1.0]])]});
            var Q58;
            Q58=makeQuery(id+"F4.imprint","IMPRINT",FACE,{"disambiguationData":[TD([[makeQuery(id+"F4.imprint","IMPRINT",EDGE,{"derivedFrom":sQuery(id+"F4.wireOp",EDGE,"E7.2.5.0")}),1.0]])]});
            var Q59;
            Q59=makeQuery(id+"F4.imprint","IMPRINT",FACE,{"disambiguationData":[TD([[makeQuery(id+"F4.imprint","IMPRINT",EDGE,{"derivedFrom":sQuery(id+"F4.wireOp",EDGE,"E7.4.3.0")}),1.0]])]});
            var Q60;
            Q60=makeQuery(id+"F4.imprint","IMPRINT",FACE,{"disambiguationData":[TD([[makeQuery(id+"F4.imprint","IMPRINT",EDGE,{"derivedFrom":sQuery(id+"F4.wireOp",EDGE,"E7.6.1.0")}),1.0]])]});
            var Q61;
            Q61=makeQuery(id+"F4.imprint","IMPRINT",FACE,{"disambiguationData":[TD([[makeQuery(id+"F4.imprint","IMPRINT",EDGE,{"derivedFrom":sQuery(id+"F4.wireOp",EDGE,"E7.11.20.0")}),1.0]])]});
            var Q62;
            Q62=makeQuery(id+"F4.imprint","IMPRINT",FACE,{"disambiguationData":[TD([[makeQuery(id+"F4.imprint","IMPRINT",EDGE,{"derivedFrom":sQuery(id+"F4.wireOp",EDGE,"E7.15.16.0")}),1.0]])]});
            var Q63;
            Q63=makeQuery(id+"F4.imprint","IMPRINT",FACE,{"disambiguationData":[TD([[makeQuery(id+"F4.imprint","IMPRINT",EDGE,{"derivedFrom":sQuery(id+"F4.wireOp",EDGE,"E7.13.18.0")}),1.0]])]});
            var Q64;
            Q64=makeQuery(id+"F4.imprint","IMPRINT",FACE,{"disambiguationData":[TD([[makeQuery(id+"F4.imprint","IMPRINT",EDGE,{"derivedFrom":sQuery(id+"F4.wireOp",EDGE,"E7.19.12.0")}),1.0]])]});
            var Q65;
            Q65=makeQuery(id+"F4.imprint","IMPRINT",FACE,{"disambiguationData":[TD([[makeQuery(id+"F4.imprint","IMPRINT",EDGE,{"derivedFrom":sQuery(id+"F4.wireOp",EDGE,"E7.17.14.0")}),1.0]])]});
            var Q66;
            Q66=makeQuery(id+"F4.imprint","IMPRINT",FACE,{"disambiguationData":[TD([[makeQuery(id+"F4.imprint","IMPRINT",EDGE,{"derivedFrom":sQuery(id+"F4.wireOp",EDGE,"E7.4.20.0")}),1.0]])]});
            var Q67;
            Q67=makeQuery(id+"F4.imprint","IMPRINT",FACE,{"disambiguationData":[TD([[makeQuery(id+"F4.imprint","IMPRINT",EDGE,{"derivedFrom":sQuery(id+"F4.wireOp",EDGE,"E7.6.18.0")}),1.0]])]});
            var Q68;
            Q68=makeQuery(id+"F4.imprint","IMPRINT",FACE,{"disambiguationData":[TD([[makeQuery(id+"F4.imprint","IMPRINT",EDGE,{"derivedFrom":sQuery(id+"F4.wireOp",EDGE,"E7.8.16.0")}),1.0]])]});
            var Q69;
            Q69=makeQuery(id+"F4.imprint","IMPRINT",FACE,{"disambiguationData":[TD([[makeQuery(id+"F4.imprint","IMPRINT",EDGE,{"derivedFrom":sQuery(id+"F4.wireOp",EDGE,"E7.13.3.0")}),1.0]])]});
            var Q70;
            Q70=makeQuery(id+"F4.imprint","IMPRINT",FACE,{"disambiguationData":[TD([[makeQuery(id+"F4.imprint","IMPRINT",EDGE,{"derivedFrom":sQuery(id+"F4.wireOp",EDGE,"E7.15.1.0")}),1.0]])]});
            var Q71;
            Q71=makeQuery(id+"F4.imprint","IMPRINT",FACE,{"disambiguationData":[TD([[makeQuery(id+"F4.imprint","IMPRINT",EDGE,{"derivedFrom":sQuery(id+"F4.wireOp",EDGE,"E7.2.22.0")}),1.0]])]});
            var Q72;
            Q72=makeQuery(id+"F4.imprint","IMPRINT",FACE,{"disambiguationData":[TD([[makeQuery(id+"F4.imprint","IMPRINT",EDGE,{"derivedFrom":sQuery(id+"F4.wireOp",EDGE,"E7.0.24.0")}),1.0]])]});
            var Q73;
            Q73=makeQuery(id+"F4.imprint","IMPRINT",FACE,{"disambiguationData":[TD([[makeQuery(id+"F4.imprint","IMPRINT",EDGE,{"derivedFrom":sQuery(id+"F4.wireOp",EDGE,"E7.24.16.0")}),1.0]])]});
            var Q74;
            Q74=makeQuery(id+"F4.imprint","IMPRINT",FACE,{"disambiguationData":[TD([[makeQuery(id+"F4.imprint","IMPRINT",EDGE,{"derivedFrom":sQuery(id+"F4.wireOp",EDGE,"E7.22.18.0")}),1.0]])]});
            var Q75;
            Q75=makeQuery(id+"F4.imprint","IMPRINT",FACE,{"disambiguationData":[TD([[makeQuery(id+"F4.imprint","IMPRINT",EDGE,{"derivedFrom":sQuery(id+"F4.wireOp",EDGE,"E7.8.1.0")}),1.0]])]});
            var Q76;
            Q76=makeQuery(id+"F4.imprint","IMPRINT",FACE,{"disambiguationData":[TD([[makeQuery(id+"F4.imprint","IMPRINT",EDGE,{"derivedFrom":sQuery(id+"F4.wireOp",EDGE,"E7.6.3.0")}),1.0]])]});
            var Q77;
            Q77=makeQuery(id+"F4.imprint","IMPRINT",FACE,{"disambiguationData":[TD([[makeQuery(id+"F4.imprint","IMPRINT",EDGE,{"derivedFrom":sQuery(id+"F4.wireOp",EDGE,"E7.11.22.0")}),1.0]])]});
            var Q78;
            Q78=makeQuery(id+"F4.imprint","IMPRINT",FACE,{"disambiguationData":[TD([[makeQuery(id+"F4.imprint","IMPRINT",EDGE,{"derivedFrom":sQuery(id+"F4.wireOp",EDGE,"E7.15.18.0")}),1.0]])]});
            var Q79;
            Q79=makeQuery(id+"F4.imprint","IMPRINT",FACE,{"disambiguationData":[TD([[makeQuery(id+"F4.imprint","IMPRINT",EDGE,{"derivedFrom":sQuery(id+"F4.wireOp",EDGE,"E7.13.20.0")}),1.0]])]});
            var Q80;
            Q80=makeQuery(id+"F4.imprint","IMPRINT",FACE,{"disambiguationData":[TD([[makeQuery(id+"F4.imprint","IMPRINT",EDGE,{"derivedFrom":sQuery(id+"F4.wireOp",EDGE,"E7.19.14.0")}),1.0]])]});
            var Q81;
            Q81=makeQuery(id+"F4.imprint","IMPRINT",FACE,{"disambiguationData":[TD([[makeQuery(id+"F4.imprint","IMPRINT",EDGE,{"derivedFrom":sQuery(id+"F4.wireOp",EDGE,"E7.17.16.0")}),1.0]])]});
            var Q82;
            Q82=makeQuery(id+"F4.imprint","IMPRINT",FACE,{"disambiguationData":[TD([[makeQuery(id+"F4.imprint","IMPRINT",EDGE,{"derivedFrom":sQuery(id+"F4.wireOp",EDGE,"E7.4.5.0")}),1.0]])]});
            var Q83;
            Q83=makeQuery(id+"F4.imprint","IMPRINT",FACE,{"disambiguationData":[TD([[makeQuery(id+"F4.imprint","IMPRINT",EDGE,{"derivedFrom":sQuery(id+"F4.wireOp",EDGE,"E7.24.1.0")}),1.0]])]});
            var Q84;
            Q84=makeQuery(id+"F4.imprint","IMPRINT",FACE,{"disambiguationData":[TD([[makeQuery(id+"F4.imprint","IMPRINT",EDGE,{"derivedFrom":sQuery(id+"F4.wireOp",EDGE,"E7.8.18.0")}),1.0]])]});
            var Q85;
            Q85=makeQuery(id+"F4.imprint","IMPRINT",FACE,{"disambiguationData":[TD([[makeQuery(id+"F4.imprint","IMPRINT",EDGE,{"derivedFrom":sQuery(id+"F4.wireOp",EDGE,"E7.13.5.0")}),1.0]])]});
            var Q86;
            Q86=makeQuery(id+"F4.imprint","IMPRINT",FACE,{"disambiguationData":[TD([[makeQuery(id+"F4.imprint","IMPRINT",EDGE,{"derivedFrom":sQuery(id+"F4.wireOp",EDGE,"E7.15.3.0")}),1.0]])]});
            var Q87;
            Q87=makeQuery(id+"F4.imprint","IMPRINT",FACE,{"disambiguationData":[TD([[makeQuery(id+"F4.imprint","IMPRINT",EDGE,{"derivedFrom":sQuery(id+"F4.wireOp",EDGE,"E7.17.1.0")}),1.0]])]});
            var Q88;
            Q88=makeQuery(id+"F4.imprint","IMPRINT",FACE,{"disambiguationData":[TD([[makeQuery(id+"F4.imprint","IMPRINT",EDGE,{"derivedFrom":sQuery(id+"F4.wireOp",EDGE,"E7.24.18.0")}),1.0]])]});
            var Q89;
            Q89=makeQuery(id+"F4.imprint","IMPRINT",FACE,{"disambiguationData":[TD([[makeQuery(id+"F4.imprint","IMPRINT",EDGE,{"derivedFrom":sQuery(id+"F4.wireOp",EDGE,"E7.22.20.0")}),1.0]])]});
            var Q90;
            Q90=makeQuery(id+"F4.imprint","IMPRINT",FACE,{"disambiguationData":[TD([[makeQuery(id+"F4.imprint","IMPRINT",EDGE,{"derivedFrom":sQuery(id+"F4.wireOp",EDGE,"E7.2.24.0")}),1.0]])]});
            var Q91;
            Q91=makeQuery(id+"F4.imprint","IMPRINT",FACE,{"disambiguationData":[TD([[makeQuery(id+"F4.imprint","IMPRINT",EDGE,{"derivedFrom":sQuery(id+"F4.wireOp",EDGE,"E7.4.22.0")}),1.0]])]});
            var Q92;
            Q92=makeQuery(id+"F4.imprint","IMPRINT",FACE,{"disambiguationData":[TD([[makeQuery(id+"F4.imprint","IMPRINT",EDGE,{"derivedFrom":sQuery(id+"F4.wireOp",EDGE,"E7.6.20.0")}),1.0]])]});
            var Q93;
            Q93=makeQuery(id+"F4.imprint","IMPRINT",FACE,{"disambiguationData":[TD([[makeQuery(id+"F4.imprint","IMPRINT",EDGE,{"derivedFrom":sQuery(id+"F4.wireOp",EDGE,"E7.11.24.0")}),1.0]])]});
            var Q94;
            Q94=makeQuery(id+"F4.imprint","IMPRINT",FACE,{"disambiguationData":[TD([[makeQuery(id+"F4.imprint","IMPRINT",EDGE,{"derivedFrom":sQuery(id+"F4.wireOp",EDGE,"E7.15.20.0")}),1.0]])]});
            var Q95;
            Q95=makeQuery(id+"F4.imprint","IMPRINT",FACE,{"disambiguationData":[TD([[makeQuery(id+"F4.imprint","IMPRINT",EDGE,{"derivedFrom":sQuery(id+"F4.wireOp",EDGE,"E7.13.22.0")}),1.0]])]});
            var Q96;
            Q96=makeQuery(id+"F4.imprint","IMPRINT",FACE,{"disambiguationData":[TD([[makeQuery(id+"F4.imprint","IMPRINT",EDGE,{"derivedFrom":sQuery(id+"F4.wireOp",EDGE,"E7.19.16.0")}),1.0]])]});
            var Q97;
            Q97=makeQuery(id+"F4.imprint","IMPRINT",FACE,{"disambiguationData":[TD([[makeQuery(id+"F4.imprint","IMPRINT",EDGE,{"derivedFrom":sQuery(id+"F4.wireOp",EDGE,"E7.17.18.0")}),1.0]])]});
            var Q98;
            Q98=makeQuery(id+"F4.imprint","IMPRINT",FACE,{"disambiguationData":[TD([[makeQuery(id+"F4.imprint","IMPRINT",EDGE,{"derivedFrom":sQuery(id+"F4.wireOp",EDGE,"E7.24.3.0")}),1.0]])]});
            var Q99;
            Q99=makeQuery(id+"F4.imprint","IMPRINT",FACE,{"disambiguationData":[TD([[makeQuery(id+"F4.imprint","IMPRINT",EDGE,{"derivedFrom":sQuery(id+"F4.wireOp",EDGE,"E7.6.5.0")}),1.0]])]});
            var Q100;
            Q100=makeQuery(id+"F4.imprint","IMPRINT",FACE,{"disambiguationData":[TD([[makeQuery(id+"F4.imprint","IMPRINT",EDGE,{"derivedFrom":sQuery(id+"F4.wireOp",EDGE,"E7.15.5.0")}),1.0]])]});
            var Q101;
            Q101=makeQuery(id+"F4.imprint","IMPRINT",FACE,{"disambiguationData":[TD([[makeQuery(id+"F4.imprint","IMPRINT",EDGE,{"derivedFrom":sQuery(id+"F4.wireOp",EDGE,"E7.17.3.0")}),1.0]])]});
            var Q102;
            Q102=makeQuery(id+"F4.imprint","IMPRINT",FACE,{"disambiguationData":[TD([[makeQuery(id+"F4.imprint","IMPRINT",EDGE,{"derivedFrom":sQuery(id+"F4.wireOp",EDGE,"E7.19.1.0")}),1.0]])]});
            var Q103;
            Q103=makeQuery(id+"F4.imprint","IMPRINT",FACE,{"disambiguationData":[TD([[makeQuery(id+"F4.imprint","IMPRINT",EDGE,{"derivedFrom":sQuery(id+"F4.wireOp",EDGE,"E7.24.20.0")}),1.0]])]});
            var Q104;
            Q104=makeQuery(id+"F4.imprint","IMPRINT",FACE,{"disambiguationData":[TD([[makeQuery(id+"F4.imprint","IMPRINT",EDGE,{"derivedFrom":sQuery(id+"F4.wireOp",EDGE,"E7.22.22.0")}),1.0]])]});
            var Q105;
            Q105=makeQuery(id+"F4.imprint","IMPRINT",FACE,{"disambiguationData":[TD([[makeQuery(id+"F4.imprint","IMPRINT",EDGE,{"derivedFrom":sQuery(id+"F4.wireOp",EDGE,"E7.2.10.0")}),1.0]])]});
            var Q106;
            Q106=makeQuery(id+"F4.imprint","IMPRINT",FACE,{"disambiguationData":[TD([[makeQuery(id+"F4.imprint","IMPRINT",EDGE,{"derivedFrom":sQuery(id+"F4.wireOp",EDGE,"E7.4.24.0")}),1.0]])]});
            var Q107;
            Q107=makeQuery(id+"F4.imprint","IMPRINT",FACE,{"disambiguationData":[TD([[makeQuery(id+"F4.imprint","IMPRINT",EDGE,{"derivedFrom":sQuery(id+"F4.wireOp",EDGE,"E7.6.22.0")}),1.0]])]});
            var Q108;
            Q108=makeQuery(id+"F4.imprint","IMPRINT",FACE,{"disambiguationData":[TD([[makeQuery(id+"F4.imprint","IMPRINT",EDGE,{"derivedFrom":sQuery(id+"F4.wireOp",EDGE,"E7.8.20.0")}),1.0]])]});
            var Q109;
            Q109=makeQuery(id+"F4.imprint","IMPRINT",FACE,{"disambiguationData":[TD([[makeQuery(id+"F4.imprint","IMPRINT",EDGE,{"derivedFrom":sQuery(id+"F4.wireOp",EDGE,"E7.0.14.0")}),1.0]])]});
            var Q110;
            Q110=makeQuery(id+"F4.imprint","IMPRINT",FACE,{"disambiguationData":[TD([[makeQuery(id+"F4.imprint","IMPRINT",EDGE,{"derivedFrom":sQuery(id+"F4.wireOp",EDGE,"E7.0.3.0")}),1.0]])]});
            var Q111;
            Q111=makeQuery(id+"F4.imprint","IMPRINT",FACE,{"disambiguationData":[TD([[makeQuery(id+"F4.imprint","IMPRINT",EDGE,{"derivedFrom":sQuery(id+"F4.wireOp",EDGE,"E7.0.5.0")}),1.0]])]});
            var Q112;
            Q112=makeQuery(id+"F4.imprint","IMPRINT",FACE,{"disambiguationData":[TD([[makeQuery(id+"F4.imprint","IMPRINT",EDGE,{"derivedFrom":sQuery(id+"F4.wireOp",EDGE,"E7.0.12.0")}),1.0]])]});
            var Q113;
            Q113=makeQuery(id+"F4.imprint","IMPRINT",FACE,{"disambiguationData":[TD([[makeQuery(id+"F4.imprint","IMPRINT",EDGE,{"derivedFrom":sQuery(id+"F4.wireOp",EDGE,"E7.7.0.0")}),1.0]])]});
            var Q114;
            Q114=makeQuery(id+"F4.imprint","IMPRINT",FACE,{"disambiguationData":[TD([[makeQuery(id+"F4.imprint","IMPRINT",EDGE,{"derivedFrom":sQuery(id+"F4.wireOp",EDGE,"E7.6.9.0")}),1.0]])]});
            var Q115;
            Q115=makeQuery(id+"F4.imprint","IMPRINT",FACE,{"disambiguationData":[TD([[makeQuery(id+"F4.imprint","IMPRINT",EDGE,{"derivedFrom":sQuery(id+"F4.wireOp",EDGE,"E7.5.18.0")}),1.0]])]});
            var Q116;
            Q116=makeQuery(id+"F4.imprint","IMPRINT",FACE,{"disambiguationData":[TD([[makeQuery(id+"F4.imprint","IMPRINT",EDGE,{"derivedFrom":sQuery(id+"F4.wireOp",EDGE,"E7.5.2.0")}),1.0]])]});
            var Q117;
            Q117=makeQuery(id+"F4.imprint","IMPRINT",FACE,{"disambiguationData":[TD([[makeQuery(id+"F4.imprint","IMPRINT",EDGE,{"derivedFrom":sQuery(id+"F4.wireOp",EDGE,"E7.9.14.0")}),1.0]])]});
            var Q118;
            Q118=makeQuery(id+"F4.imprint","IMPRINT",FACE,{"disambiguationData":[TD([[makeQuery(id+"F4.imprint","IMPRINT",EDGE,{"derivedFrom":sQuery(id+"F4.wireOp",EDGE,"E7.8.23.0")}),1.0]])]});
            var Q119;
            Q119=makeQuery(id+"F4.imprint","IMPRINT",FACE,{"disambiguationData":[TD([[makeQuery(id+"F4.imprint","IMPRINT",EDGE,{"derivedFrom":sQuery(id+"F4.wireOp",EDGE,"E7.8.7.0")}),1.0]])]});
            var Q120;
            Q120=makeQuery(id+"F4.imprint","IMPRINT",FACE,{"disambiguationData":[TD([[makeQuery(id+"F4.imprint","IMPRINT",EDGE,{"derivedFrom":sQuery(id+"F4.wireOp",EDGE,"E7.7.16.0")}),1.0]])]});
            var Q121;
            Q121=makeQuery(id+"F4.imprint","IMPRINT",FACE,{"disambiguationData":[TD([[makeQuery(id+"F4.imprint","IMPRINT",EDGE,{"derivedFrom":sQuery(id+"F4.wireOp",EDGE,"E7.12.3.0")}),1.0]])]});
            var Q122;
            Q122=makeQuery(id+"F4.imprint","IMPRINT",FACE,{"disambiguationData":[TD([[makeQuery(id+"F4.imprint","IMPRINT",EDGE,{"derivedFrom":sQuery(id+"F4.wireOp",EDGE,"E7.11.12.0")}),1.0]])]});
            var Q123;
            Q123=makeQuery(id+"F4.imprint","IMPRINT",FACE,{"disambiguationData":[TD([[makeQuery(id+"F4.imprint","IMPRINT",EDGE,{"derivedFrom":sQuery(id+"F4.wireOp",EDGE,"E7.10.21.0")}),1.0]])]});
            var Q124;
            Q124=makeQuery(id+"F4.imprint","IMPRINT",FACE,{"disambiguationData":[TD([[makeQuery(id+"F4.imprint","IMPRINT",EDGE,{"derivedFrom":sQuery(id+"F4.wireOp",EDGE,"E7.10.5.0")}),1.0]])]});
            var Q125;
            Q125=makeQuery(id+"F4.imprint","IMPRINT",FACE,{"disambiguationData":[TD([[makeQuery(id+"F4.imprint","IMPRINT",EDGE,{"derivedFrom":sQuery(id+"F4.wireOp",EDGE,"E7.14.17.0")}),1.0]])]});
            var Q126;
            Q126=makeQuery(id+"F4.imprint","IMPRINT",FACE,{"disambiguationData":[TD([[makeQuery(id+"F4.imprint","IMPRINT",EDGE,{"derivedFrom":sQuery(id+"F4.wireOp",EDGE,"E7.14.1.0")}),1.0]])]});
            var Q127;
            Q127=makeQuery(id+"F4.imprint","IMPRINT",FACE,{"disambiguationData":[TD([[makeQuery(id+"F4.imprint","IMPRINT",EDGE,{"derivedFrom":sQuery(id+"F4.wireOp",EDGE,"E7.12.19.0")}),1.0]])]});
            var Q128;
            Q128=makeQuery(id+"F4.imprint","IMPRINT",FACE,{"disambiguationData":[TD([[makeQuery(id+"F4.imprint","IMPRINT",EDGE,{"derivedFrom":sQuery(id+"F4.wireOp",EDGE,"E7.16.15.0")}),1.0]])]});
            var Q129;
            Q129=makeQuery(id+"F4.imprint","IMPRINT",FACE,{"disambiguationData":[TD([[makeQuery(id+"F4.imprint","IMPRINT",EDGE,{"derivedFrom":sQuery(id+"F4.wireOp",EDGE,"E7.15.8.0")}),1.0]])]});
            var Q130;
            Q130=makeQuery(id+"F4.imprint","IMPRINT",FACE,{"disambiguationData":[TD([[makeQuery(id+"F4.imprint","IMPRINT",EDGE,{"derivedFrom":sQuery(id+"F4.wireOp",EDGE,"E7.18.13.0")}),1.0]])]});
            var Q131;
            Q131=makeQuery(id+"F4.imprint","IMPRINT",FACE,{"disambiguationData":[TD([[makeQuery(id+"F4.imprint","IMPRINT",EDGE,{"derivedFrom":sQuery(id+"F4.wireOp",EDGE,"E7.17.6.0")}),1.0]])]});
            var Q132;
            Q132=makeQuery(id+"F4.imprint","IMPRINT",FACE,{"disambiguationData":[TD([[makeQuery(id+"F4.imprint","IMPRINT",EDGE,{"derivedFrom":sQuery(id+"F4.wireOp",EDGE,"E7.21.2.0")}),1.0]])]});
            var Q133;
            Q133=makeQuery(id+"F4.imprint","IMPRINT",FACE,{"disambiguationData":[TD([[makeQuery(id+"F4.imprint","IMPRINT",EDGE,{"derivedFrom":sQuery(id+"F4.wireOp",EDGE,"E7.20.11.0")}),1.0]])]});
            var Q134;
            Q134=makeQuery(id+"F4.imprint","IMPRINT",FACE,{"disambiguationData":[TD([[makeQuery(id+"F4.imprint","IMPRINT",EDGE,{"derivedFrom":sQuery(id+"F4.wireOp",EDGE,"E7.19.4.0")}),1.0]])]});
            var Q135;
            Q135=makeQuery(id+"F4.imprint","IMPRINT",FACE,{"disambiguationData":[TD([[makeQuery(id+"F4.imprint","IMPRINT",EDGE,{"derivedFrom":sQuery(id+"F4.wireOp",EDGE,"E7.1.22.0")}),1.0]])]});
            var Q136;
            Q136=makeQuery(id+"F4.imprint","IMPRINT",FACE,{"disambiguationData":[TD([[makeQuery(id+"F4.imprint","IMPRINT",EDGE,{"derivedFrom":sQuery(id+"F4.wireOp",EDGE,"E7.1.6.0")}),1.0]])]});
            var Q137;
            Q137=makeQuery(id+"F4.imprint","IMPRINT",FACE,{"disambiguationData":[TD([[makeQuery(id+"F4.imprint","IMPRINT",EDGE,{"derivedFrom":sQuery(id+"F4.wireOp",EDGE,"E7.4.11.0")}),1.0]])]});
            var Q138;
            Q138=makeQuery(id+"F4.imprint","IMPRINT",FACE,{"disambiguationData":[TD([[makeQuery(id+"F4.imprint","IMPRINT",EDGE,{"derivedFrom":sQuery(id+"F4.wireOp",EDGE,"E7.3.20.0")}),1.0]])]});
            var Q139;
            Q139=makeQuery(id+"F4.imprint","IMPRINT",FACE,{"disambiguationData":[TD([[makeQuery(id+"F4.imprint","IMPRINT",EDGE,{"derivedFrom":sQuery(id+"F4.wireOp",EDGE,"E7.3.4.0")}),1.0]])]});
            var Q140;
            Q140=makeQuery(id+"F4.imprint","IMPRINT",FACE,{"disambiguationData":[TD([[makeQuery(id+"F4.imprint","IMPRINT",EDGE,{"derivedFrom":sQuery(id+"F4.wireOp",EDGE,"E7.2.13.0")}),1.0]])]});
            var Q141;
            Q141=makeQuery(id+"F4.imprint","IMPRINT",FACE,{"disambiguationData":[TD([[makeQuery(id+"F4.imprint","IMPRINT",EDGE,{"derivedFrom":sQuery(id+"F4.wireOp",EDGE,"E7.23.16.0")}),1.0]])]});
            var Q142;
            Q142=makeQuery(id+"F4.imprint","IMPRINT",FACE,{"disambiguationData":[TD([[makeQuery(id+"F4.imprint","IMPRINT",EDGE,{"derivedFrom":sQuery(id+"F4.wireOp",EDGE,"E7.23.0.0")}),1.0]])]});
            var Q143;
            Q143=makeQuery(id+"F4.imprint","IMPRINT",FACE,{"disambiguationData":[TD([[makeQuery(id+"F4.imprint","IMPRINT",EDGE,{"derivedFrom":sQuery(id+"F4.wireOp",EDGE,"E7.22.9.0")}),1.0]])]});
            var Q144;
            Q144=makeQuery(id+"F4.imprint","IMPRINT",FACE,{"disambiguationData":[TD([[makeQuery(id+"F4.imprint","IMPRINT",EDGE,{"derivedFrom":sQuery(id+"F4.wireOp",EDGE,"E7.21.18.0")}),1.0]])]});
            var Q145;
            Q145=makeQuery(id+"F4.imprint","IMPRINT",FACE,{"disambiguationData":[TD([[makeQuery(id+"F4.imprint","IMPRINT",EDGE,{"derivedFrom":sQuery(id+"F4.wireOp",EDGE,"E7.24.23.0")}),1.0]])]});
            var Q146;
            Q146=makeQuery(id+"F4.imprint","IMPRINT",FACE,{"disambiguationData":[TD([[makeQuery(id+"F4.imprint","IMPRINT",EDGE,{"derivedFrom":sQuery(id+"F4.wireOp",EDGE,"E7.24.7.0")}),1.0]])]});
            var Q147;
            Q147=makeQuery(id+"F4.imprint","IMPRINT",FACE,{"disambiguationData":[TD([[makeQuery(id+"F4.imprint","IMPRINT",EDGE,{"derivedFrom":sQuery(id+"F4.wireOp",EDGE,"E7.1.4.0")}),1.0]])]});
            var Q148;
            Q148=makeQuery(id+"F4.imprint","IMPRINT",FACE,{"disambiguationData":[TD([[makeQuery(id+"F4.imprint","IMPRINT",EDGE,{"derivedFrom":sQuery(id+"F4.wireOp",EDGE,"E7.3.18.0")}),1.0]])]});
            var Q149;
            Q149=makeQuery(id+"F4.imprint","IMPRINT",FACE,{"disambiguationData":[TD([[makeQuery(id+"F4.imprint","IMPRINT",EDGE,{"derivedFrom":sQuery(id+"F4.wireOp",EDGE,"E7.3.2.0")}),1.0]])]});
            var Q150;
            Q150=makeQuery(id+"F4.imprint","IMPRINT",FACE,{"disambiguationData":[TD([[makeQuery(id+"F4.imprint","IMPRINT",EDGE,{"derivedFrom":sQuery(id+"F4.wireOp",EDGE,"E7.2.11.0")}),1.0]])]});
            var Q151;
            Q151=makeQuery(id+"F4.imprint","IMPRINT",FACE,{"disambiguationData":[TD([[makeQuery(id+"F4.imprint","IMPRINT",EDGE,{"derivedFrom":sQuery(id+"F4.wireOp",EDGE,"E7.1.20.0")}),1.0]])]});
            var Q152;
            Q152=makeQuery(id+"F4.imprint","IMPRINT",FACE,{"disambiguationData":[TD([[makeQuery(id+"F4.imprint","IMPRINT",EDGE,{"derivedFrom":sQuery(id+"F4.wireOp",EDGE,"E7.6.7.0")}),1.0]])]});
            var Q153;
            Q153=makeQuery(id+"F4.imprint","IMPRINT",FACE,{"disambiguationData":[TD([[makeQuery(id+"F4.imprint","IMPRINT",EDGE,{"derivedFrom":sQuery(id+"F4.wireOp",EDGE,"E7.5.16.0")}),1.0]])]});
            var Q154;
            Q154=makeQuery(id+"F4.imprint","IMPRINT",FACE,{"disambiguationData":[TD([[makeQuery(id+"F4.imprint","IMPRINT",EDGE,{"derivedFrom":sQuery(id+"F4.wireOp",EDGE,"E7.5.0.0")}),1.0]])]});
            var Q155;
            Q155=makeQuery(id+"F4.imprint","IMPRINT",FACE,{"disambiguationData":[TD([[makeQuery(id+"F4.imprint","IMPRINT",EDGE,{"derivedFrom":sQuery(id+"F4.wireOp",EDGE,"E7.4.9.0")}),1.0]])]});
            var Q156;
            Q156=makeQuery(id+"F4.imprint","IMPRINT",FACE,{"disambiguationData":[TD([[makeQuery(id+"F4.imprint","IMPRINT",EDGE,{"derivedFrom":sQuery(id+"F4.wireOp",EDGE,"E7.8.21.0")}),1.0]])]});
            var Q157;
            Q157=makeQuery(id+"F4.imprint","IMPRINT",FACE,{"disambiguationData":[TD([[makeQuery(id+"F4.imprint","IMPRINT",EDGE,{"derivedFrom":sQuery(id+"F4.wireOp",EDGE,"E7.8.5.0")}),1.0]])]});
            var Q158;
            Q158=makeQuery(id+"F4.imprint","IMPRINT",FACE,{"disambiguationData":[TD([[makeQuery(id+"F4.imprint","IMPRINT",EDGE,{"derivedFrom":sQuery(id+"F4.wireOp",EDGE,"E7.7.14.0")}),1.0]])]});
            var Q159;
            Q159=makeQuery(id+"F4.imprint","IMPRINT",FACE,{"disambiguationData":[TD([[makeQuery(id+"F4.imprint","IMPRINT",EDGE,{"derivedFrom":sQuery(id+"F4.wireOp",EDGE,"E7.6.23.0")}),1.0]])]});
            var Q160;
            Q160=makeQuery(id+"F4.imprint","IMPRINT",FACE,{"disambiguationData":[TD([[makeQuery(id+"F4.imprint","IMPRINT",EDGE,{"derivedFrom":sQuery(id+"F4.wireOp",EDGE,"E7.11.10.0")}),1.0]])]});
            var Q161;
            Q161=makeQuery(id+"F4.imprint","IMPRINT",FACE,{"disambiguationData":[TD([[makeQuery(id+"F4.imprint","IMPRINT",EDGE,{"derivedFrom":sQuery(id+"F4.wireOp",EDGE,"E7.10.19.0")}),1.0]])]});
            var Q162;
            Q162=makeQuery(id+"F4.imprint","IMPRINT",FACE,{"disambiguationData":[TD([[makeQuery(id+"F4.imprint","IMPRINT",EDGE,{"derivedFrom":sQuery(id+"F4.wireOp",EDGE,"E7.10.3.0")}),1.0]])]});
            var Q163;
            Q163=makeQuery(id+"F4.imprint","IMPRINT",FACE,{"disambiguationData":[TD([[makeQuery(id+"F4.imprint","IMPRINT",EDGE,{"derivedFrom":sQuery(id+"F4.wireOp",EDGE,"E7.9.12.0")}),1.0]])]});
            var Q164;
            Q164=makeQuery(id+"F4.imprint","IMPRINT",FACE,{"disambiguationData":[TD([[makeQuery(id+"F4.imprint","IMPRINT",EDGE,{"derivedFrom":sQuery(id+"F4.wireOp",EDGE,"E7.13.8.0")}),1.0]])]});
            var Q165;
            Q165=makeQuery(id+"F4.imprint","IMPRINT",FACE,{"disambiguationData":[TD([[makeQuery(id+"F4.imprint","IMPRINT",EDGE,{"derivedFrom":sQuery(id+"F4.wireOp",EDGE,"E7.12.17.0")}),1.0]])]});
            var Q166;
            Q166=makeQuery(id+"F4.imprint","IMPRINT",FACE,{"disambiguationData":[TD([[makeQuery(id+"F4.imprint","IMPRINT",EDGE,{"derivedFrom":sQuery(id+"F4.wireOp",EDGE,"E7.12.1.0")}),1.0]])]});
            var Q167;
            Q167=makeQuery(id+"F4.imprint","IMPRINT",FACE,{"disambiguationData":[TD([[makeQuery(id+"F4.imprint","IMPRINT",EDGE,{"derivedFrom":sQuery(id+"F4.wireOp",EDGE,"E7.16.13.0")}),1.0]])]});
            var Q168;
            Q168=makeQuery(id+"F4.imprint","IMPRINT",FACE,{"disambiguationData":[TD([[makeQuery(id+"F4.imprint","IMPRINT",EDGE,{"derivedFrom":sQuery(id+"F4.wireOp",EDGE,"E7.15.6.0")}),1.0]])]});
            var Q169;
            Q169=makeQuery(id+"F4.imprint","IMPRINT",FACE,{"disambiguationData":[TD([[makeQuery(id+"F4.imprint","IMPRINT",EDGE,{"derivedFrom":sQuery(id+"F4.wireOp",EDGE,"E7.14.15.0")}),1.0]])]});
            var Q170;
            Q170=makeQuery(id+"F4.imprint","IMPRINT",FACE,{"disambiguationData":[TD([[makeQuery(id+"F4.imprint","IMPRINT",EDGE,{"derivedFrom":sQuery(id+"F4.wireOp",EDGE,"E7.17.4.0")}),1.0]])]});
            var Q171;
            Q171=makeQuery(id+"F4.imprint","IMPRINT",FACE,{"disambiguationData":[TD([[makeQuery(id+"F4.imprint","IMPRINT",EDGE,{"derivedFrom":sQuery(id+"F4.wireOp",EDGE,"E7.20.9.0")}),1.0]])]});
            var Q172;
            Q172=makeQuery(id+"F4.imprint","IMPRINT",FACE,{"disambiguationData":[TD([[makeQuery(id+"F4.imprint","IMPRINT",EDGE,{"derivedFrom":sQuery(id+"F4.wireOp",EDGE,"E7.19.2.0")}),1.0]])]});
            var Q173;
            Q173=makeQuery(id+"F4.imprint","IMPRINT",FACE,{"disambiguationData":[TD([[makeQuery(id+"F4.imprint","IMPRINT",EDGE,{"derivedFrom":sQuery(id+"F4.wireOp",EDGE,"E7.18.11.0")}),1.0]])]});
            var Q174;
            Q174=makeQuery(id+"F4.imprint","IMPRINT",FACE,{"disambiguationData":[TD([[makeQuery(id+"F4.imprint","IMPRINT",EDGE,{"derivedFrom":sQuery(id+"F4.wireOp",EDGE,"E7.22.23.0")}),1.0]])]});
            var Q175;
            Q175=makeQuery(id+"F4.imprint","IMPRINT",FACE,{"disambiguationData":[TD([[makeQuery(id+"F4.imprint","IMPRINT",EDGE,{"derivedFrom":sQuery(id+"F4.wireOp",EDGE,"E7.22.7.0")}),1.0]])]});
            var Q176;
            Q176=makeQuery(id+"F4.imprint","IMPRINT",FACE,{"disambiguationData":[TD([[makeQuery(id+"F4.imprint","IMPRINT",EDGE,{"derivedFrom":sQuery(id+"F4.wireOp",EDGE,"E7.21.16.0")}),1.0]])]});
            var Q177;
            Q177=makeQuery(id+"F4.imprint","IMPRINT",FACE,{"disambiguationData":[TD([[makeQuery(id+"F4.imprint","IMPRINT",EDGE,{"derivedFrom":sQuery(id+"F4.wireOp",EDGE,"E7.21.0.0")}),1.0]])]});
            var Q178;
            Q178=makeQuery(id+"F4.imprint","IMPRINT",FACE,{"disambiguationData":[TD([[makeQuery(id+"F4.imprint","IMPRINT",EDGE,{"derivedFrom":sQuery(id+"F4.wireOp",EDGE,"E7.24.21.0")}),1.0]])]});
            var Q179;
            Q179=makeQuery(id+"F4.imprint","IMPRINT",FACE,{"disambiguationData":[TD([[makeQuery(id+"F4.imprint","IMPRINT",EDGE,{"derivedFrom":sQuery(id+"F4.wireOp",EDGE,"E7.23.14.0")}),1.0]])]});
            var Q180;
            Q180=makeQuery(id+"F4.imprint","IMPRINT",FACE,{"disambiguationData":[TD([[makeQuery(id+"F4.imprint","IMPRINT",EDGE,{"derivedFrom":sQuery(id+"F4.wireOp",EDGE,"E7.1.5.0")}),1.0]])]});
            var Q181;
            Q181=makeQuery(id+"F4.imprint","IMPRINT",FACE,{"disambiguationData":[TD([[makeQuery(id+"F4.imprint","IMPRINT",EDGE,{"derivedFrom":sQuery(id+"F4.wireOp",EDGE,"E7.3.19.0")}),1.0]])]});
            var Q182;
            Q182=makeQuery(id+"F4.imprint","IMPRINT",FACE,{"disambiguationData":[TD([[makeQuery(id+"F4.imprint","IMPRINT",EDGE,{"derivedFrom":sQuery(id+"F4.wireOp",EDGE,"E7.3.3.0")}),1.0]])]});
            var Q183;
            Q183=makeQuery(id+"F4.imprint","IMPRINT",FACE,{"disambiguationData":[TD([[makeQuery(id+"F4.imprint","IMPRINT",EDGE,{"derivedFrom":sQuery(id+"F4.wireOp",EDGE,"E7.1.21.0")}),1.0]])]});
            var Q184;
            Q184=makeQuery(id+"F4.imprint","IMPRINT",FACE,{"disambiguationData":[TD([[makeQuery(id+"F4.imprint","IMPRINT",EDGE,{"derivedFrom":sQuery(id+"F4.wireOp",EDGE,"E7.6.8.0")}),1.0]])]});
            var Q185;
            Q185=makeQuery(id+"F4.imprint","IMPRINT",FACE,{"disambiguationData":[TD([[makeQuery(id+"F4.imprint","IMPRINT",EDGE,{"derivedFrom":sQuery(id+"F4.wireOp",EDGE,"E7.5.17.0")}),1.0]])]});
            var Q186;
            Q186=makeQuery(id+"F4.imprint","IMPRINT",FACE,{"disambiguationData":[TD([[makeQuery(id+"F4.imprint","IMPRINT",EDGE,{"derivedFrom":sQuery(id+"F4.wireOp",EDGE,"E7.5.1.0")}),1.0]])]});
            var Q187;
            Q187=makeQuery(id+"F4.imprint","IMPRINT",FACE,{"disambiguationData":[TD([[makeQuery(id+"F4.imprint","IMPRINT",EDGE,{"derivedFrom":sQuery(id+"F4.wireOp",EDGE,"E7.8.6.0")}),1.0]])]});
            var Q188;
            Q188=makeQuery(id+"F4.imprint","IMPRINT",FACE,{"disambiguationData":[TD([[makeQuery(id+"F4.imprint","IMPRINT",EDGE,{"derivedFrom":sQuery(id+"F4.wireOp",EDGE,"E7.7.15.0")}),1.0]])]});
            var Q189;
            Q189=makeQuery(id+"F4.imprint","IMPRINT",FACE,{"disambiguationData":[TD([[makeQuery(id+"F4.imprint","IMPRINT",EDGE,{"derivedFrom":sQuery(id+"F4.wireOp",EDGE,"E7.11.11.0")}),1.0]])]});
            var Q190;
            Q190=makeQuery(id+"F4.imprint","IMPRINT",FACE,{"disambiguationData":[TD([[makeQuery(id+"F4.imprint","IMPRINT",EDGE,{"derivedFrom":sQuery(id+"F4.wireOp",EDGE,"E7.10.20.0")}),1.0]])]});
            var Q191;
            Q191=makeQuery(id+"F4.imprint","IMPRINT",FACE,{"disambiguationData":[TD([[makeQuery(id+"F4.imprint","IMPRINT",EDGE,{"derivedFrom":sQuery(id+"F4.wireOp",EDGE,"E7.10.4.0")}),1.0]])]});
            var Q192;
            Q192=makeQuery(id+"F4.imprint","IMPRINT",FACE,{"disambiguationData":[TD([[makeQuery(id+"F4.imprint","IMPRINT",EDGE,{"derivedFrom":sQuery(id+"F4.wireOp",EDGE,"E7.9.13.0")}),1.0]])]});
            var Q193;
            Q193=makeQuery(id+"F4.imprint","IMPRINT",FACE,{"disambiguationData":[TD([[makeQuery(id+"F4.imprint","IMPRINT",EDGE,{"derivedFrom":sQuery(id+"F4.wireOp",EDGE,"E7.14.0.0")}),1.0]])]});
            var Q194;
            Q194=makeQuery(id+"F4.imprint","IMPRINT",FACE,{"disambiguationData":[TD([[makeQuery(id+"F4.imprint","IMPRINT",EDGE,{"derivedFrom":sQuery(id+"F4.wireOp",EDGE,"E7.13.9.0")}),1.0]])]});
            var Q195;
            Q195=makeQuery(id+"F4.imprint","IMPRINT",FACE,{"disambiguationData":[TD([[makeQuery(id+"F4.imprint","IMPRINT",EDGE,{"derivedFrom":sQuery(id+"F4.wireOp",EDGE,"E7.12.18.0")}),1.0]])]});
            var Q196;
            Q196=makeQuery(id+"F4.imprint","IMPRINT",FACE,{"disambiguationData":[TD([[makeQuery(id+"F4.imprint","IMPRINT",EDGE,{"derivedFrom":sQuery(id+"F4.wireOp",EDGE,"E7.12.2.0")}),1.0]])]});
            var Q197;
            Q197=makeQuery(id+"F4.imprint","IMPRINT",FACE,{"disambiguationData":[TD([[makeQuery(id+"F4.imprint","IMPRINT",EDGE,{"derivedFrom":sQuery(id+"F4.wireOp",EDGE,"E7.16.14.0")}),1.0]])]});
            var Q198;
            Q198=makeQuery(id+"F4.imprint","IMPRINT",FACE,{"disambiguationData":[TD([[makeQuery(id+"F4.imprint","IMPRINT",EDGE,{"derivedFrom":sQuery(id+"F4.wireOp",EDGE,"E7.15.23.0")}),1.0]])]});
            var Q199;
            Q199=makeQuery(id+"F4.imprint","IMPRINT",FACE,{"disambiguationData":[TD([[makeQuery(id+"F4.imprint","IMPRINT",EDGE,{"derivedFrom":sQuery(id+"F4.wireOp",EDGE,"E7.15.7.0")}),1.0]])]});
            var Q200;
            Q200=makeQuery(id+"F4.imprint","IMPRINT",FACE,{"disambiguationData":[TD([[makeQuery(id+"F4.imprint","IMPRINT",EDGE,{"derivedFrom":sQuery(id+"F4.wireOp",EDGE,"E7.14.16.0")}),1.0]])]});
            var Q201;
            Q201=makeQuery(id+"F4.imprint","IMPRINT",FACE,{"disambiguationData":[TD([[makeQuery(id+"F4.imprint","IMPRINT",EDGE,{"derivedFrom":sQuery(id+"F4.wireOp",EDGE,"E7.17.21.0")}),1.0]])]});
            var Q202;
            Q202=makeQuery(id+"F4.imprint","IMPRINT",FACE,{"disambiguationData":[TD([[makeQuery(id+"F4.imprint","IMPRINT",EDGE,{"derivedFrom":sQuery(id+"F4.wireOp",EDGE,"E7.20.10.0")}),1.0]])]});
            var Q203;
            Q203=makeQuery(id+"F4.imprint","IMPRINT",FACE,{"disambiguationData":[TD([[makeQuery(id+"F4.imprint","IMPRINT",EDGE,{"derivedFrom":sQuery(id+"F4.wireOp",EDGE,"E7.19.19.0")}),1.0]])]});
            var Q204;
            Q204=makeQuery(id+"F4.imprint","IMPRINT",FACE,{"disambiguationData":[TD([[makeQuery(id+"F4.imprint","IMPRINT",EDGE,{"derivedFrom":sQuery(id+"F4.wireOp",EDGE,"E7.18.12.0")}),1.0]])]});
            var Q205;
            Q205=makeQuery(id+"F4.imprint","IMPRINT",FACE,{"disambiguationData":[TD([[makeQuery(id+"F4.imprint","IMPRINT",EDGE,{"derivedFrom":sQuery(id+"F4.wireOp",EDGE,"E7.22.8.0")}),1.0]])]});
            var Q206;
            Q206=makeQuery(id+"F4.imprint","IMPRINT",FACE,{"disambiguationData":[TD([[makeQuery(id+"F4.imprint","IMPRINT",EDGE,{"derivedFrom":sQuery(id+"F4.wireOp",EDGE,"E7.21.17.0")}),1.0]])]});
            var Q207;
            Q207=makeQuery(id+"F4.imprint","IMPRINT",FACE,{"disambiguationData":[TD([[makeQuery(id+"F4.imprint","IMPRINT",EDGE,{"derivedFrom":sQuery(id+"F4.wireOp",EDGE,"E7.21.1.0")}),1.0]])]});
            var Q208;
            Q208=makeQuery(id+"F4.imprint","IMPRINT",FACE,{"disambiguationData":[TD([[makeQuery(id+"F4.imprint","IMPRINT",EDGE,{"derivedFrom":sQuery(id+"F4.wireOp",EDGE,"E7.24.6.0")}),1.0]])]});
            var Q209;
            Q209=makeQuery(id+"F4.imprint","IMPRINT",FACE,{"disambiguationData":[TD([[makeQuery(id+"F4.imprint","IMPRINT",EDGE,{"derivedFrom":sQuery(id+"F4.wireOp",EDGE,"E7.23.15.0")}),1.0]])]});
            var Q210;
            Q210=makeQuery(id+"F4.imprint","IMPRINT",FACE,{"disambiguationData":[TD([[makeQuery(id+"F4.imprint","IMPRINT",EDGE,{"derivedFrom":sQuery(id+"F4.wireOp",EDGE,"E7.17.23.0")}),1.0]])]});
            var Q211;
            Q211=makeQuery(id+"F4.imprint","IMPRINT",FACE,{"disambiguationData":[TD([[makeQuery(id+"F4.imprint","IMPRINT",EDGE,{"derivedFrom":sQuery(id+"F4.wireOp",EDGE,"E7.17.7.0")}),1.0]])]});
            var Q212;
            Q212=makeQuery(id+"F4.imprint","IMPRINT",FACE,{"disambiguationData":[TD([[makeQuery(id+"F4.imprint","IMPRINT",EDGE,{"derivedFrom":sQuery(id+"F4.wireOp",EDGE,"E7.16.16.0")}),1.0]])]});
            var Q213;
            Q213=makeQuery(id+"F4.imprint","IMPRINT",FACE,{"disambiguationData":[TD([[makeQuery(id+"F4.imprint","IMPRINT",EDGE,{"derivedFrom":sQuery(id+"F4.wireOp",EDGE,"E7.20.12.0")}),1.0]])]});
            var Q214;
            Q214=makeQuery(id+"F4.imprint","IMPRINT",FACE,{"disambiguationData":[TD([[makeQuery(id+"F4.imprint","IMPRINT",EDGE,{"derivedFrom":sQuery(id+"F4.wireOp",EDGE,"E7.19.21.0")}),1.0]])]});
            var Q215;
            Q215=makeQuery(id+"F4.imprint","IMPRINT",FACE,{"disambiguationData":[TD([[makeQuery(id+"F4.imprint","IMPRINT",EDGE,{"derivedFrom":sQuery(id+"F4.wireOp",EDGE,"E7.19.5.0")}),1.0]])]});
            var Q216;
            Q216=makeQuery(id+"F4.imprint","IMPRINT",FACE,{"disambiguationData":[TD([[makeQuery(id+"F4.imprint","IMPRINT",EDGE,{"derivedFrom":sQuery(id+"F4.wireOp",EDGE,"E7.18.14.0")}),1.0]])]});
            var Q217;
            Q217=makeQuery(id+"F4.imprint","IMPRINT",FACE,{"disambiguationData":[TD([[makeQuery(id+"F4.imprint","IMPRINT",EDGE,{"derivedFrom":sQuery(id+"F4.wireOp",EDGE,"E7.23.1.0")}),1.0]])]});
            var Q218;
            Q218=makeQuery(id+"F4.imprint","IMPRINT",FACE,{"disambiguationData":[TD([[makeQuery(id+"F4.imprint","IMPRINT",EDGE,{"derivedFrom":sQuery(id+"F4.wireOp",EDGE,"E7.22.10.0")}),1.0]])]});
            var Q219;
            Q219=makeQuery(id+"F4.imprint","IMPRINT",FACE,{"disambiguationData":[TD([[makeQuery(id+"F4.imprint","IMPRINT",EDGE,{"derivedFrom":sQuery(id+"F4.wireOp",EDGE,"E7.21.19.0")}),1.0]])]});
            var Q220;
            Q220=makeQuery(id+"F4.imprint","IMPRINT",FACE,{"disambiguationData":[TD([[makeQuery(id+"F4.imprint","IMPRINT",EDGE,{"derivedFrom":sQuery(id+"F4.wireOp",EDGE,"E7.21.3.0")}),1.0]])]});
            var Q221;
            Q221=makeQuery(id+"F4.imprint","IMPRINT",FACE,{"disambiguationData":[TD([[makeQuery(id+"F4.imprint","IMPRINT",EDGE,{"derivedFrom":sQuery(id+"F4.wireOp",EDGE,"E7.24.8.0")}),1.0]])]});
            var Q222;
            Q222=makeQuery(id+"F4.imprint","IMPRINT",FACE,{"disambiguationData":[TD([[makeQuery(id+"F4.imprint","IMPRINT",EDGE,{"derivedFrom":sQuery(id+"F4.wireOp",EDGE,"E7.23.17.0")}),1.0]])]});
            var Q223;
            Q223=makeQuery(id+"F4.imprint","IMPRINT",FACE,{"disambiguationData":[TD([[makeQuery(id+"F4.imprint","IMPRINT",EDGE,{"derivedFrom":sQuery(id+"F4.wireOp",EDGE,"E7.1.7.0")}),1.0]])]});
            var Q224;
            Q224=makeQuery(id+"F4.imprint","IMPRINT",FACE,{"disambiguationData":[TD([[makeQuery(id+"F4.imprint","IMPRINT",EDGE,{"derivedFrom":sQuery(id+"F4.wireOp",EDGE,"E7.3.21.0")}),1.0]])]});
            var Q225;
            Q225=makeQuery(id+"F4.imprint","IMPRINT",FACE,{"disambiguationData":[TD([[makeQuery(id+"F4.imprint","IMPRINT",EDGE,{"derivedFrom":sQuery(id+"F4.wireOp",EDGE,"E7.3.5.0")}),1.0]])]});
            var Q226;
            Q226=makeQuery(id+"F4.imprint","IMPRINT",FACE,{"disambiguationData":[TD([[makeQuery(id+"F4.imprint","IMPRINT",EDGE,{"derivedFrom":sQuery(id+"F4.wireOp",EDGE,"E7.1.23.0")}),1.0]])]});
            var Q227;
            Q227=makeQuery(id+"F4.imprint","IMPRINT",FACE,{"disambiguationData":[TD([[makeQuery(id+"F4.imprint","IMPRINT",EDGE,{"derivedFrom":sQuery(id+"F4.wireOp",EDGE,"E7.6.10.0")}),1.0]])]});
            var Q228;
            Q228=makeQuery(id+"F4.imprint","IMPRINT",FACE,{"disambiguationData":[TD([[makeQuery(id+"F4.imprint","IMPRINT",EDGE,{"derivedFrom":sQuery(id+"F4.wireOp",EDGE,"E7.5.19.0")}),1.0]])]});
            var Q229;
            Q229=makeQuery(id+"F4.imprint","IMPRINT",FACE,{"disambiguationData":[TD([[makeQuery(id+"F4.imprint","IMPRINT",EDGE,{"derivedFrom":sQuery(id+"F4.wireOp",EDGE,"E7.5.3.0")}),1.0]])]});
            var Q230;
            Q230=makeQuery(id+"F4.imprint","IMPRINT",FACE,{"disambiguationData":[TD([[makeQuery(id+"F4.imprint","IMPRINT",EDGE,{"derivedFrom":sQuery(id+"F4.wireOp",EDGE,"E7.8.8.0")}),1.0]])]});
            var Q231;
            Q231=makeQuery(id+"F4.imprint","IMPRINT",FACE,{"disambiguationData":[TD([[makeQuery(id+"F4.imprint","IMPRINT",EDGE,{"derivedFrom":sQuery(id+"F4.wireOp",EDGE,"E7.7.17.0")}),1.0]])]});
            var Q232;
            Q232=makeQuery(id+"F4.imprint","IMPRINT",FACE,{"disambiguationData":[TD([[makeQuery(id+"F4.imprint","IMPRINT",EDGE,{"derivedFrom":sQuery(id+"F4.wireOp",EDGE,"E7.7.1.0")}),1.0]])]});
            var Q233;
            Q233=makeQuery(id+"F4.imprint","IMPRINT",FACE,{"disambiguationData":[TD([[makeQuery(id+"F4.imprint","IMPRINT",EDGE,{"derivedFrom":sQuery(id+"F4.wireOp",EDGE,"E7.11.13.0")}),1.0]])]});
            var Q234;
            Q234=makeQuery(id+"F4.imprint","IMPRINT",FACE,{"disambiguationData":[TD([[makeQuery(id+"F4.imprint","IMPRINT",EDGE,{"derivedFrom":sQuery(id+"F4.wireOp",EDGE,"E7.10.22.0")}),1.0]])]});
            var Q235;
            Q235=makeQuery(id+"F4.imprint","IMPRINT",FACE,{"disambiguationData":[TD([[makeQuery(id+"F4.imprint","IMPRINT",EDGE,{"derivedFrom":sQuery(id+"F4.wireOp",EDGE,"E7.10.6.0")}),1.0]])]});
            var Q236;
            Q236=makeQuery(id+"F4.imprint","IMPRINT",FACE,{"disambiguationData":[TD([[makeQuery(id+"F4.imprint","IMPRINT",EDGE,{"derivedFrom":sQuery(id+"F4.wireOp",EDGE,"E7.9.15.0")}),1.0]])]});
            var Q237;
            Q237=makeQuery(id+"F4.imprint","IMPRINT",FACE,{"disambiguationData":[TD([[makeQuery(id+"F4.imprint","IMPRINT",EDGE,{"derivedFrom":sQuery(id+"F4.wireOp",EDGE,"E7.14.2.0")}),1.0]])]});
            var Q238;
            Q238=makeQuery(id+"F4.imprint","IMPRINT",FACE,{"disambiguationData":[TD([[makeQuery(id+"F4.imprint","IMPRINT",EDGE,{"derivedFrom":sQuery(id+"F4.wireOp",EDGE,"E7.13.11.0")}),1.0]])]});
            var Q239;
            Q239=makeQuery(id+"F4.imprint","IMPRINT",FACE,{"disambiguationData":[TD([[makeQuery(id+"F4.imprint","IMPRINT",EDGE,{"derivedFrom":sQuery(id+"F4.wireOp",EDGE,"E7.12.20.0")}),1.0]])]});
            var Q240;
            Q240=makeQuery(id+"F4.imprint","IMPRINT",FACE,{"disambiguationData":[TD([[makeQuery(id+"F4.imprint","IMPRINT",EDGE,{"derivedFrom":sQuery(id+"F4.wireOp",EDGE,"E7.12.4.0")}),1.0]])]});
            var Q241;
            Q241=makeQuery(id+"F4.imprint","IMPRINT",FACE,{"disambiguationData":[TD([[makeQuery(id+"F4.imprint","IMPRINT",EDGE,{"derivedFrom":sQuery(id+"F4.wireOp",EDGE,"E7.16.0.0")}),1.0]])]});
            var Q242;
            Q242=makeQuery(id+"F4.imprint","IMPRINT",FACE,{"disambiguationData":[TD([[makeQuery(id+"F4.imprint","IMPRINT",EDGE,{"derivedFrom":sQuery(id+"F4.wireOp",EDGE,"E7.15.9.0")}),1.0]])]});
            var Q243;
            Q243=makeQuery(id+"F4.imprint","IMPRINT",FACE,{"disambiguationData":[TD([[makeQuery(id+"F4.imprint","IMPRINT",EDGE,{"derivedFrom":sQuery(id+"F4.wireOp",EDGE,"E7.14.18.0")}),1.0]])]});
            var Q244;
            Q244=makeQuery(id+"F4.imprint","IMPRINT",FACE,{"disambiguationData":[TD([[makeQuery(id+"F4.imprint","IMPRINT",EDGE,{"derivedFrom":sQuery(id+"F4.wireOp",EDGE,"E7.1.8.0")}),1.0]])]});
            var Q245;
            Q245=makeQuery(id+"F4.imprint","IMPRINT",FACE,{"disambiguationData":[TD([[makeQuery(id+"F4.imprint","IMPRINT",EDGE,{"derivedFrom":sQuery(id+"F4.wireOp",EDGE,"E7.0.17.0")}),1.0]])]});
            var Q246;
            Q246=makeQuery(id+"F4.imprint","IMPRINT",FACE,{"disambiguationData":[TD([[makeQuery(id+"F4.imprint","IMPRINT",EDGE,{"derivedFrom":sQuery(id+"F4.wireOp",EDGE,"E7.20.13.0")}),1.0]])]});
            var Q247;
            Q247=makeQuery(id+"F4.imprint","IMPRINT",FACE,{"disambiguationData":[TD([[makeQuery(id+"F4.imprint","IMPRINT",EDGE,{"derivedFrom":sQuery(id+"F4.wireOp",EDGE,"E7.19.6.0")}),1.0]])]});
            var Q248;
            Q248=makeQuery(id+"F4.imprint","IMPRINT",FACE,{"disambiguationData":[TD([[makeQuery(id+"F4.imprint","IMPRINT",EDGE,{"derivedFrom":sQuery(id+"F4.wireOp",EDGE,"E7.18.15.0")}),1.0]])]});
            var Q249;
            Q249=makeQuery(id+"F4.imprint","IMPRINT",FACE,{"disambiguationData":[TD([[makeQuery(id+"F4.imprint","IMPRINT",EDGE,{"derivedFrom":sQuery(id+"F4.wireOp",EDGE,"E7.23.2.0")}),1.0]])]});
            var Q250;
            Q250=makeQuery(id+"F4.imprint","IMPRINT",FACE,{"disambiguationData":[TD([[makeQuery(id+"F4.imprint","IMPRINT",EDGE,{"derivedFrom":sQuery(id+"F4.wireOp",EDGE,"E7.22.11.0")}),1.0]])]});
            var Q251;
            Q251=makeQuery(id+"F4.imprint","IMPRINT",FACE,{"disambiguationData":[TD([[makeQuery(id+"F4.imprint","IMPRINT",EDGE,{"derivedFrom":sQuery(id+"F4.wireOp",EDGE,"E7.21.20.0")}),1.0]])]});
            var Q252;
            Q252=makeQuery(id+"F4.imprint","IMPRINT",FACE,{"disambiguationData":[TD([[makeQuery(id+"F4.imprint","IMPRINT",EDGE,{"derivedFrom":sQuery(id+"F4.wireOp",EDGE,"E7.21.4.0")}),1.0]])]});
            var Q253;
            Q253=makeQuery(id+"F4.imprint","IMPRINT",FACE,{"disambiguationData":[TD([[makeQuery(id+"F4.imprint","IMPRINT",EDGE,{"derivedFrom":sQuery(id+"F4.wireOp",EDGE,"E7.24.9.0")}),1.0]])]});
            var Q254;
            Q254=makeQuery(id+"F4.imprint","IMPRINT",FACE,{"disambiguationData":[TD([[makeQuery(id+"F4.imprint","IMPRINT",EDGE,{"derivedFrom":sQuery(id+"F4.wireOp",EDGE,"E7.23.18.0")}),1.0]])]});
            var Q255;
            Q255=makeQuery(id+"F4.imprint","IMPRINT",FACE,{"disambiguationData":[TD([[makeQuery(id+"F4.imprint","IMPRINT",EDGE,{"derivedFrom":sQuery(id+"F4.wireOp",EDGE,"E7.3.22.0")}),1.0]])]});
            var Q256;
            Q256=makeQuery(id+"F4.imprint","IMPRINT",FACE,{"disambiguationData":[TD([[makeQuery(id+"F4.imprint","IMPRINT",EDGE,{"derivedFrom":sQuery(id+"F4.wireOp",EDGE,"E7.3.6.0")}),1.0]])]});
            var Q257;
            Q257=makeQuery(id+"F4.imprint","IMPRINT",FACE,{"disambiguationData":[TD([[makeQuery(id+"F4.imprint","IMPRINT",EDGE,{"derivedFrom":sQuery(id+"F4.wireOp",EDGE,"E7.2.15.0")}),1.0]])]});
            var Q258;
            Q258=makeQuery(id+"F4.imprint","IMPRINT",FACE,{"disambiguationData":[TD([[makeQuery(id+"F4.imprint","IMPRINT",EDGE,{"derivedFrom":sQuery(id+"F4.wireOp",EDGE,"E7.1.24.0")}),1.0]])]});
            var Q259;
            Q259=makeQuery(id+"F4.imprint","IMPRINT",FACE,{"disambiguationData":[TD([[makeQuery(id+"F4.imprint","IMPRINT",EDGE,{"derivedFrom":sQuery(id+"F4.wireOp",EDGE,"E7.6.11.0")}),1.0]])]});
            var Q260;
            Q260=makeQuery(id+"F4.imprint","IMPRINT",FACE,{"disambiguationData":[TD([[makeQuery(id+"F4.imprint","IMPRINT",EDGE,{"derivedFrom":sQuery(id+"F4.wireOp",EDGE,"E7.5.20.0")}),1.0]])]});
            var Q261;
            Q261=makeQuery(id+"F4.imprint","IMPRINT",FACE,{"disambiguationData":[TD([[makeQuery(id+"F4.imprint","IMPRINT",EDGE,{"derivedFrom":sQuery(id+"F4.wireOp",EDGE,"E7.5.4.0")}),1.0]])]});
            var Q262;
            Q262=makeQuery(id+"F4.imprint","IMPRINT",FACE,{"disambiguationData":[TD([[makeQuery(id+"F4.imprint","IMPRINT",EDGE,{"derivedFrom":sQuery(id+"F4.wireOp",EDGE,"E7.4.13.0")}),1.0]])]});
            var Q263;
            Q263=makeQuery(id+"F4.imprint","IMPRINT",FACE,{"disambiguationData":[TD([[makeQuery(id+"F4.imprint","IMPRINT",EDGE,{"derivedFrom":sQuery(id+"F4.wireOp",EDGE,"E7.9.0.0")}),1.0]])]});
            var Q264;
            Q264=makeQuery(id+"F4.imprint","IMPRINT",FACE,{"disambiguationData":[TD([[makeQuery(id+"F4.imprint","IMPRINT",EDGE,{"derivedFrom":sQuery(id+"F4.wireOp",EDGE,"E7.8.9.0")}),1.0]])]});
            var Q265;
            Q265=makeQuery(id+"F4.imprint","IMPRINT",FACE,{"disambiguationData":[TD([[makeQuery(id+"F4.imprint","IMPRINT",EDGE,{"derivedFrom":sQuery(id+"F4.wireOp",EDGE,"E7.7.18.0")}),1.0]])]});
            var Q266;
            Q266=makeQuery(id+"F4.imprint","IMPRINT",FACE,{"disambiguationData":[TD([[makeQuery(id+"F4.imprint","IMPRINT",EDGE,{"derivedFrom":sQuery(id+"F4.wireOp",EDGE,"E7.7.2.0")}),1.0]])]});
            var Q267;
            Q267=makeQuery(id+"F4.imprint","IMPRINT",FACE,{"disambiguationData":[TD([[makeQuery(id+"F4.imprint","IMPRINT",EDGE,{"derivedFrom":sQuery(id+"F4.wireOp",EDGE,"E7.10.23.0")}),1.0]])]});
            var Q268;
            Q268=makeQuery(id+"F4.imprint","IMPRINT",FACE,{"disambiguationData":[TD([[makeQuery(id+"F4.imprint","IMPRINT",EDGE,{"derivedFrom":sQuery(id+"F4.wireOp",EDGE,"E7.10.7.0")}),1.0]])]});
            var Q269;
            Q269=makeQuery(id+"F4.imprint","IMPRINT",FACE,{"disambiguationData":[TD([[makeQuery(id+"F4.imprint","IMPRINT",EDGE,{"derivedFrom":sQuery(id+"F4.wireOp",EDGE,"E7.9.16.0")}),1.0]])]});
            var Q270;
            Q270=makeQuery(id+"F4.imprint","IMPRINT",FACE,{"disambiguationData":[TD([[makeQuery(id+"F4.imprint","IMPRINT",EDGE,{"derivedFrom":sQuery(id+"F4.wireOp",EDGE,"E7.14.3.0")}),1.0]])]});
            var Q271;
            Q271=makeQuery(id+"F4.imprint","IMPRINT",FACE,{"disambiguationData":[TD([[makeQuery(id+"F4.imprint","IMPRINT",EDGE,{"derivedFrom":sQuery(id+"F4.wireOp",EDGE,"E7.13.12.0")}),1.0]])]});
            var Q272;
            Q272=makeQuery(id+"F4.imprint","IMPRINT",FACE,{"disambiguationData":[TD([[makeQuery(id+"F4.imprint","IMPRINT",EDGE,{"derivedFrom":sQuery(id+"F4.wireOp",EDGE,"E7.12.21.0")}),1.0]])]});
            var Q273;
            Q273=makeQuery(id+"F4.imprint","IMPRINT",FACE,{"disambiguationData":[TD([[makeQuery(id+"F4.imprint","IMPRINT",EDGE,{"derivedFrom":sQuery(id+"F4.wireOp",EDGE,"E7.12.5.0")}),1.0]])]});
            var Q274;
            Q274=makeQuery(id+"F4.imprint","IMPRINT",FACE,{"disambiguationData":[TD([[makeQuery(id+"F4.imprint","IMPRINT",EDGE,{"derivedFrom":sQuery(id+"F4.wireOp",EDGE,"E7.16.1.0")}),1.0]])]});
            var Q275;
            Q275=makeQuery(id+"F4.imprint","IMPRINT",FACE,{"disambiguationData":[TD([[makeQuery(id+"F4.imprint","IMPRINT",EDGE,{"derivedFrom":sQuery(id+"F4.wireOp",EDGE,"E7.14.19.0")}),1.0]])]});
            var Q276;
            Q276=makeQuery(id+"F4.imprint","IMPRINT",FACE,{"disambiguationData":[TD([[makeQuery(id+"F4.imprint","IMPRINT",EDGE,{"derivedFrom":sQuery(id+"F4.wireOp",EDGE,"E7.17.8.0")}),1.0]])]});
            var Q277;
            Q277=makeQuery(id+"F4.imprint","IMPRINT",FACE,{"disambiguationData":[TD([[makeQuery(id+"F4.imprint","IMPRINT",EDGE,{"derivedFrom":sQuery(id+"F4.wireOp",EDGE,"E7.16.17.0")}),1.0]])]});
            var Q278;
            Q278=makeQuery(id+"F4.imprint","IMPRINT",FACE,{"disambiguationData":[TD([[makeQuery(id+"F4.imprint","IMPRINT",EDGE,{"derivedFrom":sQuery(id+"F4.wireOp",EDGE,"E7.1.9.0")}),1.0]])]});
            var Q279;
            Q279=makeQuery(id+"F4.imprint","IMPRINT",FACE,{"disambiguationData":[TD([[makeQuery(id+"F4.imprint","IMPRINT",EDGE,{"derivedFrom":sQuery(id+"F4.wireOp",EDGE,"E7.3.23.0")}),1.0]])]});
            var Q280;
            Q280=makeQuery(id+"F4.imprint","IMPRINT",FACE,{"disambiguationData":[TD([[makeQuery(id+"F4.imprint","IMPRINT",EDGE,{"derivedFrom":sQuery(id+"F4.wireOp",EDGE,"E7.3.7.0")}),1.0]])]});
            var Q281;
            Q281=makeQuery(id+"F4.imprint","IMPRINT",FACE,{"disambiguationData":[TD([[makeQuery(id+"F4.imprint","IMPRINT",EDGE,{"derivedFrom":sQuery(id+"F4.wireOp",EDGE,"E7.2.0.0")}),1.0]])]});
            var Q282;
            Q282=makeQuery(id+"F4.imprint","IMPRINT",FACE,{"disambiguationData":[TD([[makeQuery(id+"F4.imprint","IMPRINT",EDGE,{"derivedFrom":sQuery(id+"F4.wireOp",EDGE,"E7.23.3.0")}),1.0]])]});
            var Q283;
            Q283=makeQuery(id+"F4.imprint","IMPRINT",FACE,{"disambiguationData":[TD([[makeQuery(id+"F4.imprint","IMPRINT",EDGE,{"derivedFrom":sQuery(id+"F4.wireOp",EDGE,"E7.22.12.0")}),1.0]])]});
            var Q284;
            Q284=makeQuery(id+"F4.imprint","IMPRINT",FACE,{"disambiguationData":[TD([[makeQuery(id+"F4.imprint","IMPRINT",EDGE,{"derivedFrom":sQuery(id+"F4.wireOp",EDGE,"E7.21.21.0")}),1.0]])]});
            var Q285;
            Q285=makeQuery(id+"F4.imprint","IMPRINT",FACE,{"disambiguationData":[TD([[makeQuery(id+"F4.imprint","IMPRINT",EDGE,{"derivedFrom":sQuery(id+"F4.wireOp",EDGE,"E7.21.5.0")}),1.0]])]});
            var Q286;
            Q286=makeQuery(id+"F4.imprint","IMPRINT",FACE,{"disambiguationData":[TD([[makeQuery(id+"F4.imprint","IMPRINT",EDGE,{"derivedFrom":sQuery(id+"F4.wireOp",EDGE,"E7.24.10.0")}),1.0]])]});
            var Q287;
            Q287=makeQuery(id+"F4.imprint","IMPRINT",FACE,{"disambiguationData":[TD([[makeQuery(id+"F4.imprint","IMPRINT",EDGE,{"derivedFrom":sQuery(id+"F4.wireOp",EDGE,"E7.23.19.0")}),1.0]])]});
            var Q288;
            Q288=makeQuery(id+"F4.imprint","IMPRINT",FACE,{"disambiguationData":[TD([[makeQuery(id+"F4.imprint","IMPRINT",EDGE,{"derivedFrom":sQuery(id+"F4.wireOp",EDGE,"E7.5.21.0")}),1.0]])]});
            var Q289;
            Q289=makeQuery(id+"F4.imprint","IMPRINT",FACE,{"disambiguationData":[TD([[makeQuery(id+"F4.imprint","IMPRINT",EDGE,{"derivedFrom":sQuery(id+"F4.wireOp",EDGE,"E7.5.5.0")}),1.0]])]});
            var Q290;
            Q290=makeQuery(id+"F4.imprint","IMPRINT",FACE,{"disambiguationData":[TD([[makeQuery(id+"F4.imprint","IMPRINT",EDGE,{"derivedFrom":sQuery(id+"F4.wireOp",EDGE,"E7.9.1.0")}),1.0]])]});
            var Q291;
            Q291=makeQuery(id+"F4.imprint","IMPRINT",FACE,{"disambiguationData":[TD([[makeQuery(id+"F4.imprint","IMPRINT",EDGE,{"derivedFrom":sQuery(id+"F4.wireOp",EDGE,"E7.8.10.0")}),1.0]])]});
            var Q292;
            Q292=makeQuery(id+"F4.imprint","IMPRINT",FACE,{"disambiguationData":[TD([[makeQuery(id+"F4.imprint","IMPRINT",EDGE,{"derivedFrom":sQuery(id+"F4.wireOp",EDGE,"E7.7.19.0")}),1.0]])]});
            var Q293;
            Q293=makeQuery(id+"F4.imprint","IMPRINT",FACE,{"disambiguationData":[TD([[makeQuery(id+"F4.imprint","IMPRINT",EDGE,{"derivedFrom":sQuery(id+"F4.wireOp",EDGE,"E7.7.3.0")}),1.0]])]});
            var Q294;
            Q294=makeQuery(id+"F4.imprint","IMPRINT",FACE,{"disambiguationData":[TD([[makeQuery(id+"F4.imprint","IMPRINT",EDGE,{"derivedFrom":sQuery(id+"F4.wireOp",EDGE,"E7.11.15.0")}),1.0]])]});
            var Q295;
            Q295=makeQuery(id+"F4.imprint","IMPRINT",FACE,{"disambiguationData":[TD([[makeQuery(id+"F4.imprint","IMPRINT",EDGE,{"derivedFrom":sQuery(id+"F4.wireOp",EDGE,"E7.10.24.0")}),1.0]])]});
            var Q296;
            Q296=makeQuery(id+"F4.imprint","IMPRINT",FACE,{"disambiguationData":[TD([[makeQuery(id+"F4.imprint","IMPRINT",EDGE,{"derivedFrom":sQuery(id+"F4.wireOp",EDGE,"E7.10.8.0")}),1.0]])]});
            var Q297;
            Q297=makeQuery(id+"F4.imprint","IMPRINT",FACE,{"disambiguationData":[TD([[makeQuery(id+"F4.imprint","IMPRINT",EDGE,{"derivedFrom":sQuery(id+"F4.wireOp",EDGE,"E7.9.17.0")}),1.0]])]});
            var Q298;
            Q298=makeQuery(id+"F4.imprint","IMPRINT",FACE,{"disambiguationData":[TD([[makeQuery(id+"F4.imprint","IMPRINT",EDGE,{"derivedFrom":sQuery(id+"F4.wireOp",EDGE,"E7.14.4.0")}),1.0]])]});
            var Q299;
            Q299=makeQuery(id+"F4.imprint","IMPRINT",FACE,{"disambiguationData":[TD([[makeQuery(id+"F4.imprint","IMPRINT",EDGE,{"derivedFrom":sQuery(id+"F4.wireOp",EDGE,"E7.13.13.0")}),1.0]])]});
            var Q300;
            Q300=makeQuery(id+"F4.imprint","IMPRINT",FACE,{"disambiguationData":[TD([[makeQuery(id+"F4.imprint","IMPRINT",EDGE,{"derivedFrom":sQuery(id+"F4.wireOp",EDGE,"E7.12.22.0")}),1.0]])]});
            var Q301;
            Q301=makeQuery(id+"F4.imprint","IMPRINT",FACE,{"disambiguationData":[TD([[makeQuery(id+"F4.imprint","IMPRINT",EDGE,{"derivedFrom":sQuery(id+"F4.wireOp",EDGE,"E7.12.6.0")}),1.0]])]});
            var Q302;
            Q302=makeQuery(id+"F4.imprint","IMPRINT",FACE,{"disambiguationData":[TD([[makeQuery(id+"F4.imprint","IMPRINT",EDGE,{"derivedFrom":sQuery(id+"F4.wireOp",EDGE,"E7.16.2.0")}),1.0]])]});
            var Q303;
            Q303=makeQuery(id+"F4.imprint","IMPRINT",FACE,{"disambiguationData":[TD([[makeQuery(id+"F4.imprint","IMPRINT",EDGE,{"derivedFrom":sQuery(id+"F4.wireOp",EDGE,"E7.15.11.0")}),1.0]])]});
            var Q304;
            Q304=makeQuery(id+"F4.imprint","IMPRINT",FACE,{"disambiguationData":[TD([[makeQuery(id+"F4.imprint","IMPRINT",EDGE,{"derivedFrom":sQuery(id+"F4.wireOp",EDGE,"E7.14.20.0")}),1.0]])]});
            var Q305;
            Q305=makeQuery(id+"F4.imprint","IMPRINT",FACE,{"disambiguationData":[TD([[makeQuery(id+"F4.imprint","IMPRINT",EDGE,{"derivedFrom":sQuery(id+"F4.wireOp",EDGE,"E7.18.0.0")}),1.0]])]});
            var Q306;
            Q306=makeQuery(id+"F4.imprint","IMPRINT",FACE,{"disambiguationData":[TD([[makeQuery(id+"F4.imprint","IMPRINT",EDGE,{"derivedFrom":sQuery(id+"F4.wireOp",EDGE,"E7.17.9.0")}),1.0]])]});
            var Q307;
            Q307=makeQuery(id+"F4.imprint","IMPRINT",FACE,{"disambiguationData":[TD([[makeQuery(id+"F4.imprint","IMPRINT",EDGE,{"derivedFrom":sQuery(id+"F4.wireOp",EDGE,"E7.16.18.0")}),1.0]])]});
            var Q308;
            Q308=makeQuery(id+"F4.imprint","IMPRINT",FACE,{"disambiguationData":[TD([[makeQuery(id+"F4.imprint","IMPRINT",EDGE,{"derivedFrom":sQuery(id+"F4.wireOp",EDGE,"E7.20.14.0")}),1.0]])]});
            var Q309;
            Q309=makeQuery(id+"F4.imprint","IMPRINT",FACE,{"disambiguationData":[TD([[makeQuery(id+"F4.imprint","IMPRINT",EDGE,{"derivedFrom":sQuery(id+"F4.wireOp",EDGE,"E7.19.23.0")}),1.0]])]});
            var Q310;
            Q310=makeQuery(id+"F4.imprint","IMPRINT",FACE,{"disambiguationData":[TD([[makeQuery(id+"F4.imprint","IMPRINT",EDGE,{"derivedFrom":sQuery(id+"F4.wireOp",EDGE,"E7.19.7.0")}),1.0]])]});
            var Q311;
            Q311=makeQuery(id+"F4.imprint","IMPRINT",FACE,{"disambiguationData":[TD([[makeQuery(id+"F4.imprint","IMPRINT",EDGE,{"derivedFrom":sQuery(id+"F4.wireOp",EDGE,"E7.18.16.0")}),1.0]])]});
            var Q312;
            Q312=makeQuery(id+"F4.imprint","IMPRINT",FACE,{"disambiguationData":[TD([[makeQuery(id+"F4.imprint","IMPRINT",EDGE,{"derivedFrom":sQuery(id+"F4.wireOp",EDGE,"E7.1.10.0")}),1.0]])]});
            var Q313;
            Q313=makeQuery(id+"F4.imprint","IMPRINT",FACE,{"disambiguationData":[TD([[makeQuery(id+"F4.imprint","IMPRINT",EDGE,{"derivedFrom":sQuery(id+"F4.wireOp",EDGE,"E7.0.19.0")}),1.0]])]});
            var Q314;
            Q314=makeQuery(id+"F4.imprint","IMPRINT",FACE,{"disambiguationData":[TD([[makeQuery(id+"F4.imprint","IMPRINT",EDGE,{"derivedFrom":sQuery(id+"F4.wireOp",EDGE,"E7.3.24.0")}),1.0]])]});
            var Q315;
            Q315=makeQuery(id+"F4.imprint","IMPRINT",FACE,{"disambiguationData":[TD([[makeQuery(id+"F4.imprint","IMPRINT",EDGE,{"derivedFrom":sQuery(id+"F4.wireOp",EDGE,"E7.3.8.0")}),1.0]])]});
            var Q316;
            Q316=makeQuery(id+"F4.imprint","IMPRINT",FACE,{"disambiguationData":[TD([[makeQuery(id+"F4.imprint","IMPRINT",EDGE,{"derivedFrom":sQuery(id+"F4.wireOp",EDGE,"E7.2.17.0")}),1.0]])]});
            var Q317;
            Q317=makeQuery(id+"F4.imprint","IMPRINT",FACE,{"disambiguationData":[TD([[makeQuery(id+"F4.imprint","IMPRINT",EDGE,{"derivedFrom":sQuery(id+"F4.wireOp",EDGE,"E7.6.13.0")}),1.0]])]});
            var Q318;
            Q318=makeQuery(id+"F4.imprint","IMPRINT",FACE,{"disambiguationData":[TD([[makeQuery(id+"F4.imprint","IMPRINT",EDGE,{"derivedFrom":sQuery(id+"F4.wireOp",EDGE,"E7.5.22.0")}),1.0]])]});
            var Q319;
            Q319=makeQuery(id+"F4.imprint","IMPRINT",FACE,{"disambiguationData":[TD([[makeQuery(id+"F4.imprint","IMPRINT",EDGE,{"derivedFrom":sQuery(id+"F4.wireOp",EDGE,"E7.5.6.0")}),1.0]])]});
            var Q320;
            Q320=makeQuery(id+"F4.imprint","IMPRINT",FACE,{"disambiguationData":[TD([[makeQuery(id+"F4.imprint","IMPRINT",EDGE,{"derivedFrom":sQuery(id+"F4.wireOp",EDGE,"E7.4.15.0")}),1.0]])]});
            var Q321;
            Q321=makeQuery(id+"F4.imprint","IMPRINT",FACE,{"disambiguationData":[TD([[makeQuery(id+"F4.imprint","IMPRINT",EDGE,{"derivedFrom":sQuery(id+"F4.wireOp",EDGE,"E7.24.11.0")}),1.0]])]});
            var Q322;
            Q322=makeQuery(id+"F4.imprint","IMPRINT",FACE,{"disambiguationData":[TD([[makeQuery(id+"F4.imprint","IMPRINT",EDGE,{"derivedFrom":sQuery(id+"F4.wireOp",EDGE,"E7.23.20.0")}),1.0]])]});
            var Q323;
            Q323=makeQuery(id+"F4.imprint","IMPRINT",FACE,{"disambiguationData":[TD([[makeQuery(id+"F4.imprint","IMPRINT",EDGE,{"derivedFrom":sQuery(id+"F4.wireOp",EDGE,"E7.9.2.0")}),1.0]])]});
            var Q324;
            Q324=makeQuery(id+"F4.imprint","IMPRINT",FACE,{"disambiguationData":[TD([[makeQuery(id+"F4.imprint","IMPRINT",EDGE,{"derivedFrom":sQuery(id+"F4.wireOp",EDGE,"E7.8.11.0")}),1.0]])]});
            var Q325;
            Q325=makeQuery(id+"F4.imprint","IMPRINT",FACE,{"disambiguationData":[TD([[makeQuery(id+"F4.imprint","IMPRINT",EDGE,{"derivedFrom":sQuery(id+"F4.wireOp",EDGE,"E7.7.20.0")}),1.0]])]});
            var Q326;
            Q326=makeQuery(id+"F4.imprint","IMPRINT",FACE,{"disambiguationData":[TD([[makeQuery(id+"F4.imprint","IMPRINT",EDGE,{"derivedFrom":sQuery(id+"F4.wireOp",EDGE,"E7.7.4.0")}),1.0]])]});
            var Q327;
            Q327=makeQuery(id+"F4.imprint","IMPRINT",FACE,{"disambiguationData":[TD([[makeQuery(id+"F4.imprint","IMPRINT",EDGE,{"derivedFrom":sQuery(id+"F4.wireOp",EDGE,"E7.11.0.0")}),1.0]])]});
            var Q328;
            Q328=makeQuery(id+"F4.imprint","IMPRINT",FACE,{"disambiguationData":[TD([[makeQuery(id+"F4.imprint","IMPRINT",EDGE,{"derivedFrom":sQuery(id+"F4.wireOp",EDGE,"E7.10.9.0")}),1.0]])]});
            var Q329;
            Q329=makeQuery(id+"F4.imprint","IMPRINT",FACE,{"disambiguationData":[TD([[makeQuery(id+"F4.imprint","IMPRINT",EDGE,{"derivedFrom":sQuery(id+"F4.wireOp",EDGE,"E7.9.18.0")}),1.0]])]});
            var Q330;
            Q330=makeQuery(id+"F4.imprint","IMPRINT",FACE,{"disambiguationData":[TD([[makeQuery(id+"F4.imprint","IMPRINT",EDGE,{"derivedFrom":sQuery(id+"F4.wireOp",EDGE,"E7.14.5.0")}),1.0]])]});
            var Q331;
            Q331=makeQuery(id+"F4.imprint","IMPRINT",FACE,{"disambiguationData":[TD([[makeQuery(id+"F4.imprint","IMPRINT",EDGE,{"derivedFrom":sQuery(id+"F4.wireOp",EDGE,"E7.12.23.0")}),1.0]])]});
            var Q332;
            Q332=makeQuery(id+"F4.imprint","IMPRINT",FACE,{"disambiguationData":[TD([[makeQuery(id+"F4.imprint","IMPRINT",EDGE,{"derivedFrom":sQuery(id+"F4.wireOp",EDGE,"E7.12.7.0")}),1.0]])]});
            var Q333;
            Q333=makeQuery(id+"F4.imprint","IMPRINT",FACE,{"disambiguationData":[TD([[makeQuery(id+"F4.imprint","IMPRINT",EDGE,{"derivedFrom":sQuery(id+"F4.wireOp",EDGE,"E7.16.3.0")}),1.0]])]});
            var Q334;
            Q334=makeQuery(id+"F4.imprint","IMPRINT",FACE,{"disambiguationData":[TD([[makeQuery(id+"F4.imprint","IMPRINT",EDGE,{"derivedFrom":sQuery(id+"F4.wireOp",EDGE,"E7.14.21.0")}),1.0]])]});
            var Q335;
            Q335=makeQuery(id+"F4.imprint","IMPRINT",FACE,{"disambiguationData":[TD([[makeQuery(id+"F4.imprint","IMPRINT",EDGE,{"derivedFrom":sQuery(id+"F4.wireOp",EDGE,"E7.18.1.0")}),1.0]])]});
            var Q336;
            Q336=makeQuery(id+"F4.imprint","IMPRINT",FACE,{"disambiguationData":[TD([[makeQuery(id+"F4.imprint","IMPRINT",EDGE,{"derivedFrom":sQuery(id+"F4.wireOp",EDGE,"E7.16.19.0")}),1.0]])]});
            var Q337;
            Q337=makeQuery(id+"F4.imprint","IMPRINT",FACE,{"disambiguationData":[TD([[makeQuery(id+"F4.imprint","IMPRINT",EDGE,{"derivedFrom":sQuery(id+"F4.wireOp",EDGE,"E7.20.15.0")}),1.0]])]});
            var Q338;
            Q338=makeQuery(id+"F4.imprint","IMPRINT",FACE,{"disambiguationData":[TD([[makeQuery(id+"F4.imprint","IMPRINT",EDGE,{"derivedFrom":sQuery(id+"F4.wireOp",EDGE,"E7.19.8.0")}),1.0]])]});
            var Q339;
            Q339=makeQuery(id+"F4.imprint","IMPRINT",FACE,{"disambiguationData":[TD([[makeQuery(id+"F4.imprint","IMPRINT",EDGE,{"derivedFrom":sQuery(id+"F4.wireOp",EDGE,"E7.18.17.0")}),1.0]])]});
            var Q340;
            Q340=makeQuery(id+"F4.imprint","IMPRINT",FACE,{"disambiguationData":[TD([[makeQuery(id+"F4.imprint","IMPRINT",EDGE,{"derivedFrom":sQuery(id+"F4.wireOp",EDGE,"E7.23.4.0")}),1.0]])]});
            var Q341;
            Q341=makeQuery(id+"F4.imprint","IMPRINT",FACE,{"disambiguationData":[TD([[makeQuery(id+"F4.imprint","IMPRINT",EDGE,{"derivedFrom":sQuery(id+"F4.wireOp",EDGE,"E7.22.13.0")}),1.0]])]});
            var Q342;
            Q342=makeQuery(id+"F4.imprint","IMPRINT",FACE,{"disambiguationData":[TD([[makeQuery(id+"F4.imprint","IMPRINT",EDGE,{"derivedFrom":sQuery(id+"F4.wireOp",EDGE,"E7.21.22.0")}),1.0]])]});
            var Q343;
            Q343=makeQuery(id+"F4.imprint","IMPRINT",FACE,{"disambiguationData":[TD([[makeQuery(id+"F4.imprint","IMPRINT",EDGE,{"derivedFrom":sQuery(id+"F4.wireOp",EDGE,"E7.21.6.0")}),1.0]])]});
            var Q344;
            Q344=makeQuery(id+"F4.imprint","IMPRINT",FACE,{"disambiguationData":[TD([[makeQuery(id+"F4.imprint","IMPRINT",EDGE,{"derivedFrom":sQuery(id+"F4.wireOp",EDGE,"E7.1.11.0")}),1.0]])]});
            var Q345;
            Q345=makeQuery(id+"F4.imprint","IMPRINT",FACE,{"disambiguationData":[TD([[makeQuery(id+"F4.imprint","IMPRINT",EDGE,{"derivedFrom":sQuery(id+"F4.wireOp",EDGE,"E7.4.0.0")}),1.0]])]});
            var Q346;
            Q346=makeQuery(id+"F4.imprint","IMPRINT",FACE,{"disambiguationData":[TD([[makeQuery(id+"F4.imprint","IMPRINT",EDGE,{"derivedFrom":sQuery(id+"F4.wireOp",EDGE,"E7.3.9.0")}),1.0]])]});
            var Q347;
            Q347=makeQuery(id+"F4.imprint","IMPRINT",FACE,{"disambiguationData":[TD([[makeQuery(id+"F4.imprint","IMPRINT",EDGE,{"derivedFrom":sQuery(id+"F4.wireOp",EDGE,"E7.2.2.0")}),1.0]])]});
            var Q348;
            Q348=makeQuery(id+"F4.imprint","IMPRINT",FACE,{"disambiguationData":[TD([[makeQuery(id+"F4.imprint","IMPRINT",EDGE,{"derivedFrom":sQuery(id+"F4.wireOp",EDGE,"E7.5.23.0")}),1.0]])]});
            var Q349;
            Q349=makeQuery(id+"F4.imprint","IMPRINT",FACE,{"disambiguationData":[TD([[makeQuery(id+"F4.imprint","IMPRINT",EDGE,{"derivedFrom":sQuery(id+"F4.wireOp",EDGE,"E7.5.7.0")}),1.0]])]});
            var Q350;
            Q350=makeQuery(id+"F4.imprint","IMPRINT",FACE,{"disambiguationData":[TD([[makeQuery(id+"F4.imprint","IMPRINT",EDGE,{"derivedFrom":sQuery(id+"F4.wireOp",EDGE,"E7.9.3.0")}),1.0]])]});
            var Q351;
            Q351=makeQuery(id+"F4.imprint","IMPRINT",FACE,{"disambiguationData":[TD([[makeQuery(id+"F4.imprint","IMPRINT",EDGE,{"derivedFrom":sQuery(id+"F4.wireOp",EDGE,"E7.8.12.0")}),1.0]])]});
            var Q352;
            Q352=makeQuery(id+"F4.imprint","IMPRINT",FACE,{"disambiguationData":[TD([[makeQuery(id+"F4.imprint","IMPRINT",EDGE,{"derivedFrom":sQuery(id+"F4.wireOp",EDGE,"E7.7.21.0")}),1.0]])]});
            var Q353;
            Q353=makeQuery(id+"F4.imprint","IMPRINT",FACE,{"disambiguationData":[TD([[makeQuery(id+"F4.imprint","IMPRINT",EDGE,{"derivedFrom":sQuery(id+"F4.wireOp",EDGE,"E7.7.5.0")}),1.0]])]});
            var Q354;
            Q354=makeQuery(id+"F4.imprint","IMPRINT",FACE,{"disambiguationData":[TD([[makeQuery(id+"F4.imprint","IMPRINT",EDGE,{"derivedFrom":sQuery(id+"F4.wireOp",EDGE,"E7.11.17.0")}),1.0]])]});
            var Q355;
            Q355=makeQuery(id+"F4.imprint","IMPRINT",FACE,{"disambiguationData":[TD([[makeQuery(id+"F4.imprint","IMPRINT",EDGE,{"derivedFrom":sQuery(id+"F4.wireOp",EDGE,"E7.10.10.0")}),1.0]])]});
            var Q356;
            Q356=makeQuery(id+"F4.imprint","IMPRINT",FACE,{"disambiguationData":[TD([[makeQuery(id+"F4.imprint","IMPRINT",EDGE,{"derivedFrom":sQuery(id+"F4.wireOp",EDGE,"E7.9.19.0")}),1.0]])]});
            var Q357;
            Q357=makeQuery(id+"F4.imprint","IMPRINT",FACE,{"disambiguationData":[TD([[makeQuery(id+"F4.imprint","IMPRINT",EDGE,{"derivedFrom":sQuery(id+"F4.wireOp",EDGE,"E7.14.6.0")}),1.0]])]});
            var Q358;
            Q358=makeQuery(id+"F4.imprint","IMPRINT",FACE,{"disambiguationData":[TD([[makeQuery(id+"F4.imprint","IMPRINT",EDGE,{"derivedFrom":sQuery(id+"F4.wireOp",EDGE,"E7.13.15.0")}),1.0]])]});
            var Q359;
            Q359=makeQuery(id+"F4.imprint","IMPRINT",FACE,{"disambiguationData":[TD([[makeQuery(id+"F4.imprint","IMPRINT",EDGE,{"derivedFrom":sQuery(id+"F4.wireOp",EDGE,"E7.12.24.0")}),1.0]])]});
            var Q360;
            Q360=makeQuery(id+"F4.imprint","IMPRINT",FACE,{"disambiguationData":[TD([[makeQuery(id+"F4.imprint","IMPRINT",EDGE,{"derivedFrom":sQuery(id+"F4.wireOp",EDGE,"E7.12.8.0")}),1.0]])]});
            var Q361;
            Q361=makeQuery(id+"F4.imprint","IMPRINT",FACE,{"disambiguationData":[TD([[makeQuery(id+"F4.imprint","IMPRINT",EDGE,{"derivedFrom":sQuery(id+"F4.wireOp",EDGE,"E7.16.4.0")}),1.0]])]});
            var Q362;
            Q362=makeQuery(id+"F4.imprint","IMPRINT",FACE,{"disambiguationData":[TD([[makeQuery(id+"F4.imprint","IMPRINT",EDGE,{"derivedFrom":sQuery(id+"F4.wireOp",EDGE,"E7.15.13.0")}),1.0]])]});
            var Q363;
            Q363=makeQuery(id+"F4.imprint","IMPRINT",FACE,{"disambiguationData":[TD([[makeQuery(id+"F4.imprint","IMPRINT",EDGE,{"derivedFrom":sQuery(id+"F4.wireOp",EDGE,"E7.14.22.0")}),1.0]])]});
            var Q364;
            Q364=makeQuery(id+"F4.imprint","IMPRINT",FACE,{"disambiguationData":[TD([[makeQuery(id+"F4.imprint","IMPRINT",EDGE,{"derivedFrom":sQuery(id+"F4.wireOp",EDGE,"E7.18.2.0")}),1.0]])]});
            var Q365;
            Q365=makeQuery(id+"F4.imprint","IMPRINT",FACE,{"disambiguationData":[TD([[makeQuery(id+"F4.imprint","IMPRINT",EDGE,{"derivedFrom":sQuery(id+"F4.wireOp",EDGE,"E7.17.11.0")}),1.0]])]});
            var Q366;
            Q366=makeQuery(id+"F4.imprint","IMPRINT",FACE,{"disambiguationData":[TD([[makeQuery(id+"F4.imprint","IMPRINT",EDGE,{"derivedFrom":sQuery(id+"F4.wireOp",EDGE,"E7.16.20.0")}),1.0]])]});
            var Q367;
            Q367=makeQuery(id+"F4.imprint","IMPRINT",FACE,{"disambiguationData":[TD([[makeQuery(id+"F4.imprint","IMPRINT",EDGE,{"derivedFrom":sQuery(id+"F4.wireOp",EDGE,"E7.20.16.0")}),1.0]])]});
            var Q368;
            Q368=makeQuery(id+"F4.imprint","IMPRINT",FACE,{"disambiguationData":[TD([[makeQuery(id+"F4.imprint","IMPRINT",EDGE,{"derivedFrom":sQuery(id+"F4.wireOp",EDGE,"E7.20.0.0")}),1.0]])]});
            var Q369;
            Q369=makeQuery(id+"F4.imprint","IMPRINT",FACE,{"disambiguationData":[TD([[makeQuery(id+"F4.imprint","IMPRINT",EDGE,{"derivedFrom":sQuery(id+"F4.wireOp",EDGE,"E7.19.9.0")}),1.0]])]});
            var Q370;
            Q370=makeQuery(id+"F4.imprint","IMPRINT",FACE,{"disambiguationData":[TD([[makeQuery(id+"F4.imprint","IMPRINT",EDGE,{"derivedFrom":sQuery(id+"F4.wireOp",EDGE,"E7.18.18.0")}),1.0]])]});
            var Q371;
            Q371=makeQuery(id+"F4.imprint","IMPRINT",FACE,{"disambiguationData":[TD([[makeQuery(id+"F4.imprint","IMPRINT",EDGE,{"derivedFrom":sQuery(id+"F4.wireOp",EDGE,"E7.23.5.0")}),1.0]])]});
            var Q372;
            Q372=makeQuery(id+"F4.imprint","IMPRINT",FACE,{"disambiguationData":[TD([[makeQuery(id+"F4.imprint","IMPRINT",EDGE,{"derivedFrom":sQuery(id+"F4.wireOp",EDGE,"E7.22.14.0")}),1.0]])]});
            var Q373;
            Q373=makeQuery(id+"F4.imprint","IMPRINT",FACE,{"disambiguationData":[TD([[makeQuery(id+"F4.imprint","IMPRINT",EDGE,{"derivedFrom":sQuery(id+"F4.wireOp",EDGE,"E7.21.23.0")}),1.0]])]});
            var Q374;
            Q374=makeQuery(id+"F4.imprint","IMPRINT",FACE,{"disambiguationData":[TD([[makeQuery(id+"F4.imprint","IMPRINT",EDGE,{"derivedFrom":sQuery(id+"F4.wireOp",EDGE,"E7.21.7.0")}),1.0]])]});
            var Q375;
            Q375=makeQuery(id+"F4.imprint","IMPRINT",FACE,{"disambiguationData":[TD([[makeQuery(id+"F4.imprint","IMPRINT",EDGE,{"derivedFrom":sQuery(id+"F4.wireOp",EDGE,"E7.23.21.0")}),1.0]])]});
            var Q376;
            Q376=makeQuery(id+"F4.imprint","IMPRINT",FACE,{"disambiguationData":[TD([[makeQuery(id+"F4.imprint","IMPRINT",EDGE,{"derivedFrom":sQuery(id+"F4.wireOp",EDGE,"E7.1.12.0")}),1.0]])]});
            var Q377;
            Q377=makeQuery(id+"F4.imprint","IMPRINT",FACE,{"disambiguationData":[TD([[makeQuery(id+"F4.imprint","IMPRINT",EDGE,{"derivedFrom":sQuery(id+"F4.wireOp",EDGE,"E7.0.21.0")}),1.0]])]});
            var Q378;
            Q378=makeQuery(id+"F4.imprint","IMPRINT",FACE,{"disambiguationData":[TD([[makeQuery(id+"F4.imprint","IMPRINT",EDGE,{"derivedFrom":sQuery(id+"F4.wireOp",EDGE,"E7.3.10.0")}),1.0]])]});
            var Q379;
            Q379=makeQuery(id+"F4.imprint","IMPRINT",FACE,{"disambiguationData":[TD([[makeQuery(id+"F4.imprint","IMPRINT",EDGE,{"derivedFrom":sQuery(id+"F4.wireOp",EDGE,"E7.2.19.0")}),1.0]])]});
            var Q380;
            Q380=makeQuery(id+"F4.imprint","IMPRINT",FACE,{"disambiguationData":[TD([[makeQuery(id+"F4.imprint","IMPRINT",EDGE,{"derivedFrom":sQuery(id+"F4.wireOp",EDGE,"E7.6.15.0")}),1.0]])]});
            var Q381;
            Q381=makeQuery(id+"F4.imprint","IMPRINT",FACE,{"disambiguationData":[TD([[makeQuery(id+"F4.imprint","IMPRINT",EDGE,{"derivedFrom":sQuery(id+"F4.wireOp",EDGE,"E7.5.24.0")}),1.0]])]});
            var Q382;
            Q382=makeQuery(id+"F4.imprint","IMPRINT",FACE,{"disambiguationData":[TD([[makeQuery(id+"F4.imprint","IMPRINT",EDGE,{"derivedFrom":sQuery(id+"F4.wireOp",EDGE,"E7.5.8.0")}),1.0]])]});
            var Q383;
            Q383=makeQuery(id+"F4.imprint","IMPRINT",FACE,{"disambiguationData":[TD([[makeQuery(id+"F4.imprint","IMPRINT",EDGE,{"derivedFrom":sQuery(id+"F4.wireOp",EDGE,"E7.4.17.0")}),1.0]])]});
            var Q384;
            Q384=makeQuery(id+"F4.imprint","IMPRINT",FACE,{"disambiguationData":[TD([[makeQuery(id+"F4.imprint","IMPRINT",EDGE,{"derivedFrom":sQuery(id+"F4.wireOp",EDGE,"E7.9.4.0")}),1.0]])]});
            var Q385;
            Q385=makeQuery(id+"F4.imprint","IMPRINT",FACE,{"disambiguationData":[TD([[makeQuery(id+"F4.imprint","IMPRINT",EDGE,{"derivedFrom":sQuery(id+"F4.wireOp",EDGE,"E7.8.13.0")}),1.0]])]});
            var Q386;
            Q386=makeQuery(id+"F4.imprint","IMPRINT",FACE,{"disambiguationData":[TD([[makeQuery(id+"F4.imprint","IMPRINT",EDGE,{"derivedFrom":sQuery(id+"F4.wireOp",EDGE,"E7.7.22.0")}),1.0]])]});
            var Q387;
            Q387=makeQuery(id+"F4.imprint","IMPRINT",FACE,{"disambiguationData":[TD([[makeQuery(id+"F4.imprint","IMPRINT",EDGE,{"derivedFrom":sQuery(id+"F4.wireOp",EDGE,"E7.7.6.0")}),1.0]])]});
            var Q388;
            Q388=makeQuery(id+"F4.imprint","IMPRINT",FACE,{"disambiguationData":[TD([[makeQuery(id+"F4.imprint","IMPRINT",EDGE,{"derivedFrom":sQuery(id+"F4.wireOp",EDGE,"E7.11.2.0")}),1.0]])]});
            var Q389;
            Q389=makeQuery(id+"F4.imprint","IMPRINT",FACE,{"disambiguationData":[TD([[makeQuery(id+"F4.imprint","IMPRINT",EDGE,{"derivedFrom":sQuery(id+"F4.wireOp",EDGE,"E7.10.11.0")}),1.0]])]});
            var Q390;
            Q390=makeQuery(id+"F4.imprint","IMPRINT",FACE,{"disambiguationData":[TD([[makeQuery(id+"F4.imprint","IMPRINT",EDGE,{"derivedFrom":sQuery(id+"F4.wireOp",EDGE,"E7.9.20.0")}),1.0]])]});
            var Q391;
            Q391=makeQuery(id+"F4.imprint","IMPRINT",FACE,{"disambiguationData":[TD([[makeQuery(id+"F4.imprint","IMPRINT",EDGE,{"derivedFrom":sQuery(id+"F4.wireOp",EDGE,"E7.14.7.0")}),1.0]])]});
            var Q392;
            Q392=makeQuery(id+"F4.imprint","IMPRINT",FACE,{"disambiguationData":[TD([[makeQuery(id+"F4.imprint","IMPRINT",EDGE,{"derivedFrom":sQuery(id+"F4.wireOp",EDGE,"E7.13.0.0")}),1.0]])]});
            var Q393;
            Q393=makeQuery(id+"F4.imprint","IMPRINT",FACE,{"disambiguationData":[TD([[makeQuery(id+"F4.imprint","IMPRINT",EDGE,{"derivedFrom":sQuery(id+"F4.wireOp",EDGE,"E7.12.9.0")}),1.0]])]});
            var Q394;
            Q394=makeQuery(id+"F4.imprint","IMPRINT",FACE,{"disambiguationData":[TD([[makeQuery(id+"F4.imprint","IMPRINT",EDGE,{"derivedFrom":sQuery(id+"F4.wireOp",EDGE,"E7.16.5.0")}),1.0]])]});
            var Q395;
            Q395=makeQuery(id+"F4.imprint","IMPRINT",FACE,{"disambiguationData":[TD([[makeQuery(id+"F4.imprint","IMPRINT",EDGE,{"derivedFrom":sQuery(id+"F4.wireOp",EDGE,"E7.14.23.0")}),1.0]])]});
            var Q396;
            Q396=makeQuery(id+"F4.imprint","IMPRINT",FACE,{"disambiguationData":[TD([[makeQuery(id+"F4.imprint","IMPRINT",EDGE,{"derivedFrom":sQuery(id+"F4.wireOp",EDGE,"E7.18.3.0")}),1.0]])]});
            var Q397;
            Q397=makeQuery(id+"F4.imprint","IMPRINT",FACE,{"disambiguationData":[TD([[makeQuery(id+"F4.imprint","IMPRINT",EDGE,{"derivedFrom":sQuery(id+"F4.wireOp",EDGE,"E7.16.21.0")}),1.0]])]});
            var Q398;
            Q398=makeQuery(id+"F4.imprint","IMPRINT",FACE,{"disambiguationData":[TD([[makeQuery(id+"F4.imprint","IMPRINT",EDGE,{"derivedFrom":sQuery(id+"F4.wireOp",EDGE,"E7.20.17.0")}),1.0]])]});
            var Q399;
            Q399=makeQuery(id+"F4.imprint","IMPRINT",FACE,{"disambiguationData":[TD([[makeQuery(id+"F4.imprint","IMPRINT",EDGE,{"derivedFrom":sQuery(id+"F4.wireOp",EDGE,"E7.20.1.0")}),1.0]])]});
            var Q400;
            Q400=makeQuery(id+"F4.imprint","IMPRINT",FACE,{"disambiguationData":[TD([[makeQuery(id+"F4.imprint","IMPRINT",EDGE,{"derivedFrom":sQuery(id+"F4.wireOp",EDGE,"E7.19.10.0")}),1.0]])]});
            var Q401;
            Q401=makeQuery(id+"F4.imprint","IMPRINT",FACE,{"disambiguationData":[TD([[makeQuery(id+"F4.imprint","IMPRINT",EDGE,{"derivedFrom":sQuery(id+"F4.wireOp",EDGE,"E7.18.19.0")}),1.0]])]});
            var Q402;
            Q402=makeQuery(id+"F4.imprint","IMPRINT",FACE,{"disambiguationData":[TD([[makeQuery(id+"F4.imprint","IMPRINT",EDGE,{"derivedFrom":sQuery(id+"F4.wireOp",EDGE,"E7.23.6.0")}),1.0]])]});
            var Q403;
            Q403=makeQuery(id+"F4.imprint","IMPRINT",FACE,{"disambiguationData":[TD([[makeQuery(id+"F4.imprint","IMPRINT",EDGE,{"derivedFrom":sQuery(id+"F4.wireOp",EDGE,"E7.22.15.0")}),1.0]])]});
            var Q404;
            Q404=makeQuery(id+"F4.imprint","IMPRINT",FACE,{"disambiguationData":[TD([[makeQuery(id+"F4.imprint","IMPRINT",EDGE,{"derivedFrom":sQuery(id+"F4.wireOp",EDGE,"E7.21.24.0")}),1.0]])]});
            var Q405;
            Q405=makeQuery(id+"F4.imprint","IMPRINT",FACE,{"disambiguationData":[TD([[makeQuery(id+"F4.imprint","IMPRINT",EDGE,{"derivedFrom":sQuery(id+"F4.wireOp",EDGE,"E7.21.8.0")}),1.0]])]});
            var Q406;
            Q406=makeQuery(id+"F4.imprint","IMPRINT",FACE,{"disambiguationData":[TD([[makeQuery(id+"F4.imprint","IMPRINT",EDGE,{"derivedFrom":sQuery(id+"F4.wireOp",EDGE,"E7.24.13.0")}),1.0]])]});
            var Q407;
            Q407=makeQuery(id+"F4.imprint","IMPRINT",FACE,{"disambiguationData":[TD([[makeQuery(id+"F4.imprint","IMPRINT",EDGE,{"derivedFrom":sQuery(id+"F4.wireOp",EDGE,"E7.23.22.0")}),1.0]])]});
            var Q408;
            Q408=makeQuery(id+"F4.imprint","IMPRINT",FACE,{"disambiguationData":[TD([[makeQuery(id+"F4.imprint","IMPRINT",EDGE,{"derivedFrom":sQuery(id+"F4.wireOp",EDGE,"E7.2.4.0")}),1.0]])]});
            var Q409;
            Q409=makeQuery(id+"F4.imprint","IMPRINT",FACE,{"disambiguationData":[TD([[makeQuery(id+"F4.imprint","IMPRINT",EDGE,{"derivedFrom":sQuery(id+"F4.wireOp",EDGE,"E7.1.13.0")}),1.0]])]});
            var Q410;
            Q410=makeQuery(id+"F4.imprint","IMPRINT",FACE,{"disambiguationData":[TD([[makeQuery(id+"F4.imprint","IMPRINT",EDGE,{"derivedFrom":sQuery(id+"F4.wireOp",EDGE,"E7.5.9.0")}),1.0]])]});
            var Q411;
            Q411=makeQuery(id+"F4.imprint","IMPRINT",FACE,{"disambiguationData":[TD([[makeQuery(id+"F4.imprint","IMPRINT",EDGE,{"derivedFrom":sQuery(id+"F4.wireOp",EDGE,"E7.4.2.0")}),1.0]])]});
            var Q412;
            Q412=makeQuery(id+"F4.imprint","IMPRINT",FACE,{"disambiguationData":[TD([[makeQuery(id+"F4.imprint","IMPRINT",EDGE,{"derivedFrom":sQuery(id+"F4.wireOp",EDGE,"E7.3.11.0")}),1.0]])]});
            var Q413;
            Q413=makeQuery(id+"F4.imprint","IMPRINT",FACE,{"disambiguationData":[TD([[makeQuery(id+"F4.imprint","IMPRINT",EDGE,{"derivedFrom":sQuery(id+"F4.wireOp",EDGE,"E7.7.23.0")}),1.0]])]});
            var Q414;
            Q414=makeQuery(id+"F4.imprint","IMPRINT",FACE,{"disambiguationData":[TD([[makeQuery(id+"F4.imprint","IMPRINT",EDGE,{"derivedFrom":sQuery(id+"F4.wireOp",EDGE,"E7.7.7.0")}),1.0]])]});
            var Q415;
            Q415=makeQuery(id+"F4.imprint","IMPRINT",FACE,{"disambiguationData":[TD([[makeQuery(id+"F4.imprint","IMPRINT",EDGE,{"derivedFrom":sQuery(id+"F4.wireOp",EDGE,"E7.6.0.0")}),1.0]])]});
            var Q416;
            Q416=makeQuery(id+"F4.imprint","IMPRINT",FACE,{"disambiguationData":[TD([[makeQuery(id+"F4.imprint","IMPRINT",EDGE,{"derivedFrom":sQuery(id+"F4.wireOp",EDGE,"E7.10.12.0")}),1.0]])]});
            var Q417;
            Q417=makeQuery(id+"F4.imprint","IMPRINT",FACE,{"disambiguationData":[TD([[makeQuery(id+"F4.imprint","IMPRINT",EDGE,{"derivedFrom":sQuery(id+"F4.wireOp",EDGE,"E7.9.21.0")}),1.0]])]});
            var Q418;
            Q418=makeQuery(id+"F4.imprint","IMPRINT",FACE,{"disambiguationData":[TD([[makeQuery(id+"F4.imprint","IMPRINT",EDGE,{"derivedFrom":sQuery(id+"F4.wireOp",EDGE,"E7.9.5.0")}),1.0]])]});
            var Q419;
            Q419=makeQuery(id+"F4.imprint","IMPRINT",FACE,{"disambiguationData":[TD([[makeQuery(id+"F4.imprint","IMPRINT",EDGE,{"derivedFrom":sQuery(id+"F4.wireOp",EDGE,"E7.12.10.0")}),1.0]])]});
            var Q420;
            Q420=makeQuery(id+"F4.imprint","IMPRINT",FACE,{"disambiguationData":[TD([[makeQuery(id+"F4.imprint","IMPRINT",EDGE,{"derivedFrom":sQuery(id+"F4.wireOp",EDGE,"E7.11.19.0")}),1.0]])]});
            var Q421;
            Q421=makeQuery(id+"F4.imprint","IMPRINT",FACE,{"disambiguationData":[TD([[makeQuery(id+"F4.imprint","IMPRINT",EDGE,{"derivedFrom":sQuery(id+"F4.wireOp",EDGE,"E7.15.15.0")}),1.0]])]});
            var Q422;
            Q422=makeQuery(id+"F4.imprint","IMPRINT",FACE,{"disambiguationData":[TD([[makeQuery(id+"F4.imprint","IMPRINT",EDGE,{"derivedFrom":sQuery(id+"F4.wireOp",EDGE,"E7.14.24.0")}),1.0]])]});
            var Q423;
            Q423=makeQuery(id+"F4.imprint","IMPRINT",FACE,{"disambiguationData":[TD([[makeQuery(id+"F4.imprint","IMPRINT",EDGE,{"derivedFrom":sQuery(id+"F4.wireOp",EDGE,"E7.14.8.0")}),1.0]])]});
            var Q424;
            Q424=makeQuery(id+"F4.imprint","IMPRINT",FACE,{"disambiguationData":[TD([[makeQuery(id+"F4.imprint","IMPRINT",EDGE,{"derivedFrom":sQuery(id+"F4.wireOp",EDGE,"E7.13.17.0")}),1.0]])]});
            var Q425;
            Q425=makeQuery(id+"F4.imprint","IMPRINT",FACE,{"disambiguationData":[TD([[makeQuery(id+"F4.imprint","IMPRINT",EDGE,{"derivedFrom":sQuery(id+"F4.wireOp",EDGE,"E7.16.6.0")}),1.0]])]});
            var Q426;
            Q426=makeQuery(id+"F4.imprint","IMPRINT",FACE,{"disambiguationData":[TD([[makeQuery(id+"F4.imprint","IMPRINT",EDGE,{"derivedFrom":sQuery(id+"F4.wireOp",EDGE,"E7.16.22.0")}),1.0]])]});
            var Q427;
            Q427=makeQuery(id+"F4.imprint","IMPRINT",FACE,{"disambiguationData":[TD([[makeQuery(id+"F4.imprint","IMPRINT",EDGE,{"derivedFrom":sQuery(id+"F4.wireOp",EDGE,"E7.19.11.0")}),1.0]])]});
            var Q428;
            Q428=makeQuery(id+"F4.imprint","IMPRINT",FACE,{"disambiguationData":[TD([[makeQuery(id+"F4.imprint","IMPRINT",EDGE,{"derivedFrom":sQuery(id+"F4.wireOp",EDGE,"E7.18.20.0")}),1.0]])]});
            var Q429;
            Q429=makeQuery(id+"F4.imprint","IMPRINT",FACE,{"disambiguationData":[TD([[makeQuery(id+"F4.imprint","IMPRINT",EDGE,{"derivedFrom":sQuery(id+"F4.wireOp",EDGE,"E7.18.4.0")}),1.0]])]});
            var Q430;
            Q430=makeQuery(id+"F4.imprint","IMPRINT",FACE,{"disambiguationData":[TD([[makeQuery(id+"F4.imprint","IMPRINT",EDGE,{"derivedFrom":sQuery(id+"F4.wireOp",EDGE,"E7.17.13.0")}),1.0]])]});
            var Q431;
            Q431=makeQuery(id+"F4.imprint","IMPRINT",FACE,{"disambiguationData":[TD([[makeQuery(id+"F4.imprint","IMPRINT",EDGE,{"derivedFrom":sQuery(id+"F4.wireOp",EDGE,"E7.22.0.0")}),1.0]])]});
            var Q432;
            Q432=makeQuery(id+"F4.imprint","IMPRINT",FACE,{"disambiguationData":[TD([[makeQuery(id+"F4.imprint","IMPRINT",EDGE,{"derivedFrom":sQuery(id+"F4.wireOp",EDGE,"E7.21.9.0")}),1.0]])]});
            var Q433;
            Q433=makeQuery(id+"F4.imprint","IMPRINT",FACE,{"disambiguationData":[TD([[makeQuery(id+"F4.imprint","IMPRINT",EDGE,{"derivedFrom":sQuery(id+"F4.wireOp",EDGE,"E7.20.18.0")}),1.0]])]});
            var Q434;
            Q434=makeQuery(id+"F4.imprint","IMPRINT",FACE,{"disambiguationData":[TD([[makeQuery(id+"F4.imprint","IMPRINT",EDGE,{"derivedFrom":sQuery(id+"F4.wireOp",EDGE,"E7.20.2.0")}),1.0]])]});
            var Q435;
            Q435=makeQuery(id+"F4.imprint","IMPRINT",FACE,{"disambiguationData":[TD([[makeQuery(id+"F4.imprint","IMPRINT",EDGE,{"derivedFrom":sQuery(id+"F4.wireOp",EDGE,"E7.23.23.0")}),1.0]])]});
            var Q436;
            Q436=makeQuery(id+"F4.imprint","IMPRINT",FACE,{"disambiguationData":[TD([[makeQuery(id+"F4.imprint","IMPRINT",EDGE,{"derivedFrom":sQuery(id+"F4.wireOp",EDGE,"E7.23.7.0")}),1.0]])]});
            var Q437;
            Q437=makeQuery(id+"F4.imprint","IMPRINT",FACE,{"disambiguationData":[TD([[makeQuery(id+"F4.imprint","IMPRINT",EDGE,{"derivedFrom":sQuery(id+"F4.wireOp",EDGE,"E7.2.21.0")}),1.0]])]});
            var Q438;
            Q438=makeQuery(id+"F4.imprint","IMPRINT",FACE,{"disambiguationData":[TD([[makeQuery(id+"F4.imprint","IMPRINT",EDGE,{"derivedFrom":sQuery(id+"F4.wireOp",EDGE,"E7.1.14.0")}),1.0]])]});
            var Q439;
            Q439=makeQuery(id+"F4.imprint","IMPRINT",FACE,{"disambiguationData":[TD([[makeQuery(id+"F4.imprint","IMPRINT",EDGE,{"derivedFrom":sQuery(id+"F4.wireOp",EDGE,"E7.0.23.0")}),1.0]])]});
            var Q440;
            Q440=makeQuery(id+"F4.imprint","IMPRINT",FACE,{"disambiguationData":[TD([[makeQuery(id+"F4.imprint","IMPRINT",EDGE,{"derivedFrom":sQuery(id+"F4.wireOp",EDGE,"E7.5.10.0")}),1.0]])]});
            var Q441;
            Q441=makeQuery(id+"F4.imprint","IMPRINT",FACE,{"disambiguationData":[TD([[makeQuery(id+"F4.imprint","IMPRINT",EDGE,{"derivedFrom":sQuery(id+"F4.wireOp",EDGE,"E7.4.19.0")}),1.0]])]});
            var Q442;
            Q442=makeQuery(id+"F4.imprint","IMPRINT",FACE,{"disambiguationData":[TD([[makeQuery(id+"F4.imprint","IMPRINT",EDGE,{"derivedFrom":sQuery(id+"F4.wireOp",EDGE,"E7.3.12.0")}),1.0]])]});
            var Q443;
            Q443=makeQuery(id+"F4.imprint","IMPRINT",FACE,{"disambiguationData":[TD([[makeQuery(id+"F4.imprint","IMPRINT",EDGE,{"derivedFrom":sQuery(id+"F4.wireOp",EDGE,"E7.7.24.0")}),1.0]])]});
            var Q444;
            Q444=makeQuery(id+"F4.imprint","IMPRINT",FACE,{"disambiguationData":[TD([[makeQuery(id+"F4.imprint","IMPRINT",EDGE,{"derivedFrom":sQuery(id+"F4.wireOp",EDGE,"E7.7.8.0")}),1.0]])]});
            var Q445;
            Q445=makeQuery(id+"F4.imprint","IMPRINT",FACE,{"disambiguationData":[TD([[makeQuery(id+"F4.imprint","IMPRINT",EDGE,{"derivedFrom":sQuery(id+"F4.wireOp",EDGE,"E7.6.17.0")}),1.0]])]});
            var Q446;
            Q446=makeQuery(id+"F4.imprint","IMPRINT",FACE,{"disambiguationData":[TD([[makeQuery(id+"F4.imprint","IMPRINT",EDGE,{"derivedFrom":sQuery(id+"F4.wireOp",EDGE,"E7.10.13.0")}),1.0]])]});
            var Q447;
            Q447=makeQuery(id+"F4.imprint","IMPRINT",FACE,{"disambiguationData":[TD([[makeQuery(id+"F4.imprint","IMPRINT",EDGE,{"derivedFrom":sQuery(id+"F4.wireOp",EDGE,"E7.9.22.0")}),1.0]])]});
            var Q448;
            Q448=makeQuery(id+"F4.imprint","IMPRINT",FACE,{"disambiguationData":[TD([[makeQuery(id+"F4.imprint","IMPRINT",EDGE,{"derivedFrom":sQuery(id+"F4.wireOp",EDGE,"E7.9.6.0")}),1.0]])]});
            var Q449;
            Q449=makeQuery(id+"F4.imprint","IMPRINT",FACE,{"disambiguationData":[TD([[makeQuery(id+"F4.imprint","IMPRINT",EDGE,{"derivedFrom":sQuery(id+"F4.wireOp",EDGE,"E7.8.15.0")}),1.0]])]});
            var Q450;
            Q450=makeQuery(id+"F4.imprint","IMPRINT",FACE,{"disambiguationData":[TD([[makeQuery(id+"F4.imprint","IMPRINT",EDGE,{"derivedFrom":sQuery(id+"F4.wireOp",EDGE,"E7.13.2.0")}),1.0]])]});
            var Q451;
            Q451=makeQuery(id+"F4.imprint","IMPRINT",FACE,{"disambiguationData":[TD([[makeQuery(id+"F4.imprint","IMPRINT",EDGE,{"derivedFrom":sQuery(id+"F4.wireOp",EDGE,"E7.12.11.0")}),1.0]])]});
            var Q452;
            Q452=makeQuery(id+"F4.imprint","IMPRINT",FACE,{"disambiguationData":[TD([[makeQuery(id+"F4.imprint","IMPRINT",EDGE,{"derivedFrom":sQuery(id+"F4.wireOp",EDGE,"E7.11.4.0")}),1.0]])]});
            var Q453;
            Q453=makeQuery(id+"F4.imprint","IMPRINT",FACE,{"disambiguationData":[TD([[makeQuery(id+"F4.imprint","IMPRINT",EDGE,{"derivedFrom":sQuery(id+"F4.wireOp",EDGE,"E7.15.0.0")}),1.0]])]});
            var Q454;
            Q454=makeQuery(id+"F4.imprint","IMPRINT",FACE,{"disambiguationData":[TD([[makeQuery(id+"F4.imprint","IMPRINT",EDGE,{"derivedFrom":sQuery(id+"F4.wireOp",EDGE,"E7.14.9.0")}),1.0]])]});
            var Q455;
            Q455=makeQuery(id+"F4.imprint","IMPRINT",FACE,{"disambiguationData":[TD([[makeQuery(id+"F4.imprint","IMPRINT",EDGE,{"derivedFrom":sQuery(id+"F4.wireOp",EDGE,"E7.16.7.0")}),1.0]])]});
            var Q456;
            Q456=makeQuery(id+"F4.imprint","IMPRINT",FACE,{"disambiguationData":[TD([[makeQuery(id+"F4.imprint","IMPRINT",EDGE,{"derivedFrom":sQuery(id+"F4.wireOp",EDGE,"E7.16.23.0")}),1.0]])]});
            var Q457;
            Q457=makeQuery(id+"F4.imprint","IMPRINT",FACE,{"disambiguationData":[TD([[makeQuery(id+"F4.imprint","IMPRINT",EDGE,{"derivedFrom":sQuery(id+"F4.wireOp",EDGE,"E7.18.21.0")}),1.0]])]});
            var Q458;
            Q458=makeQuery(id+"F4.imprint","IMPRINT",FACE,{"disambiguationData":[TD([[makeQuery(id+"F4.imprint","IMPRINT",EDGE,{"derivedFrom":sQuery(id+"F4.wireOp",EDGE,"E7.18.5.0")}),1.0]])]});
            var Q459;
            Q459=makeQuery(id+"F4.imprint","IMPRINT",FACE,{"disambiguationData":[TD([[makeQuery(id+"F4.imprint","IMPRINT",EDGE,{"derivedFrom":sQuery(id+"F4.wireOp",EDGE,"E7.22.1.0")}),1.0]])]});
            var Q460;
            Q460=makeQuery(id+"F4.imprint","IMPRINT",FACE,{"disambiguationData":[TD([[makeQuery(id+"F4.imprint","IMPRINT",EDGE,{"derivedFrom":sQuery(id+"F4.wireOp",EDGE,"E7.21.10.0")}),1.0]])]});
            var Q461;
            Q461=makeQuery(id+"F4.imprint","IMPRINT",FACE,{"disambiguationData":[TD([[makeQuery(id+"F4.imprint","IMPRINT",EDGE,{"derivedFrom":sQuery(id+"F4.wireOp",EDGE,"E7.20.19.0")}),1.0]])]});
            var Q462;
            Q462=makeQuery(id+"F4.imprint","IMPRINT",FACE,{"disambiguationData":[TD([[makeQuery(id+"F4.imprint","IMPRINT",EDGE,{"derivedFrom":sQuery(id+"F4.wireOp",EDGE,"E7.20.3.0")}),1.0]])]});
            var Q463;
            Q463=makeQuery(id+"F4.imprint","IMPRINT",FACE,{"disambiguationData":[TD([[makeQuery(id+"F4.imprint","IMPRINT",EDGE,{"derivedFrom":sQuery(id+"F4.wireOp",EDGE,"E7.24.15.0")}),1.0]])]});
            var Q464;
            Q464=makeQuery(id+"F4.imprint","IMPRINT",FACE,{"disambiguationData":[TD([[makeQuery(id+"F4.imprint","IMPRINT",EDGE,{"derivedFrom":sQuery(id+"F4.wireOp",EDGE,"E7.23.24.0")}),1.0]])]});
            var Q465;
            Q465=makeQuery(id+"F4.imprint","IMPRINT",FACE,{"disambiguationData":[TD([[makeQuery(id+"F4.imprint","IMPRINT",EDGE,{"derivedFrom":sQuery(id+"F4.wireOp",EDGE,"E7.23.8.0")}),1.0]])]});
            var Q466;
            Q466=makeQuery(id+"F4.imprint","IMPRINT",FACE,{"disambiguationData":[TD([[makeQuery(id+"F4.imprint","IMPRINT",EDGE,{"derivedFrom":sQuery(id+"F4.wireOp",EDGE,"E7.22.17.0")}),1.0]])]});
            var Q467;
            Q467=makeQuery(id+"F4.imprint","IMPRINT",FACE,{"disambiguationData":[TD([[makeQuery(id+"F4.imprint","IMPRINT",EDGE,{"derivedFrom":sQuery(id+"F4.wireOp",EDGE,"E7.5.11.0")}),1.0]])]});
            var Q468;
            Q468=makeQuery(id+"F4.imprint","IMPRINT",FACE,{"disambiguationData":[TD([[makeQuery(id+"F4.imprint","IMPRINT",EDGE,{"derivedFrom":sQuery(id+"F4.wireOp",EDGE,"E7.4.4.0")}),1.0]])]});
            var Q469;
            Q469=makeQuery(id+"F4.imprint","IMPRINT",FACE,{"disambiguationData":[TD([[makeQuery(id+"F4.imprint","IMPRINT",EDGE,{"derivedFrom":sQuery(id+"F4.wireOp",EDGE,"E7.3.13.0")}),1.0]])]});
            var Q470;
            Q470=makeQuery(id+"F4.imprint","IMPRINT",FACE,{"disambiguationData":[TD([[makeQuery(id+"F4.imprint","IMPRINT",EDGE,{"derivedFrom":sQuery(id+"F4.wireOp",EDGE,"E7.8.0.0")}),1.0]])]});
            var Q471;
            Q471=makeQuery(id+"F4.imprint","IMPRINT",FACE,{"disambiguationData":[TD([[makeQuery(id+"F4.imprint","IMPRINT",EDGE,{"derivedFrom":sQuery(id+"F4.wireOp",EDGE,"E7.7.9.0")}),1.0]])]});
            var Q472;
            Q472=makeQuery(id+"F4.imprint","IMPRINT",FACE,{"disambiguationData":[TD([[makeQuery(id+"F4.imprint","IMPRINT",EDGE,{"derivedFrom":sQuery(id+"F4.wireOp",EDGE,"E7.6.2.0")}),1.0]])]});
            var Q473;
            Q473=makeQuery(id+"F4.imprint","IMPRINT",FACE,{"disambiguationData":[TD([[makeQuery(id+"F4.imprint","IMPRINT",EDGE,{"derivedFrom":sQuery(id+"F4.wireOp",EDGE,"E7.10.14.0")}),1.0]])]});
            var Q474;
            Q474=makeQuery(id+"F4.imprint","IMPRINT",FACE,{"disambiguationData":[TD([[makeQuery(id+"F4.imprint","IMPRINT",EDGE,{"derivedFrom":sQuery(id+"F4.wireOp",EDGE,"E7.9.23.0")}),1.0]])]});
            var Q475;
            Q475=makeQuery(id+"F4.imprint","IMPRINT",FACE,{"disambiguationData":[TD([[makeQuery(id+"F4.imprint","IMPRINT",EDGE,{"derivedFrom":sQuery(id+"F4.wireOp",EDGE,"E7.9.7.0")}),1.0]])]});
            var Q476;
            Q476=makeQuery(id+"F4.imprint","IMPRINT",FACE,{"disambiguationData":[TD([[makeQuery(id+"F4.imprint","IMPRINT",EDGE,{"derivedFrom":sQuery(id+"F4.wireOp",EDGE,"E7.12.12.0")}),1.0]])]});
            var Q477;
            Q477=makeQuery(id+"F4.imprint","IMPRINT",FACE,{"disambiguationData":[TD([[makeQuery(id+"F4.imprint","IMPRINT",EDGE,{"derivedFrom":sQuery(id+"F4.wireOp",EDGE,"E7.11.21.0")}),1.0]])]});
            var Q478;
            Q478=makeQuery(id+"F4.imprint","IMPRINT",FACE,{"disambiguationData":[TD([[makeQuery(id+"F4.imprint","IMPRINT",EDGE,{"derivedFrom":sQuery(id+"F4.wireOp",EDGE,"E7.11.5.0")}),1.0]])]});
            var Q479;
            Q479=makeQuery(id+"F4.imprint","IMPRINT",FACE,{"disambiguationData":[TD([[makeQuery(id+"F4.imprint","IMPRINT",EDGE,{"derivedFrom":sQuery(id+"F4.wireOp",EDGE,"E7.15.17.0")}),1.0]])]});
            var Q480;
            Q480=makeQuery(id+"F4.imprint","IMPRINT",FACE,{"disambiguationData":[TD([[makeQuery(id+"F4.imprint","IMPRINT",EDGE,{"derivedFrom":sQuery(id+"F4.wireOp",EDGE,"E7.14.10.0")}),1.0]])]});
            var Q481;
            Q481=makeQuery(id+"F4.imprint","IMPRINT",FACE,{"disambiguationData":[TD([[makeQuery(id+"F4.imprint","IMPRINT",EDGE,{"derivedFrom":sQuery(id+"F4.wireOp",EDGE,"E7.13.19.0")}),1.0]])]});
            var Q482;
            Q482=makeQuery(id+"F4.imprint","IMPRINT",FACE,{"disambiguationData":[TD([[makeQuery(id+"F4.imprint","IMPRINT",EDGE,{"derivedFrom":sQuery(id+"F4.wireOp",EDGE,"E7.16.8.0")}),1.0]])]});
            var Q483;
            Q483=makeQuery(id+"F4.imprint","IMPRINT",FACE,{"disambiguationData":[TD([[makeQuery(id+"F4.imprint","IMPRINT",EDGE,{"derivedFrom":sQuery(id+"F4.wireOp",EDGE,"E7.16.24.0")}),1.0]])]});
            var Q484;
            Q484=makeQuery(id+"F4.imprint","IMPRINT",FACE,{"disambiguationData":[TD([[makeQuery(id+"F4.imprint","IMPRINT",EDGE,{"derivedFrom":sQuery(id+"F4.wireOp",EDGE,"E7.19.13.0")}),1.0]])]});
            var Q485;
            Q485=makeQuery(id+"F4.imprint","IMPRINT",FACE,{"disambiguationData":[TD([[makeQuery(id+"F4.imprint","IMPRINT",EDGE,{"derivedFrom":sQuery(id+"F4.wireOp",EDGE,"E7.18.22.0")}),1.0]])]});
            var Q486;
            Q486=makeQuery(id+"F4.imprint","IMPRINT",FACE,{"disambiguationData":[TD([[makeQuery(id+"F4.imprint","IMPRINT",EDGE,{"derivedFrom":sQuery(id+"F4.wireOp",EDGE,"E7.18.6.0")}),1.0]])]});
            var Q487;
            Q487=makeQuery(id+"F4.imprint","IMPRINT",FACE,{"disambiguationData":[TD([[makeQuery(id+"F4.imprint","IMPRINT",EDGE,{"derivedFrom":sQuery(id+"F4.wireOp",EDGE,"E7.17.15.0")}),1.0]])]});
            var Q488;
            Q488=makeQuery(id+"F4.imprint","IMPRINT",FACE,{"disambiguationData":[TD([[makeQuery(id+"F4.imprint","IMPRINT",EDGE,{"derivedFrom":sQuery(id+"F4.wireOp",EDGE,"E7.2.6.0")}),1.0]])]});
            var Q489;
            Q489=makeQuery(id+"F4.imprint","IMPRINT",FACE,{"disambiguationData":[TD([[makeQuery(id+"F4.imprint","IMPRINT",EDGE,{"derivedFrom":sQuery(id+"F4.wireOp",EDGE,"E7.1.15.0")}),1.0]])]});
            var Q490;
            Q490=makeQuery(id+"F4.imprint","IMPRINT",FACE,{"disambiguationData":[TD([[makeQuery(id+"F4.imprint","IMPRINT",EDGE,{"derivedFrom":sQuery(id+"F4.wireOp",EDGE,"E7.22.2.0")}),1.0]])]});
            var Q491;
            Q491=makeQuery(id+"F4.imprint","IMPRINT",FACE,{"disambiguationData":[TD([[makeQuery(id+"F4.imprint","IMPRINT",EDGE,{"derivedFrom":sQuery(id+"F4.wireOp",EDGE,"E7.21.11.0")}),1.0]])]});
            var Q492;
            Q492=makeQuery(id+"F4.imprint","IMPRINT",FACE,{"disambiguationData":[TD([[makeQuery(id+"F4.imprint","IMPRINT",EDGE,{"derivedFrom":sQuery(id+"F4.wireOp",EDGE,"E7.20.20.0")}),1.0]])]});
            var Q493;
            Q493=makeQuery(id+"F4.imprint","IMPRINT",FACE,{"disambiguationData":[TD([[makeQuery(id+"F4.imprint","IMPRINT",EDGE,{"derivedFrom":sQuery(id+"F4.wireOp",EDGE,"E7.20.4.0")}),1.0]])]});
            var Q494;
            Q494=makeQuery(id+"F4.imprint","IMPRINT",FACE,{"disambiguationData":[TD([[makeQuery(id+"F4.imprint","IMPRINT",EDGE,{"derivedFrom":sQuery(id+"F4.wireOp",EDGE,"E7.24.0.0")}),1.0]])]});
            var Q495;
            Q495=makeQuery(id+"F4.imprint","IMPRINT",FACE,{"disambiguationData":[TD([[makeQuery(id+"F4.imprint","IMPRINT",EDGE,{"derivedFrom":sQuery(id+"F4.wireOp",EDGE,"E7.23.9.0")}),1.0]])]});
            var Q496;
            Q496=makeQuery(id+"F4.imprint","IMPRINT",FACE,{"disambiguationData":[TD([[makeQuery(id+"F4.imprint","IMPRINT",EDGE,{"derivedFrom":sQuery(id+"F4.wireOp",EDGE,"E7.7.10.0")}),1.0]])]});
            var Q497;
            Q497=makeQuery(id+"F4.imprint","IMPRINT",FACE,{"disambiguationData":[TD([[makeQuery(id+"F4.imprint","IMPRINT",EDGE,{"derivedFrom":sQuery(id+"F4.wireOp",EDGE,"E7.6.19.0")}),1.0]])]});
            var Q498;
            Q498=makeQuery(id+"F4.imprint","IMPRINT",FACE,{"disambiguationData":[TD([[makeQuery(id+"F4.imprint","IMPRINT",EDGE,{"derivedFrom":sQuery(id+"F4.wireOp",EDGE,"E7.10.15.0")}),1.0]])]});
            var Q499;
            Q499=makeQuery(id+"F4.imprint","IMPRINT",FACE,{"disambiguationData":[TD([[makeQuery(id+"F4.imprint","IMPRINT",EDGE,{"derivedFrom":sQuery(id+"F4.wireOp",EDGE,"E7.9.24.0")}),1.0]])]});
            var Q500;
            Q500=makeQuery(id+"F4.imprint","IMPRINT",FACE,{"disambiguationData":[TD([[makeQuery(id+"F4.imprint","IMPRINT",EDGE,{"derivedFrom":sQuery(id+"F4.wireOp",EDGE,"E7.9.8.0")}),1.0]])]});
            var Q501;
            Q501=makeQuery(id+"F4.imprint","IMPRINT",FACE,{"disambiguationData":[TD([[makeQuery(id+"F4.imprint","IMPRINT",EDGE,{"derivedFrom":sQuery(id+"F4.wireOp",EDGE,"E7.8.17.0")}),1.0]])]});
            var Q502;
            Q502=makeQuery(id+"F4.imprint","IMPRINT",FACE,{"disambiguationData":[TD([[makeQuery(id+"F4.imprint","IMPRINT",EDGE,{"derivedFrom":sQuery(id+"F4.wireOp",EDGE,"E7.13.4.0")}),1.0]])]});
            var Q503;
            Q503=makeQuery(id+"F4.imprint","IMPRINT",FACE,{"disambiguationData":[TD([[makeQuery(id+"F4.imprint","IMPRINT",EDGE,{"derivedFrom":sQuery(id+"F4.wireOp",EDGE,"E7.12.13.0")}),1.0]])]});
            var Q504;
            Q504=makeQuery(id+"F4.imprint","IMPRINT",FACE,{"disambiguationData":[TD([[makeQuery(id+"F4.imprint","IMPRINT",EDGE,{"derivedFrom":sQuery(id+"F4.wireOp",EDGE,"E7.11.6.0")}),1.0]])]});
            var Q505;
            Q505=makeQuery(id+"F4.imprint","IMPRINT",FACE,{"disambiguationData":[TD([[makeQuery(id+"F4.imprint","IMPRINT",EDGE,{"derivedFrom":sQuery(id+"F4.wireOp",EDGE,"E7.15.2.0")}),1.0]])]});
            var Q506;
            Q506=makeQuery(id+"F4.imprint","IMPRINT",FACE,{"disambiguationData":[TD([[makeQuery(id+"F4.imprint","IMPRINT",EDGE,{"derivedFrom":sQuery(id+"F4.wireOp",EDGE,"E7.14.11.0")}),1.0]])]});
            var Q507;
            Q507=makeQuery(id+"F4.imprint","IMPRINT",FACE,{"disambiguationData":[TD([[makeQuery(id+"F4.imprint","IMPRINT",EDGE,{"derivedFrom":sQuery(id+"F4.wireOp",EDGE,"E7.16.9.0")}),1.0]])]});
            var Q508;
            Q508=makeQuery(id+"F4.imprint","IMPRINT",FACE,{"disambiguationData":[TD([[makeQuery(id+"F4.imprint","IMPRINT",EDGE,{"derivedFrom":sQuery(id+"F4.wireOp",EDGE,"E7.17.0.0")}),1.0]])]});
            var Q509;
            Q509=makeQuery(id+"F4.imprint","IMPRINT",FACE,{"disambiguationData":[TD([[makeQuery(id+"F4.imprint","IMPRINT",EDGE,{"derivedFrom":sQuery(id+"F4.wireOp",EDGE,"E7.18.23.0")}),1.0]])]});
            var Q510;
            Q510=makeQuery(id+"F4.imprint","IMPRINT",FACE,{"disambiguationData":[TD([[makeQuery(id+"F4.imprint","IMPRINT",EDGE,{"derivedFrom":sQuery(id+"F4.wireOp",EDGE,"E7.18.7.0")}),1.0]])]});
            var Q511;
            Q511=makeQuery(id+"F4.imprint","IMPRINT",FACE,{"disambiguationData":[TD([[makeQuery(id+"F4.imprint","IMPRINT",EDGE,{"derivedFrom":sQuery(id+"F4.wireOp",EDGE,"E7.22.3.0")}),1.0]])]});
            var Q512;
            Q512=makeQuery(id+"F4.imprint","IMPRINT",FACE,{"disambiguationData":[TD([[makeQuery(id+"F4.imprint","IMPRINT",EDGE,{"derivedFrom":sQuery(id+"F4.wireOp",EDGE,"E7.21.12.0")}),1.0]])]});
            var Q513;
            Q513=makeQuery(id+"F4.imprint","IMPRINT",FACE,{"disambiguationData":[TD([[makeQuery(id+"F4.imprint","IMPRINT",EDGE,{"derivedFrom":sQuery(id+"F4.wireOp",EDGE,"E7.20.21.0")}),1.0]])]});
            var Q514;
            Q514=makeQuery(id+"F4.imprint","IMPRINT",FACE,{"disambiguationData":[TD([[makeQuery(id+"F4.imprint","IMPRINT",EDGE,{"derivedFrom":sQuery(id+"F4.wireOp",EDGE,"E7.20.5.0")}),1.0]])]});
            var Q515;
            Q515=makeQuery(id+"F4.imprint","IMPRINT",FACE,{"disambiguationData":[TD([[makeQuery(id+"F4.imprint","IMPRINT",EDGE,{"derivedFrom":sQuery(id+"F4.wireOp",EDGE,"E7.2.23.0")}),1.0]])]});
            var Q516;
            Q516=makeQuery(id+"F4.imprint","IMPRINT",FACE,{"disambiguationData":[TD([[makeQuery(id+"F4.imprint","IMPRINT",EDGE,{"derivedFrom":sQuery(id+"F4.wireOp",EDGE,"E7.2.7.0")}),1.0]])]});
            var Q517;
            Q517=makeQuery(id+"F4.imprint","IMPRINT",FACE,{"disambiguationData":[TD([[makeQuery(id+"F4.imprint","IMPRINT",EDGE,{"derivedFrom":sQuery(id+"F4.wireOp",EDGE,"E7.1.16.0")}),1.0]])]});
            var Q518;
            Q518=makeQuery(id+"F4.imprint","IMPRINT",FACE,{"disambiguationData":[TD([[makeQuery(id+"F4.imprint","IMPRINT",EDGE,{"derivedFrom":sQuery(id+"F4.wireOp",EDGE,"E7.5.12.0")}),1.0]])]});
            var Q519;
            Q519=makeQuery(id+"F4.imprint","IMPRINT",FACE,{"disambiguationData":[TD([[makeQuery(id+"F4.imprint","IMPRINT",EDGE,{"derivedFrom":sQuery(id+"F4.wireOp",EDGE,"E7.4.21.0")}),1.0]])]});
            var Q520;
            Q520=makeQuery(id+"F4.imprint","IMPRINT",FACE,{"disambiguationData":[TD([[makeQuery(id+"F4.imprint","IMPRINT",EDGE,{"derivedFrom":sQuery(id+"F4.wireOp",EDGE,"E7.3.14.0")}),1.0]])]});
            var Q521;
            Q521=makeQuery(id+"F4.imprint","IMPRINT",FACE,{"disambiguationData":[TD([[makeQuery(id+"F4.imprint","IMPRINT",EDGE,{"derivedFrom":sQuery(id+"F4.wireOp",EDGE,"E7.24.17.0")}),1.0]])]});
            var Q522;
            Q522=makeQuery(id+"F4.imprint","IMPRINT",FACE,{"disambiguationData":[TD([[makeQuery(id+"F4.imprint","IMPRINT",EDGE,{"derivedFrom":sQuery(id+"F4.wireOp",EDGE,"E7.23.10.0")}),1.0]])]});
            var Q523;
            Q523=makeQuery(id+"F4.imprint","IMPRINT",FACE,{"disambiguationData":[TD([[makeQuery(id+"F4.imprint","IMPRINT",EDGE,{"derivedFrom":sQuery(id+"F4.wireOp",EDGE,"E7.22.19.0")}),1.0]])]});
            var Q524;
            Q524=makeQuery(id+"F4.imprint","IMPRINT",FACE,{"disambiguationData":[TD([[makeQuery(id+"F4.imprint","IMPRINT",EDGE,{"derivedFrom":sQuery(id+"F4.wireOp",EDGE,"E7.10.16.0")}),1.0]])]});
            var Q525;
            Q525=makeQuery(id+"F4.imprint","IMPRINT",FACE,{"disambiguationData":[TD([[makeQuery(id+"F4.imprint","IMPRINT",EDGE,{"derivedFrom":sQuery(id+"F4.wireOp",EDGE,"E7.10.0.0")}),1.0]])]});
            var Q526;
            Q526=makeQuery(id+"F4.imprint","IMPRINT",FACE,{"disambiguationData":[TD([[makeQuery(id+"F4.imprint","IMPRINT",EDGE,{"derivedFrom":sQuery(id+"F4.wireOp",EDGE,"E7.9.9.0")}),1.0]])]});
            var Q527;
            Q527=makeQuery(id+"F4.imprint","IMPRINT",FACE,{"disambiguationData":[TD([[makeQuery(id+"F4.imprint","IMPRINT",EDGE,{"derivedFrom":sQuery(id+"F4.wireOp",EDGE,"E7.12.14.0")}),1.0]])]});
            var Q528;
            Q528=makeQuery(id+"F4.imprint","IMPRINT",FACE,{"disambiguationData":[TD([[makeQuery(id+"F4.imprint","IMPRINT",EDGE,{"derivedFrom":sQuery(id+"F4.wireOp",EDGE,"E7.11.23.0")}),1.0]])]});
            var Q529;
            Q529=makeQuery(id+"F4.imprint","IMPRINT",FACE,{"disambiguationData":[TD([[makeQuery(id+"F4.imprint","IMPRINT",EDGE,{"derivedFrom":sQuery(id+"F4.wireOp",EDGE,"E7.11.7.0")}),1.0]])]});
            var Q530;
            Q530=makeQuery(id+"F4.imprint","IMPRINT",FACE,{"disambiguationData":[TD([[makeQuery(id+"F4.imprint","IMPRINT",EDGE,{"derivedFrom":sQuery(id+"F4.wireOp",EDGE,"E7.15.19.0")}),1.0]])]});
            var Q531;
            Q531=makeQuery(id+"F4.imprint","IMPRINT",FACE,{"disambiguationData":[TD([[makeQuery(id+"F4.imprint","IMPRINT",EDGE,{"derivedFrom":sQuery(id+"F4.wireOp",EDGE,"E7.14.12.0")}),1.0]])]});
            var Q532;
            Q532=makeQuery(id+"F4.imprint","IMPRINT",FACE,{"disambiguationData":[TD([[makeQuery(id+"F4.imprint","IMPRINT",EDGE,{"derivedFrom":sQuery(id+"F4.wireOp",EDGE,"E7.13.21.0")}),1.0]])]});
            var Q533;
            Q533=makeQuery(id+"F4.imprint","IMPRINT",FACE,{"disambiguationData":[TD([[makeQuery(id+"F4.imprint","IMPRINT",EDGE,{"derivedFrom":sQuery(id+"F4.wireOp",EDGE,"E7.16.10.0")}),1.0]])]});
            var Q534;
            Q534=makeQuery(id+"F4.imprint","IMPRINT",FACE,{"disambiguationData":[TD([[makeQuery(id+"F4.imprint","IMPRINT",EDGE,{"derivedFrom":sQuery(id+"F4.wireOp",EDGE,"E7.19.15.0")}),1.0]])]});
            var Q535;
            Q535=makeQuery(id+"F4.imprint","IMPRINT",FACE,{"disambiguationData":[TD([[makeQuery(id+"F4.imprint","IMPRINT",EDGE,{"derivedFrom":sQuery(id+"F4.wireOp",EDGE,"E7.18.24.0")}),1.0]])]});
            var Q536;
            Q536=makeQuery(id+"F4.imprint","IMPRINT",FACE,{"disambiguationData":[TD([[makeQuery(id+"F4.imprint","IMPRINT",EDGE,{"derivedFrom":sQuery(id+"F4.wireOp",EDGE,"E7.18.8.0")}),1.0]])]});
            var Q537;
            Q537=makeQuery(id+"F4.imprint","IMPRINT",FACE,{"disambiguationData":[TD([[makeQuery(id+"F4.imprint","IMPRINT",EDGE,{"derivedFrom":sQuery(id+"F4.wireOp",EDGE,"E7.17.17.0")}),1.0]])]});
            var Q538;
            Q538=makeQuery(id+"F4.imprint","IMPRINT",FACE,{"disambiguationData":[TD([[makeQuery(id+"F4.imprint","IMPRINT",EDGE,{"derivedFrom":sQuery(id+"F4.wireOp",EDGE,"E7.22.4.0")}),1.0]])]});
            var Q539;
            Q539=makeQuery(id+"F4.imprint","IMPRINT",FACE,{"disambiguationData":[TD([[makeQuery(id+"F4.imprint","IMPRINT",EDGE,{"derivedFrom":sQuery(id+"F4.wireOp",EDGE,"E7.21.13.0")}),1.0]])]});
            var Q540;
            Q540=makeQuery(id+"F4.imprint","IMPRINT",FACE,{"disambiguationData":[TD([[makeQuery(id+"F4.imprint","IMPRINT",EDGE,{"derivedFrom":sQuery(id+"F4.wireOp",EDGE,"E7.20.22.0")}),1.0]])]});
            var Q541;
            Q541=makeQuery(id+"F4.imprint","IMPRINT",FACE,{"disambiguationData":[TD([[makeQuery(id+"F4.imprint","IMPRINT",EDGE,{"derivedFrom":sQuery(id+"F4.wireOp",EDGE,"E7.20.6.0")}),1.0]])]});
            var Q542;
            Q542=makeQuery(id+"F4.imprint","IMPRINT",FACE,{"disambiguationData":[TD([[makeQuery(id+"F4.imprint","IMPRINT",EDGE,{"derivedFrom":sQuery(id+"F4.wireOp",EDGE,"E7.24.2.0")}),1.0]])]});
            var Q543;
            Q543=makeQuery(id+"F4.imprint","IMPRINT",FACE,{"disambiguationData":[TD([[makeQuery(id+"F4.imprint","IMPRINT",EDGE,{"derivedFrom":sQuery(id+"F4.wireOp",EDGE,"E7.23.11.0")}),1.0]])]});
            var Q544;
            Q544=makeQuery(id+"F4.imprint","IMPRINT",FACE,{"disambiguationData":[TD([[makeQuery(id+"F4.imprint","IMPRINT",EDGE,{"derivedFrom":sQuery(id+"F4.wireOp",EDGE,"E7.2.8.0")}),1.0]])]});
            var Q545;
            Q545=makeQuery(id+"F4.imprint","IMPRINT",FACE,{"disambiguationData":[TD([[makeQuery(id+"F4.imprint","IMPRINT",EDGE,{"derivedFrom":sQuery(id+"F4.wireOp",EDGE,"E7.1.17.0")}),1.0]])]});
            var Q546;
            Q546=makeQuery(id+"F4.imprint","IMPRINT",FACE,{"disambiguationData":[TD([[makeQuery(id+"F4.imprint","IMPRINT",EDGE,{"derivedFrom":sQuery(id+"F4.wireOp",EDGE,"E7.1.1.0")}),1.0]])]});
            var Q547;
            Q547=makeQuery(id+"F4.imprint","IMPRINT",FACE,{"disambiguationData":[TD([[makeQuery(id+"F4.imprint","IMPRINT",EDGE,{"derivedFrom":sQuery(id+"F4.wireOp",EDGE,"E7.5.13.0")}),1.0]])]});
            var Q548;
            Q548=makeQuery(id+"F4.imprint","IMPRINT",FACE,{"disambiguationData":[TD([[makeQuery(id+"F4.imprint","IMPRINT",EDGE,{"derivedFrom":sQuery(id+"F4.wireOp",EDGE,"E7.4.6.0")}),1.0]])]});
            var Q549;
            Q549=makeQuery(id+"F4.imprint","IMPRINT",FACE,{"disambiguationData":[TD([[makeQuery(id+"F4.imprint","IMPRINT",EDGE,{"derivedFrom":sQuery(id+"F4.wireOp",EDGE,"E7.3.15.0")}),1.0]])]});
            var Q550;
            Q550=makeQuery(id+"F4.imprint","IMPRINT",FACE,{"disambiguationData":[TD([[makeQuery(id+"F4.imprint","IMPRINT",EDGE,{"derivedFrom":sQuery(id+"F4.wireOp",EDGE,"E7.8.2.0")}),1.0]])]});
            var Q551;
            Q551=makeQuery(id+"F4.imprint","IMPRINT",FACE,{"disambiguationData":[TD([[makeQuery(id+"F4.imprint","IMPRINT",EDGE,{"derivedFrom":sQuery(id+"F4.wireOp",EDGE,"E7.7.11.0")}),1.0]])]});
            var Q552;
            Q552=makeQuery(id+"F4.imprint","IMPRINT",FACE,{"disambiguationData":[TD([[makeQuery(id+"F4.imprint","IMPRINT",EDGE,{"derivedFrom":sQuery(id+"F4.wireOp",EDGE,"E7.6.4.0")}),1.0]])]});
            var Q553;
            Q553=makeQuery(id+"F4.imprint","IMPRINT",FACE,{"disambiguationData":[TD([[makeQuery(id+"F4.imprint","IMPRINT",EDGE,{"derivedFrom":sQuery(id+"F4.wireOp",EDGE,"E7.13.6.0")}),1.0]])]});
            var Q554;
            Q554=makeQuery(id+"F4.imprint","IMPRINT",FACE,{"disambiguationData":[TD([[makeQuery(id+"F4.imprint","IMPRINT",EDGE,{"derivedFrom":sQuery(id+"F4.wireOp",EDGE,"E7.12.15.0")}),1.0]])]});
            var Q555;
            Q555=makeQuery(id+"F4.imprint","IMPRINT",FACE,{"disambiguationData":[TD([[makeQuery(id+"F4.imprint","IMPRINT",EDGE,{"derivedFrom":sQuery(id+"F4.wireOp",EDGE,"E7.11.8.0")}),1.0]])]});
            var Q556;
            Q556=makeQuery(id+"F4.imprint","IMPRINT",FACE,{"disambiguationData":[TD([[makeQuery(id+"F4.imprint","IMPRINT",EDGE,{"derivedFrom":sQuery(id+"F4.wireOp",EDGE,"E7.15.4.0")}),1.0]])]});
            var Q557;
            Q557=makeQuery(id+"F4.imprint","IMPRINT",FACE,{"disambiguationData":[TD([[makeQuery(id+"F4.imprint","IMPRINT",EDGE,{"derivedFrom":sQuery(id+"F4.wireOp",EDGE,"E7.14.13.0")}),1.0]])]});
            var Q558;
            Q558=makeQuery(id+"F4.imprint","IMPRINT",FACE,{"disambiguationData":[TD([[makeQuery(id+"F4.imprint","IMPRINT",EDGE,{"derivedFrom":sQuery(id+"F4.wireOp",EDGE,"E7.16.11.0")}),1.0]])]});
            var Q559;
            Q559=makeQuery(id+"F4.imprint","IMPRINT",FACE,{"disambiguationData":[TD([[makeQuery(id+"F4.imprint","IMPRINT",EDGE,{"derivedFrom":sQuery(id+"F4.wireOp",EDGE,"E7.17.2.0")}),1.0]])]});
            var Q560;
            Q560=makeQuery(id+"F4.imprint","IMPRINT",FACE,{"disambiguationData":[TD([[makeQuery(id+"F4.imprint","IMPRINT",EDGE,{"derivedFrom":sQuery(id+"F4.wireOp",EDGE,"E7.19.0.0")}),1.0]])]});
            var Q561;
            Q561=makeQuery(id+"F4.imprint","IMPRINT",FACE,{"disambiguationData":[TD([[makeQuery(id+"F4.imprint","IMPRINT",EDGE,{"derivedFrom":sQuery(id+"F4.wireOp",EDGE,"E7.18.9.0")}),1.0]])]});
            var Q562;
            Q562=makeQuery(id+"F4.imprint","IMPRINT",FACE,{"disambiguationData":[TD([[makeQuery(id+"F4.imprint","IMPRINT",EDGE,{"derivedFrom":sQuery(id+"F4.wireOp",EDGE,"E7.22.5.0")}),1.0]])]});
            var Q563;
            Q563=makeQuery(id+"F4.imprint","IMPRINT",FACE,{"disambiguationData":[TD([[makeQuery(id+"F4.imprint","IMPRINT",EDGE,{"derivedFrom":sQuery(id+"F4.wireOp",EDGE,"E7.21.14.0")}),1.0]])]});
            var Q564;
            Q564=makeQuery(id+"F4.imprint","IMPRINT",FACE,{"disambiguationData":[TD([[makeQuery(id+"F4.imprint","IMPRINT",EDGE,{"derivedFrom":sQuery(id+"F4.wireOp",EDGE,"E7.20.23.0")}),1.0]])]});
            var Q565;
            Q565=makeQuery(id+"F4.imprint","IMPRINT",FACE,{"disambiguationData":[TD([[makeQuery(id+"F4.imprint","IMPRINT",EDGE,{"derivedFrom":sQuery(id+"F4.wireOp",EDGE,"E7.20.7.0")}),1.0]])]});
            var Q566;
            Q566=makeQuery(id+"F4.imprint","IMPRINT",FACE,{"disambiguationData":[TD([[makeQuery(id+"F4.imprint","IMPRINT",EDGE,{"derivedFrom":sQuery(id+"F4.wireOp",EDGE,"E7.24.19.0")}),1.0]])]});
            var Q567;
            Q567=makeQuery(id+"F4.imprint","IMPRINT",FACE,{"disambiguationData":[TD([[makeQuery(id+"F4.imprint","IMPRINT",EDGE,{"derivedFrom":sQuery(id+"F4.wireOp",EDGE,"E7.23.12.0")}),1.0]])]});
            var Q568;
            Q568=makeQuery(id+"F4.imprint","IMPRINT",FACE,{"disambiguationData":[TD([[makeQuery(id+"F4.imprint","IMPRINT",EDGE,{"derivedFrom":sQuery(id+"F4.wireOp",EDGE,"E7.22.21.0")}),1.0]])]});
            var Q569;
            Q569=makeQuery(id+"F4.imprint","IMPRINT",FACE,{"disambiguationData":[TD([[makeQuery(id+"F4.imprint","IMPRINT",EDGE,{"derivedFrom":sQuery(id+"F4.wireOp",EDGE,"E7.3.0.0")}),1.0]])]});
            var Q570;
            Q570=makeQuery(id+"F4.imprint","IMPRINT",FACE,{"disambiguationData":[TD([[makeQuery(id+"F4.imprint","IMPRINT",EDGE,{"derivedFrom":sQuery(id+"F4.wireOp",EDGE,"E7.2.9.0")}),1.0]])]});
            var Q571;
            Q571=makeQuery(id+"F4.imprint","IMPRINT",FACE,{"disambiguationData":[TD([[makeQuery(id+"F4.imprint","IMPRINT",EDGE,{"derivedFrom":sQuery(id+"F4.wireOp",EDGE,"E7.1.18.0")}),1.0]])]});
            var Q572;
            Q572=makeQuery(id+"F4.imprint","IMPRINT",FACE,{"disambiguationData":[TD([[makeQuery(id+"F4.imprint","IMPRINT",EDGE,{"derivedFrom":sQuery(id+"F4.wireOp",EDGE,"E7.1.2.0")}),1.0]])]});
            var Q573;
            Q573=makeQuery(id+"F4.imprint","IMPRINT",FACE,{"disambiguationData":[TD([[makeQuery(id+"F4.imprint","IMPRINT",EDGE,{"derivedFrom":sQuery(id+"F4.wireOp",EDGE,"E7.5.14.0")}),1.0]])]});
            var Q574;
            Q574=makeQuery(id+"F4.imprint","IMPRINT",FACE,{"disambiguationData":[TD([[makeQuery(id+"F4.imprint","IMPRINT",EDGE,{"derivedFrom":sQuery(id+"F4.wireOp",EDGE,"E7.4.23.0")}),1.0]])]});
            var Q575;
            Q575=makeQuery(id+"F4.imprint","IMPRINT",FACE,{"disambiguationData":[TD([[makeQuery(id+"F4.imprint","IMPRINT",EDGE,{"derivedFrom":sQuery(id+"F4.wireOp",EDGE,"E7.4.7.0")}),1.0]])]});
            var Q576;
            Q576=makeQuery(id+"F4.imprint","IMPRINT",FACE,{"disambiguationData":[TD([[makeQuery(id+"F4.imprint","IMPRINT",EDGE,{"derivedFrom":sQuery(id+"F4.wireOp",EDGE,"E7.3.16.0")}),1.0]])]});
            var Q577;
            Q577=makeQuery(id+"F4.imprint","IMPRINT",FACE,{"disambiguationData":[TD([[makeQuery(id+"F4.imprint","IMPRINT",EDGE,{"derivedFrom":sQuery(id+"F4.wireOp",EDGE,"E7.8.3.0")}),1.0]])]});
            var Q578;
            Q578=makeQuery(id+"F4.imprint","IMPRINT",FACE,{"disambiguationData":[TD([[makeQuery(id+"F4.imprint","IMPRINT",EDGE,{"derivedFrom":sQuery(id+"F4.wireOp",EDGE,"E7.7.12.0")}),1.0]])]});
            var Q579;
            Q579=makeQuery(id+"F4.imprint","IMPRINT",FACE,{"disambiguationData":[TD([[makeQuery(id+"F4.imprint","IMPRINT",EDGE,{"derivedFrom":sQuery(id+"F4.wireOp",EDGE,"E7.6.21.0")}),1.0]])]});
            var Q580;
            Q580=makeQuery(id+"F4.imprint","IMPRINT",FACE,{"disambiguationData":[TD([[makeQuery(id+"F4.imprint","IMPRINT",EDGE,{"derivedFrom":sQuery(id+"F4.wireOp",EDGE,"E7.10.17.0")}),1.0]])]});
            var Q581;
            Q581=makeQuery(id+"F4.imprint","IMPRINT",FACE,{"disambiguationData":[TD([[makeQuery(id+"F4.imprint","IMPRINT",EDGE,{"derivedFrom":sQuery(id+"F4.wireOp",EDGE,"E7.10.1.0")}),1.0]])]});
            var Q582;
            Q582=makeQuery(id+"F4.imprint","IMPRINT",FACE,{"disambiguationData":[TD([[makeQuery(id+"F4.imprint","IMPRINT",EDGE,{"derivedFrom":sQuery(id+"F4.wireOp",EDGE,"E7.9.10.0")}),1.0]])]});
            var Q583;
            Q583=makeQuery(id+"F4.imprint","IMPRINT",FACE,{"disambiguationData":[TD([[makeQuery(id+"F4.imprint","IMPRINT",EDGE,{"derivedFrom":sQuery(id+"F4.wireOp",EDGE,"E7.8.19.0")}),1.0]])]});
            var Q584;
            Q584=makeQuery(id+"F4.imprint","IMPRINT",FACE,{"disambiguationData":[TD([[makeQuery(id+"F4.imprint","IMPRINT",EDGE,{"derivedFrom":sQuery(id+"F4.wireOp",EDGE,"E7.15.21.0")}),1.0]])]});
            var Q585;
            Q585=makeQuery(id+"F4.imprint","IMPRINT",FACE,{"disambiguationData":[TD([[makeQuery(id+"F4.imprint","IMPRINT",EDGE,{"derivedFrom":sQuery(id+"F4.wireOp",EDGE,"E7.14.14.0")}),1.0]])]});
            var Q586;
            Q586=makeQuery(id+"F4.imprint","IMPRINT",FACE,{"disambiguationData":[TD([[makeQuery(id+"F4.imprint","IMPRINT",EDGE,{"derivedFrom":sQuery(id+"F4.wireOp",EDGE,"E7.13.23.0")}),1.0]])]});
            var Q587;
            Q587=makeQuery(id+"F4.imprint","IMPRINT",FACE,{"disambiguationData":[TD([[makeQuery(id+"F4.imprint","IMPRINT",EDGE,{"derivedFrom":sQuery(id+"F4.wireOp",EDGE,"E7.16.12.0")}),1.0]])]});
            var Q588;
            Q588=makeQuery(id+"F4.imprint","IMPRINT",FACE,{"disambiguationData":[TD([[makeQuery(id+"F4.imprint","IMPRINT",EDGE,{"derivedFrom":sQuery(id+"F4.wireOp",EDGE,"E7.19.17.0")}),1.0]])]});
            var Q589;
            Q589=makeQuery(id+"F4.imprint","IMPRINT",FACE,{"disambiguationData":[TD([[makeQuery(id+"F4.imprint","IMPRINT",EDGE,{"derivedFrom":sQuery(id+"F4.wireOp",EDGE,"E7.18.10.0")}),1.0]])]});
            var Q590;
            Q590=makeQuery(id+"F4.imprint","IMPRINT",FACE,{"disambiguationData":[TD([[makeQuery(id+"F4.imprint","IMPRINT",EDGE,{"derivedFrom":sQuery(id+"F4.wireOp",EDGE,"E7.17.19.0")}),1.0]])]});
            var Q591;
            Q591=makeQuery(id+"F4.imprint","IMPRINT",FACE,{"disambiguationData":[TD([[makeQuery(id+"F4.imprint","IMPRINT",EDGE,{"derivedFrom":sQuery(id+"F4.wireOp",EDGE,"E7.22.6.0")}),1.0]])]});
            var Q592;
            Q592=makeQuery(id+"F4.imprint","IMPRINT",FACE,{"disambiguationData":[TD([[makeQuery(id+"F4.imprint","IMPRINT",EDGE,{"derivedFrom":sQuery(id+"F4.wireOp",EDGE,"E7.21.15.0")}),1.0]])]});
            var Q593;
            Q593=makeQuery(id+"F4.imprint","IMPRINT",FACE,{"disambiguationData":[TD([[makeQuery(id+"F4.imprint","IMPRINT",EDGE,{"derivedFrom":sQuery(id+"F4.wireOp",EDGE,"E7.20.24.0")}),1.0]])]});
            var Q594;
            Q594=makeQuery(id+"F4.imprint","IMPRINT",FACE,{"disambiguationData":[TD([[makeQuery(id+"F4.imprint","IMPRINT",EDGE,{"derivedFrom":sQuery(id+"F4.wireOp",EDGE,"E7.20.8.0")}),1.0]])]});
            var Q595;
            Q595=makeQuery(id+"F4.imprint","IMPRINT",FACE,{"disambiguationData":[TD([[makeQuery(id+"F4.imprint","IMPRINT",EDGE,{"derivedFrom":sQuery(id+"F4.wireOp",EDGE,"E7.24.4.0")}),1.0]])]});
            var Q596;
            Q596=makeQuery(id+"F4.imprint","IMPRINT",FACE,{"disambiguationData":[TD([[makeQuery(id+"F4.imprint","IMPRINT",EDGE,{"derivedFrom":sQuery(id+"F4.wireOp",EDGE,"E7.23.13.0")}),1.0]])]});
            var Q597;
            Q597=makeQuery(id+"F4.imprint","IMPRINT",FACE,{"disambiguationData":[TD([[makeQuery(id+"F4.imprint","IMPRINT",EDGE,{"derivedFrom":sQuery(id+"F4.wireOp",EDGE,"E7.3.1.0")}),1.0]])]});
            var Q598;
            Q598=makeQuery(id+"F4.imprint","IMPRINT",FACE,{"disambiguationData":[TD([[makeQuery(id+"F4.imprint","IMPRINT",EDGE,{"derivedFrom":sQuery(id+"F4.wireOp",EDGE,"E7.1.19.0")}),1.0]])]});
            var Q599;
            Q599=makeQuery(id+"F4.imprint","IMPRINT",FACE,{"disambiguationData":[TD([[makeQuery(id+"F4.imprint","IMPRINT",EDGE,{"derivedFrom":sQuery(id+"F4.wireOp",EDGE,"E7.1.3.0")}),1.0]])]});
            var Q600;
            Q600=makeQuery(id+"F4.imprint","IMPRINT",FACE,{"disambiguationData":[TD([[makeQuery(id+"F4.imprint","IMPRINT",EDGE,{"derivedFrom":sQuery(id+"F4.wireOp",EDGE,"E7.5.15.0")}),1.0]])]});
            var Q601;
            Q601=makeQuery(id+"F4.imprint","IMPRINT",FACE,{"disambiguationData":[TD([[makeQuery(id+"F4.imprint","IMPRINT",EDGE,{"derivedFrom":sQuery(id+"F4.wireOp",EDGE,"E7.4.8.0")}),1.0]])]});
            var Q602;
            Q602=makeQuery(id+"F4.imprint","IMPRINT",FACE,{"disambiguationData":[TD([[makeQuery(id+"F4.imprint","IMPRINT",EDGE,{"derivedFrom":sQuery(id+"F4.wireOp",EDGE,"E7.3.17.0")}),1.0]])]});
            var Q603;
            Q603=makeQuery(id+"F4.imprint","IMPRINT",FACE,{"disambiguationData":[TD([[makeQuery(id+"F4.imprint","IMPRINT",EDGE,{"derivedFrom":sQuery(id+"F4.wireOp",EDGE,"E7.8.4.0")}),1.0]])]});
            var Q604;
            Q604=makeQuery(id+"F4.imprint","IMPRINT",FACE,{"disambiguationData":[TD([[makeQuery(id+"F4.imprint","IMPRINT",EDGE,{"derivedFrom":sQuery(id+"F4.wireOp",EDGE,"E7.7.13.0")}),1.0]])]});
            var Q605;
            Q605=makeQuery(id+"F4.imprint","IMPRINT",FACE,{"disambiguationData":[TD([[makeQuery(id+"F4.imprint","IMPRINT",EDGE,{"derivedFrom":sQuery(id+"F4.wireOp",EDGE,"E7.6.6.0")}),1.0]])]});
            var Q606;
            Q606=makeQuery(id+"F4.imprint","IMPRINT",FACE,{"disambiguationData":[TD([[makeQuery(id+"F4.imprint","IMPRINT",EDGE,{"derivedFrom":sQuery(id+"F4.wireOp",EDGE,"E7.10.18.0")}),1.0]])]});
            var Q607;
            Q607=makeQuery(id+"F4.imprint","IMPRINT",FACE,{"disambiguationData":[TD([[makeQuery(id+"F4.imprint","IMPRINT",EDGE,{"derivedFrom":sQuery(id+"F4.wireOp",EDGE,"E7.10.2.0")}),1.0]])]});
            var Q608;
            Q608=makeQuery(id+"F4.imprint","IMPRINT",FACE,{"disambiguationData":[TD([[makeQuery(id+"F4.imprint","IMPRINT",EDGE,{"derivedFrom":sQuery(id+"F4.wireOp",EDGE,"E7.9.11.0")}),1.0]])]});
            var Q609;
            Q609=makeQuery(id+"F4.imprint","IMPRINT",FACE,{"disambiguationData":[TD([[makeQuery(id+"F4.imprint","IMPRINT",EDGE,{"derivedFrom":sQuery(id+"F4.wireOp",EDGE,"E7.13.7.0")}),1.0]])]});
            var Q610;
            Q610=makeQuery(id+"F4.imprint","IMPRINT",FACE,{"disambiguationData":[TD([[makeQuery(id+"F4.imprint","IMPRINT",EDGE,{"derivedFrom":sQuery(id+"F4.wireOp",EDGE,"E7.12.16.0")}),1.0]])]});
            var Q611;
            Q611=makeQuery(id+"F4.imprint","IMPRINT",FACE,{"disambiguationData":[TD([[makeQuery(id+"F4.imprint","IMPRINT",EDGE,{"derivedFrom":sQuery(id+"F4.wireOp",EDGE,"E7.12.0.0")}),1.0]])]});
            var Q612;
            Q612=makeQuery(id+"F4.imprint","IMPRINT",FACE,{"disambiguationData":[TD([[makeQuery(id+"F4.imprint","IMPRINT",EDGE,{"derivedFrom":sQuery(id+"F4.wireOp",EDGE,"E7.11.9.0")}),1.0]])]});
            var Q613;
            Q613=makeQuery(id+"F4.imprint","IMPRINT",FACE,{"disambiguationData":[TD([[makeQuery(id+"F4.imprint","IMPRINT",EDGE,{"derivedFrom":sQuery(id+"F4.wireOp",EDGE,"E7.0.15.0")}),1.0]])]});
            var Q614;
            Q614=makeQuery(id+"F4.imprint","IMPRINT",FACE,{"disambiguationData":[TD([[makeQuery(id+"F4.imprint","IMPRINT",EDGE,{"derivedFrom":sQuery(id+"F4.wireOp",EDGE,"E7.0.13.0")}),1.0]])]});
            var Q615;
            Q615=makeQuery(id+"F4.imprint","IMPRINT",FACE,{"disambiguationData":[TD([[makeQuery(id+"F4.imprint","IMPRINT",EDGE,{"derivedFrom":sQuery(id+"F4.wireOp",EDGE,"E7.0.2.0")}),1.0]])]});
            var Q616;
            Q616=makeQuery(id+"F4.imprint","IMPRINT",FACE,{"disambiguationData":[TD([[makeQuery(id+"F4.imprint","IMPRINT",EDGE,{"derivedFrom":sQuery(id+"F4.wireOp",EDGE,"E7.0.4.0")}),1.0]])]});
            var Q617;
            Q617=makeQuery(id+"F4.imprint","IMPRINT",FACE,{"disambiguationData":[TD([[makeQuery(id+"F4.imprint","IMPRINT",EDGE,{"derivedFrom":sQuery(id+"F4.wireOp",EDGE,"E7.0.6.0")}),1.0]])]});
            var Q618;
            Q618=makeQuery(id+"F4.imprint","IMPRINT",FACE,{"disambiguationData":[TD([[makeQuery(id+"F4.imprint","IMPRINT",EDGE,{"derivedFrom":sQuery(id+"F4.wireOp",EDGE,"E7.0.7.0")}),1.0]])]});
            var Q619;
            Q619=makeQuery(id+"F4.imprint","IMPRINT",FACE,{"disambiguationData":[TD([[makeQuery(id+"F4.imprint","IMPRINT",EDGE,{"derivedFrom":sQuery(id+"F4.wireOp",EDGE,"E7.0.8.0")}),1.0]])]});
            var Q620;
            Q620=makeQuery(id+"F4.imprint","IMPRINT",FACE,{"disambiguationData":[TD([[makeQuery(id+"F4.imprint","IMPRINT",EDGE,{"derivedFrom":sQuery(id+"F4.wireOp",EDGE,"E7.0.9.0")}),1.0]])]});
            var Q621;
            Q621=makeQuery(id+"F4.imprint","IMPRINT",FACE,{"disambiguationData":[TD([[makeQuery(id+"F4.imprint","IMPRINT",EDGE,{"derivedFrom":sQuery(id+"F4.wireOp",EDGE,"E7.0.10.0")}),1.0]])]});
            var Q622;
            Q622=makeQuery(id+"F4.imprint","IMPRINT",FACE,{"disambiguationData":[TD([[makeQuery(id+"F4.imprint","IMPRINT",EDGE,{"derivedFrom":sQuery(id+"F4.wireOp",EDGE,"E7.0.11.0")}),1.0]])]});
            var Q623;
            Q623=makeQuery(id+"F4.imprint","IMPRINT",FACE,{"disambiguationData":[TD([[makeQuery(id+"F4.imprint","IMPRINT",EDGE,{"derivedFrom":sQuery(id+"F4.wireOp",EDGE,"E7.1.0.0")}),1.0]])]});
            var Q624;
            Q624=makeQuery(id+"F4.imprint","IMPRINT",FACE,{"disambiguationData":[TD([[makeQuery(id+"F4.imprint","IMPRINT",EDGE,{"derivedFrom":sQuery(id+"F4.wireOp",EDGE,"E7.0.1.0")}),1.0]])]});
            extrude(context, id + "F5", {"entities" : qUnion([Q0, Q1, Q2, Q3, Q4, Q5, Q6, Q7, Q8, Q9, Q10, Q11, Q12, Q13, Q14, Q15, Q16, Q17, Q18, Q19, Q20, Q21, Q22, Q23, Q24, Q25, Q26, Q27, Q28, Q29, Q30, Q31, Q32, Q33, Q34, Q35, Q36, Q37, Q38, Q39, Q40, Q41, Q42, Q43, Q44, Q45, Q46, Q47, Q48, Q49, Q50, Q51, Q52, Q53, Q54, Q55, Q56, Q57, Q58, Q59, Q60, Q61, Q62, Q63, Q64, Q65, Q66, Q67, Q68, Q69, Q70, Q71, Q72, Q73, Q74, Q75, Q76, Q77, Q78, Q79, Q80, Q81, Q82, Q83, Q84, Q85, Q86, Q87, Q88, Q89, Q90, Q91, Q92, Q93, Q94, Q95, Q96, Q97, Q98, Q99, Q100, Q101, Q102, Q103, Q104, Q105, Q106, Q107, Q108, Q109, Q110, Q111, Q112, Q113, Q114, Q115, Q116, Q117, Q118, Q119, Q120, Q121, Q122, Q123, Q124, Q125, Q126, Q127, Q128, Q129, Q130, Q131, Q132, Q133, Q134, Q135, Q136, Q137, Q138, Q139, Q140, Q141, Q142, Q143, Q144, Q145, Q146, Q147, Q148, Q149, Q150, Q151, Q152, Q153, Q154, Q155, Q156, Q157, Q158, Q159, Q160, Q161, Q162, Q163, Q164, Q165, Q166, Q167, Q168, Q169, Q170, Q171, Q172, Q173, Q174, Q175, Q176, Q177, Q178, Q179, Q180, Q181, Q182, Q183, Q184, Q185, Q186, Q187, Q188, Q189, Q190, Q191, Q192, Q193, Q194, Q195, Q196, Q197, Q198, Q199, Q200, Q201, Q202, Q203, Q204, Q205, Q206, Q207, Q208, Q209, Q210, Q211, Q212, Q213, Q214, Q215, Q216, Q217, Q218, Q219, Q220, Q221, Q222, Q223, Q224, Q225, Q226, Q227, Q228, Q229, Q230, Q231, Q232, Q233, Q234, Q235, Q236, Q237, Q238, Q239, Q240, Q241, Q242, Q243, Q244, Q245, Q246, Q247, Q248, Q249, Q250, Q251, Q252, Q253, Q254, Q255, Q256, Q257, Q258, Q259, Q260, Q261, Q262, Q263, Q264, Q265, Q266, Q267, Q268, Q269, Q270, Q271, Q272, Q273, Q274, Q275, Q276, Q277, Q278, Q279, Q280, Q281, Q282, Q283, Q284, Q285, Q286, Q287, Q288, Q289, Q290, Q291, Q292, Q293, Q294, Q295, Q296, Q297, Q298, Q299, Q300, Q301, Q302, Q303, Q304, Q305, Q306, Q307, Q308, Q309, Q310, Q311, Q312, Q313, Q314, Q315, Q316, Q317, Q318, Q319, Q320, Q321, Q322, Q323, Q324, Q325, Q326, Q327, Q328, Q329, Q330, Q331, Q332, Q333, Q334, Q335, Q336, Q337, Q338, Q339, Q340, Q341, Q342, Q343, Q344, Q345, Q346, Q347, Q348, Q349, Q350, Q351, Q352, Q353, Q354, Q355, Q356, Q357, Q358, Q359, Q360, Q361, Q362, Q363, Q364, Q365, Q366, Q367, Q368, Q369, Q370, Q371, Q372, Q373, Q374, Q375, Q376, Q377, Q378, Q379, Q380, Q381, Q382, Q383, Q384, Q385, Q386, Q387, Q388, Q389, Q390, Q391, Q392, Q393, Q394, Q395, Q396, Q397, Q398, Q399, Q400, Q401, Q402, Q403, Q404, Q405, Q406, Q407, Q408, Q409, Q410, Q411, Q412, Q413, Q414, Q415, Q416, Q417, Q418, Q419, Q420, Q421, Q422, Q423, Q424, Q425, Q426, Q427, Q428, Q429, Q430, Q431, Q432, Q433, Q434, Q435, Q436, Q437, Q438, Q439, Q440, Q441, Q442, Q443, Q444, Q445, Q446, Q447, Q448, Q449, Q450, Q451, Q452, Q453, Q454, Q455, Q456, Q457, Q458, Q459, Q460, Q461, Q462, Q463, Q464, Q465, Q466, Q467, Q468, Q469, Q470, Q471, Q472, Q473, Q474, Q475, Q476, Q477, Q478, Q479, Q480, Q481, Q482, Q483, Q484, Q485, Q486, Q487, Q488, Q489, Q490, Q491, Q492, Q493, Q494, Q495, Q496, Q497, Q498, Q499, Q500, Q501, Q502, Q503, Q504, Q505, Q506, Q507, Q508, Q509, Q510, Q511, Q512, Q513, Q514, Q515, Q516, Q517, Q518, Q519, Q520, Q521, Q522, Q523, Q524, Q525, Q526, Q527, Q528, Q529, Q530, Q531, Q532, Q533, Q534, Q535, Q536, Q537, Q538, Q539, Q540, Q541, Q542, Q543, Q544, Q545, Q546, Q547, Q548, Q549, Q550, Q551, Q552, Q553, Q554, Q555, Q556, Q557, Q558, Q559, Q560, Q561, Q562, Q563, Q564, Q565, Q566, Q567, Q568, Q569, Q570, Q571, Q572, Q573, Q574, Q575, Q576, Q577, Q578, Q579, Q580, Q581, Q582, Q583, Q584, Q585, Q586, Q587, Q588, Q589, Q590, Q591, Q592, Q593, Q594, Q595, Q596, Q597, Q598, Q599, Q600, Q601, Q602, Q603, Q604, Q605, Q606, Q607, Q608, Q609, Q610, Q611, Q612, Q613, Q614, Q615, Q616, Q617, Q618, Q619, Q620, Q621, Q622, Q623, Q624]), "operationType" : NewBodyOperationType.ADD, "depth" : 3.17 * mm});
        }
    });
